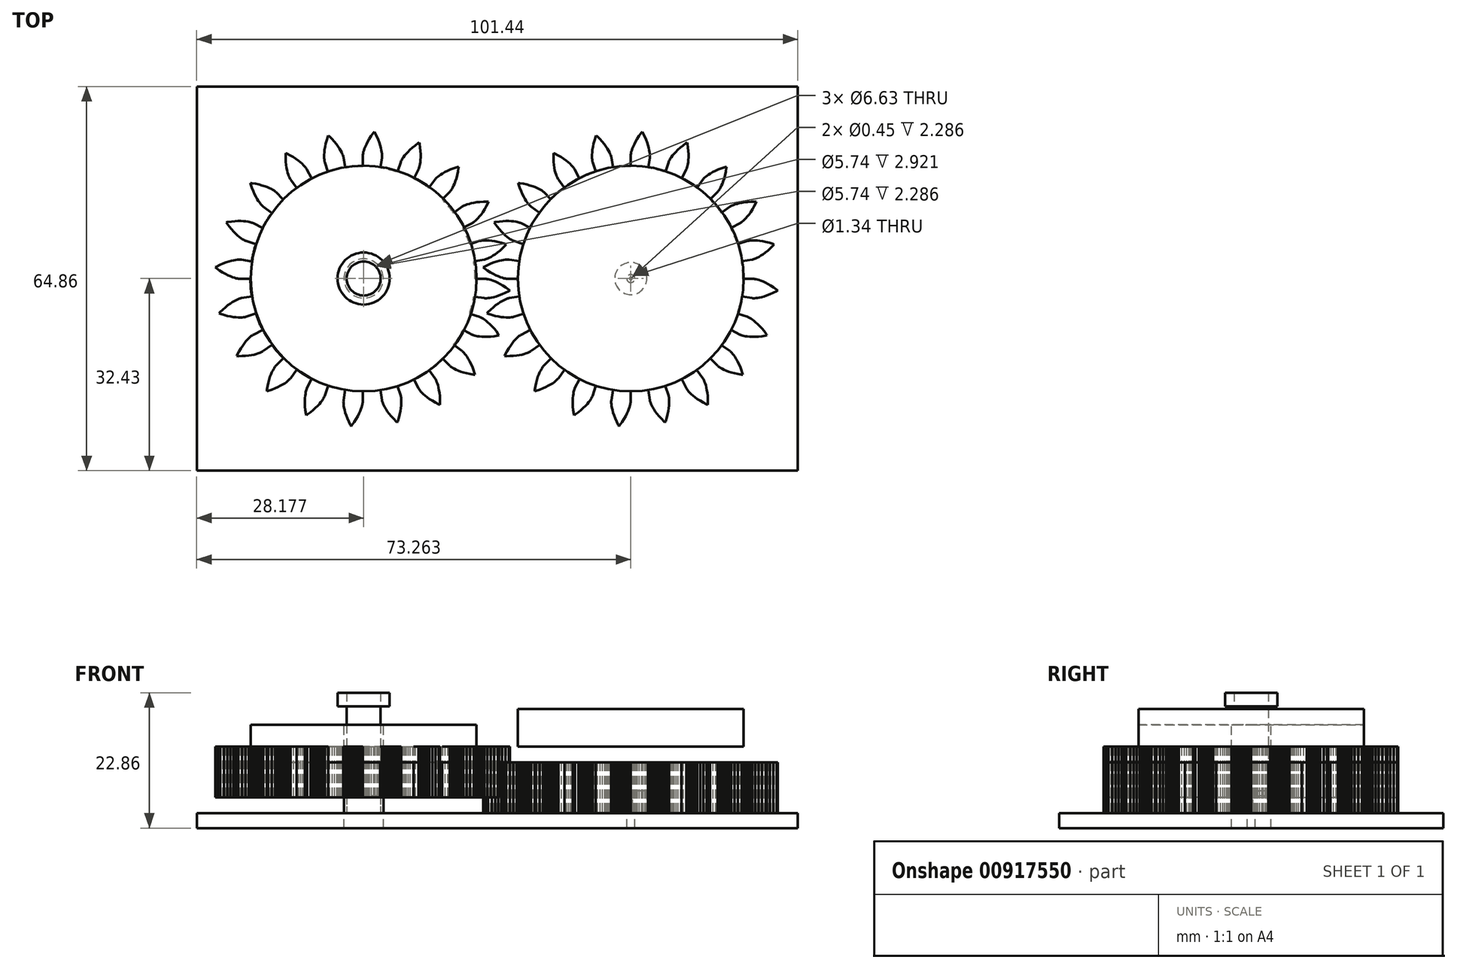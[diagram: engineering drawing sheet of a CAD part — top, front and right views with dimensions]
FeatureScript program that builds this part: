
annotation { "Feature Type Name" : "Feature", "Feature Type Description" : "" }
export const myFeature = defineFeature(function(context is Context, id is Id, definition is map)
    precondition{}
    {
        {
            var Q0;
            Q0=qCreatedBy(makeId("Top.planeOp"),FACE);
            var sketch = newSketch(context, id + "F0", { "sketchPlane" : qUnion([Q0])});
            skLineSegment(sketch, "E0.bottom", {"start": v(3.5, -4.99) * mm, "end": v(-3.5, -4.99) * mm});
            skLineSegment(sketch, "E0.top", {"start": v(3.5, 4.99) * mm, "end": v(-3.5, 4.99) * mm});
            skLineSegment(sketch, "E0.left", {"start": v(3.5, -4.99) * mm, "end": v(3.5, 4.99) * mm});
            skLineSegment(sketch, "E0.right", {"start": v(-3.5, -4.99) * mm, "end": v(-3.5, 4.99) * mm});
            skPoint(sketch, "E0.middle", {"position": v(0, 0) * mm});
            skCircle(sketch, "E1", {"center": v(-22.54, 0) * mm, "radius": 19.05 * mm});
            skPoint(sketch, "E2", {"position": v(-3.5, 0) * mm});
            skPoint(sketch, "E3", {"position": v(3.5, 0) * mm});
            skCircle(sketch, "E4", {"center": v(22.54, 0) * mm, "radius": 19.05 * mm});
            skCircle(sketch, "E5", {"center": v(-66.86, 21.55) * mm, "radius": 14.04 * mm});
            skCircle(sketch, "E6", {"center": v(-66.86, 21.55) * mm, "radius": 15.37 * mm, "construction": true});
            skCircle(sketch, "E7", {"center": v(-66.86, 21.55) * mm, "radius": 15.88 * mm, "construction": true});
            skCircle(sketch, "E8", {"center": v(-66.86, 21.55) * mm, "radius": 17.46 * mm});
            skLineSegment(sketch, "E9", {"start": v(-66.86, 21.55) * mm, "end": v(-82.23, 21.55) * mm, "construction": true});
            skLineSegment(sketch, "E10.1.0", {"start": v(-66.86, 21.55) * mm, "end": v(-82.2, 22.32) * mm, "construction": true});
            skLineSegment(sketch, "E10.2.0", {"start": v(-66.86, 21.55) * mm, "end": v(-82.15, 23.08) * mm, "construction": true});
            skLineSegment(sketch, "E10.3.0", {"start": v(-66.86, 21.55) * mm, "end": v(-82.05, 23.84) * mm, "construction": true});
            skLineSegment(sketch, "E10.4.0", {"start": v(-66.86, 21.55) * mm, "end": v(-81.92, 24.6) * mm, "construction": true});
            skLineSegment(sketch, "E10.5.0", {"start": v(-66.86, 21.55) * mm, "end": v(-81.75, 25.35) * mm, "construction": true});
            skLineSegment(sketch, "E10.6.0", {"start": v(-66.86, 21.55) * mm, "end": v(-81.54, 26.09) * mm, "construction": true});
            skLineSegment(sketch, "E10.7.0", {"start": v(-66.86, 21.55) * mm, "end": v(-81.3, 26.82) * mm, "construction": true});
            skLineSegment(sketch, "E10.8.0", {"start": v(-66.86, 21.55) * mm, "end": v(-81.01, 27.53) * mm, "construction": true});
            skLineSegment(sketch, "E10.9.0", {"start": v(-66.86, 21.55) * mm, "end": v(-80.7, 28.23) * mm, "construction": true});
            skLineSegment(sketch, "E10.10.0", {"start": v(-66.86, 21.55) * mm, "end": v(-80.34, 28.92) * mm, "construction": true});
            skLineSegment(sketch, "E10.11.0", {"start": v(-66.86, 21.55) * mm, "end": v(-79.96, 29.58) * mm, "construction": true});
            skLineSegment(sketch, "E10.12.0", {"start": v(-66.86, 21.55) * mm, "end": v(-79.54, 30.23) * mm, "construction": true});
            skLineSegment(sketch, "E10.13.0", {"start": v(-66.86, 21.55) * mm, "end": v(-79.1, 30.85) * mm, "construction": true});
            skLineSegment(sketch, "E10.14.0", {"start": v(-66.86, 21.55) * mm, "end": v(-78.61, 31.45) * mm, "construction": true});
            skLineSegment(sketch, "E10.anchor2", {"start": v(-66.86, 21.55) * mm, "end": v(-78.61, 31.45) * mm, "construction": true});
            skLineSegment(sketch, "E11", {"start": v(-82.2, 22.32) * mm, "end": v(-82.25, 21.55) * mm, "construction": true});
            skLineSegment(sketch, "E12", {"start": v(-82.15, 23.08) * mm, "end": v(-82.3, 21.55) * mm, "construction": true});
            skLineSegment(sketch, "E13", {"start": v(-82.05, 23.84) * mm, "end": v(-82.4, 21.56) * mm, "construction": true});
            skLineSegment(sketch, "E14", {"start": v(-81.75, 25.35) * mm, "end": v(-82.7, 21.63) * mm, "construction": true});
            skLineSegment(sketch, "E15", {"start": v(-81.54, 26.09) * mm, "end": v(-82.9, 21.68) * mm, "construction": true});
            skLineSegment(sketch, "E16", {"start": v(-81.3, 26.82) * mm, "end": v(-83.14, 21.76) * mm, "construction": true});
            skLineSegment(sketch, "E17", {"start": v(-81.01, 27.53) * mm, "end": v(-83.4, 21.87) * mm, "construction": true});
            skLineSegment(sketch, "E18", {"start": v(-80.7, 28.23) * mm, "end": v(-83.7, 22) * mm, "construction": true});
            skLineSegment(sketch, "E19", {"start": v(-80.34, 28.92) * mm, "end": v(-84.03, 22.17) * mm, "construction": true});
            skLineSegment(sketch, "E20", {"start": v(-79.96, 29.58) * mm, "end": v(-84.38, 22.37) * mm, "construction": true});
            skLineSegment(sketch, "E21", {"start": v(-81.92, 24.6) * mm, "end": v(-82.53, 21.59) * mm, "construction": true});
            skLineSegment(sketch, "E22", {"start": v(-79.54, 30.23) * mm, "end": v(-84.75, 22.61) * mm, "construction": true});
            skLineSegment(sketch, "E23", {"start": v(-79.1, 30.85) * mm, "end": v(-85.14, 22.9) * mm, "construction": true});
            skLineSegment(sketch, "E24", {"start": v(-78.61, 31.45) * mm, "end": v(-85.54, 23.22) * mm, "construction": true});
            skLineSegment(sketch, "E25", {"start": v(-66.86, 21.55) * mm, "end": v(-82.18, 22.75) * mm, "construction": true});
            skLineSegment(sketch, "E26", {"start": v(-80.9, 21.55) * mm, "end": v(-82.23, 21.55) * mm});
            skLineSegment(sketch, "E27.MirrorCS", {"start": v(-80.72, 23.74) * mm, "end": v(-82.04, 23.95) * mm});
            skLineSegment(sketch, "E28", {"start": v(-82.23, 21.55) * mm, "end": v(-82.25, 21.55) * mm});
            skLineSegment(sketch, "E29", {"start": v(-82.25, 21.55) * mm, "end": v(-82.3, 21.55) * mm});
            skLineSegment(sketch, "E30", {"start": v(-82.3, 21.55) * mm, "end": v(-82.4, 21.56) * mm});
            skLineSegment(sketch, "E31", {"start": v(-82.4, 21.56) * mm, "end": v(-82.53, 21.59) * mm});
            skLineSegment(sketch, "E32", {"start": v(-82.53, 21.59) * mm, "end": v(-82.7, 21.63) * mm});
            skLineSegment(sketch, "E33", {"start": v(-82.7, 21.63) * mm, "end": v(-82.9, 21.68) * mm});
            skLineSegment(sketch, "E34", {"start": v(-82.9, 21.68) * mm, "end": v(-83.14, 21.76) * mm});
            skLineSegment(sketch, "E35", {"start": v(-83.14, 21.76) * mm, "end": v(-83.4, 21.87) * mm});
            skLineSegment(sketch, "E36", {"start": v(-83.4, 21.87) * mm, "end": v(-83.7, 22) * mm});
            skLineSegment(sketch, "E37", {"start": v(-83.7, 22) * mm, "end": v(-84.03, 22.17) * mm});
            skLineSegment(sketch, "E38", {"start": v(-84.03, 22.17) * mm, "end": v(-84.38, 22.37) * mm});
            skLineSegment(sketch, "E39", {"start": v(-84.38, 22.37) * mm, "end": v(-84.75, 22.61) * mm});
            skLineSegment(sketch, "E40", {"start": v(-84.75, 22.61) * mm, "end": v(-85.14, 22.9) * mm});
            skLineSegment(sketch, "E41", {"start": v(-85.14, 22.9) * mm, "end": v(-85.54, 23.22) * mm});
            skLineSegment(sketch, "E42.MirrorCS", {"start": v(-82.04, 23.95) * mm, "end": v(-82.06, 23.95) * mm});
            skLineSegment(sketch, "E43.MirrorCS", {"start": v(-82.06, 23.95) * mm, "end": v(-82.11, 23.96) * mm});
            skLineSegment(sketch, "E44.MirrorCS", {"start": v(-82.11, 23.96) * mm, "end": v(-82.2, 23.96) * mm});
            skLineSegment(sketch, "E45.MirrorCS", {"start": v(-82.2, 23.96) * mm, "end": v(-82.34, 23.96) * mm});
            skLineSegment(sketch, "E46.MirrorCS", {"start": v(-82.52, 23.95) * mm, "end": v(-82.73, 23.92) * mm});
            skLineSegment(sketch, "E47.MirrorCS", {"start": v(-82.73, 23.92) * mm, "end": v(-82.97, 23.88) * mm});
            skLineSegment(sketch, "E48.MirrorCS", {"start": v(-82.97, 23.88) * mm, "end": v(-83.25, 23.82) * mm});
            skLineSegment(sketch, "E49.MirrorCS", {"start": v(-83.25, 23.82) * mm, "end": v(-83.57, 23.73) * mm});
            skLineSegment(sketch, "E50.MirrorCS", {"start": v(-83.91, 23.62) * mm, "end": v(-84.3, 23.47) * mm});
            skLineSegment(sketch, "E51.MirrorCS", {"start": v(-83.57, 23.73) * mm, "end": v(-83.91, 23.62) * mm});
            skLineSegment(sketch, "E52.MirrorCS", {"start": v(-84.3, 23.47) * mm, "end": v(-84.7, 23.3) * mm});
            skLineSegment(sketch, "E53.MirrorCS", {"start": v(-84.7, 23.3) * mm, "end": v(-85.12, 23.07) * mm});
            skLineSegment(sketch, "E54.MirrorCS", {"start": v(-85.12, 23.07) * mm, "end": v(-85.57, 22.82) * mm});
            skLineSegment(sketch, "E55.MirrorCS", {"start": v(-82.34, 23.96) * mm, "end": v(-82.52, 23.95) * mm});
            skLineSegment(sketch, "E56.1.0", {"start": v(-80.2, 17.2) * mm, "end": v(-81.47, 16.8) * mm});
            skLineSegment(sketch, "E56.1.1", {"start": v(-84.03, 17.99) * mm, "end": v(-84.36, 17.7) * mm});
            skLineSegment(sketch, "E56.1.2", {"start": v(-80.72, 19.35) * mm, "end": v(-82.04, 19.14) * mm});
            skLineSegment(sketch, "E56.1.3", {"start": v(-83.72, 18.24) * mm, "end": v(-84.03, 17.99) * mm});
            skLineSegment(sketch, "E56.1.4", {"start": v(-83.38, 16.83) * mm, "end": v(-83.78, 16.92) * mm});
            skLineSegment(sketch, "E56.1.5", {"start": v(-83.78, 16.92) * mm, "end": v(-84.2, 17.03) * mm});
            skLineSegment(sketch, "E56.1.6", {"start": v(-83.43, 18.46) * mm, "end": v(-83.72, 18.24) * mm});
            skLineSegment(sketch, "E56.1.7", {"start": v(-84.7, 17.36) * mm, "end": v(-85.05, 16.97) * mm});
            skLineSegment(sketch, "E56.1.8", {"start": v(-83.15, 18.64) * mm, "end": v(-83.43, 18.46) * mm});
            skLineSegment(sketch, "E56.1.9", {"start": v(-84.66, 17.18) * mm, "end": v(-85.14, 17.36) * mm});
            skLineSegment(sketch, "E56.1.10", {"start": v(-84.36, 17.7) * mm, "end": v(-84.7, 17.36) * mm});
            skLineSegment(sketch, "E56.1.11", {"start": v(-83.02, 16.78) * mm, "end": v(-83.38, 16.83) * mm});
            skLineSegment(sketch, "E56.1.12", {"start": v(-84.2, 17.03) * mm, "end": v(-84.66, 17.18) * mm});
            skLineSegment(sketch, "E56.1.13", {"start": v(-82.5, 19) * mm, "end": v(-82.68, 18.9) * mm});
            skLineSegment(sketch, "E56.1.14", {"start": v(-82.68, 18.9) * mm, "end": v(-82.9, 18.79) * mm});
            skLineSegment(sketch, "E56.1.15", {"start": v(-82.9, 18.79) * mm, "end": v(-83.15, 18.64) * mm});
            skLineSegment(sketch, "E56.1.16", {"start": v(-82.4, 16.72) * mm, "end": v(-82.7, 16.74) * mm});
            skLineSegment(sketch, "E56.1.17", {"start": v(-82.16, 16.72) * mm, "end": v(-82.4, 16.72) * mm});
            skLineSegment(sketch, "E56.1.18", {"start": v(-82.7, 16.74) * mm, "end": v(-83.02, 16.78) * mm});
            skLineSegment(sketch, "E56.1.19", {"start": v(-82.33, 19.05) * mm, "end": v(-82.5, 19) * mm});
            skLineSegment(sketch, "E56.1.20", {"start": v(-82.2, 19.1) * mm, "end": v(-82.33, 19.05) * mm});
            skLineSegment(sketch, "E56.1.21", {"start": v(-81.95, 16.73) * mm, "end": v(-82.16, 16.72) * mm});
            skLineSegment(sketch, "E56.1.22", {"start": v(-81.78, 16.74) * mm, "end": v(-81.95, 16.73) * mm});
            skLineSegment(sketch, "E56.1.23", {"start": v(-81.55, 16.78) * mm, "end": v(-81.64, 16.76) * mm});
            skLineSegment(sketch, "E56.1.24", {"start": v(-82.04, 19.14) * mm, "end": v(-82.06, 19.14) * mm});
            skLineSegment(sketch, "E56.1.25", {"start": v(-82.06, 19.14) * mm, "end": v(-82.11, 19.13) * mm});
            skLineSegment(sketch, "E56.1.26", {"start": v(-81.64, 16.76) * mm, "end": v(-81.78, 16.74) * mm});
            skLineSegment(sketch, "E56.1.27", {"start": v(-82.11, 19.13) * mm, "end": v(-82.2, 19.1) * mm});
            skLineSegment(sketch, "E56.1.28", {"start": v(-81.5, 16.8) * mm, "end": v(-81.55, 16.78) * mm});
            skLineSegment(sketch, "E56.1.29", {"start": v(-81.47, 16.8) * mm, "end": v(-81.5, 16.8) * mm});
            skLineSegment(sketch, "E56.2.0", {"start": v(-78.21, 13.3) * mm, "end": v(-79.3, 12.51) * mm});
            skLineSegment(sketch, "E56.2.1", {"start": v(-82.1, 12.86) * mm, "end": v(-82.31, 12.47) * mm});
            skLineSegment(sketch, "E56.2.2", {"start": v(-79.36, 15.17) * mm, "end": v(-80.55, 14.57) * mm});
            skLineSegment(sketch, "E56.2.3", {"start": v(-81.87, 13.2) * mm, "end": v(-82.1, 12.86) * mm});
            skLineSegment(sketch, "E56.2.4", {"start": v(-81.12, 11.96) * mm, "end": v(-81.52, 11.92) * mm});
            skLineSegment(sketch, "E56.2.5", {"start": v(-81.52, 11.92) * mm, "end": v(-81.96, 11.9) * mm});
            skLineSegment(sketch, "E56.2.6", {"start": v(-81.66, 13.5) * mm, "end": v(-81.87, 13.2) * mm});
            skLineSegment(sketch, "E56.2.7", {"start": v(-82.53, 12.05) * mm, "end": v(-82.75, 11.57) * mm});
            skLineSegment(sketch, "E56.2.8", {"start": v(-81.46, 13.75) * mm, "end": v(-81.66, 13.5) * mm});
            skLineSegment(sketch, "E56.2.9", {"start": v(-82.44, 11.9) * mm, "end": v(-82.96, 11.92) * mm});
            skLineSegment(sketch, "E56.2.10", {"start": v(-82.31, 12.47) * mm, "end": v(-82.53, 12.05) * mm});
            skLineSegment(sketch, "E56.2.11", {"start": v(-80.76, 12.01) * mm, "end": v(-81.12, 11.96) * mm});
            skLineSegment(sketch, "E56.2.12", {"start": v(-81.96, 11.9) * mm, "end": v(-82.44, 11.9) * mm});
            skLineSegment(sketch, "E56.2.13", {"start": v(-80.94, 14.28) * mm, "end": v(-81.1, 14.14) * mm});
            skLineSegment(sketch, "E56.2.14", {"start": v(-81.1, 14.14) * mm, "end": v(-81.27, 13.96) * mm});
            skLineSegment(sketch, "E56.2.15", {"start": v(-81.27, 13.96) * mm, "end": v(-81.46, 13.75) * mm});
            skLineSegment(sketch, "E56.2.16", {"start": v(-80.16, 12.15) * mm, "end": v(-80.44, 12.08) * mm});
            skLineSegment(sketch, "E56.2.17", {"start": v(-79.92, 12.23) * mm, "end": v(-80.16, 12.15) * mm});
            skLineSegment(sketch, "E56.2.18", {"start": v(-80.44, 12.08) * mm, "end": v(-80.76, 12.01) * mm});
            skLineSegment(sketch, "E56.2.19", {"start": v(-80.8, 14.4) * mm, "end": v(-80.94, 14.28) * mm});
            skLineSegment(sketch, "E56.2.20", {"start": v(-80.7, 14.48) * mm, "end": v(-80.8, 14.4) * mm});
            skLineSegment(sketch, "E56.2.21", {"start": v(-79.72, 12.3) * mm, "end": v(-79.92, 12.23) * mm});
            skLineSegment(sketch, "E56.2.22", {"start": v(-79.56, 12.37) * mm, "end": v(-79.72, 12.3) * mm});
            skLineSegment(sketch, "E56.2.23", {"start": v(-79.36, 12.47) * mm, "end": v(-79.44, 12.43) * mm});
            skLineSegment(sketch, "E56.2.24", {"start": v(-80.55, 14.57) * mm, "end": v(-80.57, 14.56) * mm});
            skLineSegment(sketch, "E56.2.25", {"start": v(-80.57, 14.56) * mm, "end": v(-80.62, 14.53) * mm});
            skLineSegment(sketch, "E56.2.26", {"start": v(-79.44, 12.43) * mm, "end": v(-79.56, 12.37) * mm});
            skLineSegment(sketch, "E56.2.27", {"start": v(-80.62, 14.53) * mm, "end": v(-80.7, 14.48) * mm});
            skLineSegment(sketch, "E56.2.28", {"start": v(-79.3, 12.5) * mm, "end": v(-79.36, 12.47) * mm});
            skLineSegment(sketch, "E56.2.29", {"start": v(-79.3, 12.51) * mm, "end": v(-79.3, 12.5) * mm});
            skLineSegment(sketch, "E56.3.0", {"start": v(-75.1, 10.19) * mm, "end": v(-75.9, 9.11) * mm});
            skLineSegment(sketch, "E56.3.1", {"start": v(-78.66, 8.57) * mm, "end": v(-78.75, 8.14) * mm});
            skLineSegment(sketch, "E56.3.2", {"start": v(-76.78, 11.62) * mm, "end": v(-77.72, 10.68) * mm});
            skLineSegment(sketch, "E56.3.3", {"start": v(-78.56, 8.96) * mm, "end": v(-78.66, 8.57) * mm});
            skLineSegment(sketch, "E56.3.4", {"start": v(-77.46, 8.02) * mm, "end": v(-77.82, 7.86) * mm});
            skLineSegment(sketch, "E56.3.5", {"start": v(-77.82, 7.86) * mm, "end": v(-78.24, 7.7) * mm});
            skLineSegment(sketch, "E56.3.6", {"start": v(-78.45, 9.31) * mm, "end": v(-78.56, 8.96) * mm});
            skLineSegment(sketch, "E56.3.7", {"start": v(-78.83, 7.67) * mm, "end": v(-78.89, 7.15) * mm});
            skLineSegment(sketch, "E56.3.8", {"start": v(-78.33, 9.62) * mm, "end": v(-78.45, 9.31) * mm});
            skLineSegment(sketch, "E56.3.9", {"start": v(-78.7, 7.55) * mm, "end": v(-79.2, 7.41) * mm});
            skLineSegment(sketch, "E56.3.10", {"start": v(-78.75, 8.14) * mm, "end": v(-78.83, 7.67) * mm});
            skLineSegment(sketch, "E56.3.11", {"start": v(-77.13, 8.19) * mm, "end": v(-77.46, 8.02) * mm});
            skLineSegment(sketch, "E56.3.12", {"start": v(-78.24, 7.7) * mm, "end": v(-78.7, 7.55) * mm});
            skLineSegment(sketch, "E56.3.13", {"start": v(-78, 10.29) * mm, "end": v(-78.1, 10.1) * mm});
            skLineSegment(sketch, "E56.3.14", {"start": v(-78.1, 10.1) * mm, "end": v(-78.22, 9.88) * mm});
            skLineSegment(sketch, "E56.3.15", {"start": v(-78.22, 9.88) * mm, "end": v(-78.33, 9.62) * mm});
            skLineSegment(sketch, "E56.3.16", {"start": v(-76.6, 8.5) * mm, "end": v(-76.85, 8.35) * mm});
            skLineSegment(sketch, "E56.3.17", {"start": v(-76.4, 8.65) * mm, "end": v(-76.6, 8.5) * mm});
            skLineSegment(sketch, "E56.3.18", {"start": v(-76.85, 8.35) * mm, "end": v(-77.13, 8.19) * mm});
            skLineSegment(sketch, "E56.3.19", {"start": v(-77.91, 10.44) * mm, "end": v(-78, 10.29) * mm});
            skLineSegment(sketch, "E56.3.20", {"start": v(-77.83, 10.55) * mm, "end": v(-77.91, 10.44) * mm});
            skLineSegment(sketch, "E56.3.21", {"start": v(-76.23, 8.78) * mm, "end": v(-76.4, 8.65) * mm});
            skLineSegment(sketch, "E56.3.22", {"start": v(-76.1, 8.9) * mm, "end": v(-76.23, 8.78) * mm});
            skLineSegment(sketch, "E56.3.23", {"start": v(-75.94, 9.05) * mm, "end": v(-76, 8.98) * mm});
            skLineSegment(sketch, "E56.3.24", {"start": v(-77.72, 10.68) * mm, "end": v(-77.74, 10.67) * mm});
            skLineSegment(sketch, "E56.3.25", {"start": v(-77.74, 10.67) * mm, "end": v(-77.77, 10.62) * mm});
            skLineSegment(sketch, "E56.3.26", {"start": v(-76, 8.98) * mm, "end": v(-76.1, 8.9) * mm});
            skLineSegment(sketch, "E56.3.27", {"start": v(-77.77, 10.62) * mm, "end": v(-77.83, 10.55) * mm});
            skLineSegment(sketch, "E56.3.28", {"start": v(-75.9, 9.1) * mm, "end": v(-75.94, 9.05) * mm});
            skLineSegment(sketch, "E56.3.29", {"start": v(-75.9, 9.11) * mm, "end": v(-75.9, 9.1) * mm});
            skLineSegment(sketch, "E56.4.0", {"start": v(-71.2, 8.2) * mm, "end": v(-71.6, 6.93) * mm});
            skLineSegment(sketch, "E56.4.1", {"start": v(-74.07, 5.56) * mm, "end": v(-74.03, 5.12) * mm});
            skLineSegment(sketch, "E56.4.2", {"start": v(-73.23, 9.04) * mm, "end": v(-73.83, 7.85) * mm});
            skLineSegment(sketch, "E56.4.3", {"start": v(-74.1, 5.96) * mm, "end": v(-74.07, 5.56) * mm});
            skLineSegment(sketch, "E56.4.4", {"start": v(-72.76, 5.4) * mm, "end": v(-73.06, 5.14) * mm});
            skLineSegment(sketch, "E56.4.5", {"start": v(-73.06, 5.14) * mm, "end": v(-73.4, 4.86) * mm});
            skLineSegment(sketch, "E56.4.6", {"start": v(-74.1, 6.33) * mm, "end": v(-74.1, 5.96) * mm});
            skLineSegment(sketch, "E56.4.7", {"start": v(-73.95, 4.65) * mm, "end": v(-73.85, 4.14) * mm});
            skLineSegment(sketch, "E56.4.8", {"start": v(-74.08, 6.65) * mm, "end": v(-74.1, 6.33) * mm});
            skLineSegment(sketch, "E56.4.9", {"start": v(-73.79, 4.58) * mm, "end": v(-74.22, 4.3) * mm});
            skLineSegment(sketch, "E56.4.10", {"start": v(-74.03, 5.12) * mm, "end": v(-73.95, 4.65) * mm});
            skLineSegment(sketch, "E56.4.11", {"start": v(-72.5, 5.67) * mm, "end": v(-72.76, 5.4) * mm});
            skLineSegment(sketch, "E56.4.12", {"start": v(-73.4, 4.86) * mm, "end": v(-73.79, 4.58) * mm});
            skLineSegment(sketch, "E56.4.13", {"start": v(-73.98, 7.4) * mm, "end": v(-74.02, 7.19) * mm});
            skLineSegment(sketch, "E56.4.14", {"start": v(-74.02, 7.19) * mm, "end": v(-74.06, 6.94) * mm});
            skLineSegment(sketch, "E56.4.15", {"start": v(-74.06, 6.94) * mm, "end": v(-74.08, 6.65) * mm});
            skLineSegment(sketch, "E56.4.16", {"start": v(-72.1, 6.13) * mm, "end": v(-72.28, 5.9) * mm});
            skLineSegment(sketch, "E56.4.17", {"start": v(-71.95, 6.33) * mm, "end": v(-72.1, 6.13) * mm});
            skLineSegment(sketch, "E56.4.18", {"start": v(-72.28, 5.9) * mm, "end": v(-72.5, 5.67) * mm});
            skLineSegment(sketch, "E56.4.19", {"start": v(-73.94, 7.56) * mm, "end": v(-73.98, 7.4) * mm});
            skLineSegment(sketch, "E56.4.20", {"start": v(-73.9, 7.7) * mm, "end": v(-73.94, 7.56) * mm});
            skLineSegment(sketch, "E56.4.21", {"start": v(-71.83, 6.5) * mm, "end": v(-71.95, 6.33) * mm});
            skLineSegment(sketch, "E56.4.22", {"start": v(-71.74, 6.65) * mm, "end": v(-71.83, 6.5) * mm});
            skLineSegment(sketch, "E56.4.23", {"start": v(-71.63, 6.86) * mm, "end": v(-71.68, 6.77) * mm});
            skLineSegment(sketch, "E56.4.24", {"start": v(-73.83, 7.85) * mm, "end": v(-73.84, 7.84) * mm});
            skLineSegment(sketch, "E56.4.25", {"start": v(-73.84, 7.84) * mm, "end": v(-73.86, 7.78) * mm});
            skLineSegment(sketch, "E56.4.26", {"start": v(-71.68, 6.77) * mm, "end": v(-71.74, 6.65) * mm});
            skLineSegment(sketch, "E56.4.27", {"start": v(-73.86, 7.78) * mm, "end": v(-73.9, 7.7) * mm});
            skLineSegment(sketch, "E56.4.28", {"start": v(-71.61, 6.91) * mm, "end": v(-71.63, 6.86) * mm});
            skLineSegment(sketch, "E56.4.29", {"start": v(-71.6, 6.93) * mm, "end": v(-71.61, 6.91) * mm});
            skLineSegment(sketch, "E56.5.0", {"start": v(-66.86, 7.5) * mm, "end": v(-66.86, 6.18) * mm});
            skLineSegment(sketch, "E56.5.1", {"start": v(-68.78, 4.11) * mm, "end": v(-68.6, 3.7) * mm});
            skLineSegment(sketch, "E56.5.2", {"start": v(-69.05, 7.68) * mm, "end": v(-69.26, 6.37) * mm});
            skLineSegment(sketch, "E56.5.3", {"start": v(-68.93, 4.49) * mm, "end": v(-68.78, 4.11) * mm});
            skLineSegment(sketch, "E56.5.4", {"start": v(-67.48, 4.37) * mm, "end": v(-67.68, 4.03) * mm});
            skLineSegment(sketch, "E56.5.5", {"start": v(-67.68, 4.03) * mm, "end": v(-67.92, 3.66) * mm});
            skLineSegment(sketch, "E56.5.6", {"start": v(-69.04, 4.84) * mm, "end": v(-68.93, 4.49) * mm});
            skLineSegment(sketch, "E56.5.7", {"start": v(-68.38, 3.28) * mm, "end": v(-68.13, 2.83) * mm});
            skLineSegment(sketch, "E56.5.8", {"start": v(-69.13, 5.15) * mm, "end": v(-69.04, 4.84) * mm});
            skLineSegment(sketch, "E56.5.9", {"start": v(-68.2, 3.27) * mm, "end": v(-68.53, 2.86) * mm});
            skLineSegment(sketch, "E56.5.10", {"start": v(-68.6, 3.7) * mm, "end": v(-68.38, 3.28) * mm});
            skLineSegment(sketch, "E56.5.11", {"start": v(-67.31, 4.7) * mm, "end": v(-67.48, 4.37) * mm});
            skLineSegment(sketch, "E56.5.12", {"start": v(-67.92, 3.66) * mm, "end": v(-68.2, 3.27) * mm});
            skLineSegment(sketch, "E56.5.13", {"start": v(-69.26, 5.89) * mm, "end": v(-69.23, 5.68) * mm});
            skLineSegment(sketch, "E56.5.14", {"start": v(-69.23, 5.68) * mm, "end": v(-69.19, 5.43) * mm});
            skLineSegment(sketch, "E56.5.15", {"start": v(-69.19, 5.43) * mm, "end": v(-69.13, 5.15) * mm});
            skLineSegment(sketch, "E56.5.16", {"start": v(-67.07, 5.26) * mm, "end": v(-67.18, 5) * mm});
            skLineSegment(sketch, "E56.5.17", {"start": v(-67, 5.5) * mm, "end": v(-67.07, 5.26) * mm});
            skLineSegment(sketch, "E56.5.18", {"start": v(-67.18, 5) * mm, "end": v(-67.31, 4.7) * mm});
            skLineSegment(sketch, "E56.5.19", {"start": v(-69.27, 6.06) * mm, "end": v(-69.26, 5.89) * mm});
            skLineSegment(sketch, "E56.5.20", {"start": v(-69.27, 6.2) * mm, "end": v(-69.27, 6.06) * mm});
            skLineSegment(sketch, "E56.5.21", {"start": v(-66.94, 5.7) * mm, "end": v(-67, 5.5) * mm});
            skLineSegment(sketch, "E56.5.22", {"start": v(-66.9, 5.87) * mm, "end": v(-66.94, 5.7) * mm});
            skLineSegment(sketch, "E56.5.23", {"start": v(-66.86, 6.1) * mm, "end": v(-66.87, 6) * mm});
            skLineSegment(sketch, "E56.5.24", {"start": v(-69.26, 6.37) * mm, "end": v(-69.26, 6.35) * mm});
            skLineSegment(sketch, "E56.5.25", {"start": v(-69.26, 6.35) * mm, "end": v(-69.27, 6.3) * mm});
            skLineSegment(sketch, "E56.5.26", {"start": v(-66.87, 6) * mm, "end": v(-66.9, 5.87) * mm});
            skLineSegment(sketch, "E56.5.27", {"start": v(-69.27, 6.3) * mm, "end": v(-69.27, 6.2) * mm});
            skLineSegment(sketch, "E56.5.28", {"start": v(-66.86, 6.16) * mm, "end": v(-66.86, 6.1) * mm});
            skLineSegment(sketch, "E56.5.29", {"start": v(-66.86, 6.18) * mm, "end": v(-66.86, 6.16) * mm});
            skLineSegment(sketch, "E56.6.0", {"start": v(-62.52, 8.2) * mm, "end": v(-62.1, 6.93) * mm});
            skLineSegment(sketch, "E56.6.1", {"start": v(-63.3, 4.37) * mm, "end": v(-63, 4.04) * mm});
            skLineSegment(sketch, "E56.6.2", {"start": v(-64.66, 7.68) * mm, "end": v(-64.45, 6.37) * mm});
            skLineSegment(sketch, "E56.6.3", {"start": v(-63.55, 4.68) * mm, "end": v(-63.3, 4.37) * mm});
            skLineSegment(sketch, "E56.6.4", {"start": v(-62.14, 5.02) * mm, "end": v(-62.23, 4.63) * mm});
            skLineSegment(sketch, "E56.6.5", {"start": v(-62.23, 4.63) * mm, "end": v(-62.34, 4.2) * mm});
            skLineSegment(sketch, "E56.6.6", {"start": v(-63.77, 4.98) * mm, "end": v(-63.55, 4.68) * mm});
            skLineSegment(sketch, "E56.6.7", {"start": v(-62.67, 3.7) * mm, "end": v(-62.28, 3.35) * mm});
            skLineSegment(sketch, "E56.6.8", {"start": v(-63.95, 5.25) * mm, "end": v(-63.77, 4.98) * mm});
            skLineSegment(sketch, "E56.6.9", {"start": v(-62.49, 3.74) * mm, "end": v(-62.67, 3.26) * mm});
            skLineSegment(sketch, "E56.6.10", {"start": v(-63, 4.04) * mm, "end": v(-62.67, 3.7) * mm});
            skLineSegment(sketch, "E56.6.11", {"start": v(-62.09, 5.38) * mm, "end": v(-62.14, 5.02) * mm});
            skLineSegment(sketch, "E56.6.12", {"start": v(-62.34, 4.2) * mm, "end": v(-62.49, 3.74) * mm});
            skLineSegment(sketch, "E56.6.13", {"start": v(-64.3, 5.91) * mm, "end": v(-64.21, 5.72) * mm});
            skLineSegment(sketch, "E56.6.14", {"start": v(-64.21, 5.72) * mm, "end": v(-64.1, 5.5) * mm});
            skLineSegment(sketch, "E56.6.15", {"start": v(-64.1, 5.5) * mm, "end": v(-63.95, 5.25) * mm});
            skLineSegment(sketch, "E56.6.16", {"start": v(-62.03, 6) * mm, "end": v(-62.05, 5.7) * mm});
            skLineSegment(sketch, "E56.6.17", {"start": v(-62.03, 6.24) * mm, "end": v(-62.03, 6) * mm});
            skLineSegment(sketch, "E56.6.18", {"start": v(-62.05, 5.7) * mm, "end": v(-62.09, 5.38) * mm});
            skLineSegment(sketch, "E56.6.19", {"start": v(-64.36, 6.07) * mm, "end": v(-64.3, 5.91) * mm});
            skLineSegment(sketch, "E56.6.20", {"start": v(-64.4, 6.2) * mm, "end": v(-64.36, 6.07) * mm});
            skLineSegment(sketch, "E56.6.21", {"start": v(-62.04, 6.46) * mm, "end": v(-62.03, 6.24) * mm});
            skLineSegment(sketch, "E56.6.22", {"start": v(-62.05, 6.63) * mm, "end": v(-62.04, 6.46) * mm});
            skLineSegment(sketch, "E56.6.23", {"start": v(-62.09, 6.86) * mm, "end": v(-62.07, 6.76) * mm});
            skLineSegment(sketch, "E56.6.24", {"start": v(-64.45, 6.37) * mm, "end": v(-64.45, 6.35) * mm});
            skLineSegment(sketch, "E56.6.25", {"start": v(-64.45, 6.35) * mm, "end": v(-64.44, 6.3) * mm});
            skLineSegment(sketch, "E56.6.26", {"start": v(-62.07, 6.76) * mm, "end": v(-62.05, 6.63) * mm});
            skLineSegment(sketch, "E56.6.27", {"start": v(-64.44, 6.3) * mm, "end": v(-64.4, 6.2) * mm});
            skLineSegment(sketch, "E56.6.28", {"start": v(-62.1, 6.91) * mm, "end": v(-62.09, 6.86) * mm});
            skLineSegment(sketch, "E56.6.29", {"start": v(-62.1, 6.93) * mm, "end": v(-62.1, 6.91) * mm});
            skLineSegment(sketch, "E56.7.0", {"start": v(-58.6, 10.19) * mm, "end": v(-57.82, 9.11) * mm});
            skLineSegment(sketch, "E56.7.1", {"start": v(-58.17, 6.31) * mm, "end": v(-57.78, 6.09) * mm});
            skLineSegment(sketch, "E56.7.2", {"start": v(-60.48, 9.04) * mm, "end": v(-59.88, 7.85) * mm});
            skLineSegment(sketch, "E56.7.3", {"start": v(-58.5, 6.53) * mm, "end": v(-58.17, 6.31) * mm});
            skLineSegment(sketch, "E56.7.4", {"start": v(-57.27, 7.29) * mm, "end": v(-57.23, 6.89) * mm});
            skLineSegment(sketch, "E56.7.5", {"start": v(-57.23, 6.89) * mm, "end": v(-57.2, 6.44) * mm});
            skLineSegment(sketch, "E56.7.6", {"start": v(-58.8, 6.74) * mm, "end": v(-58.5, 6.53) * mm});
            skLineSegment(sketch, "E56.7.7", {"start": v(-57.36, 5.87) * mm, "end": v(-56.88, 5.66) * mm});
            skLineSegment(sketch, "E56.7.8", {"start": v(-59.06, 6.95) * mm, "end": v(-58.8, 6.74) * mm});
            skLineSegment(sketch, "E56.7.9", {"start": v(-57.2, 5.96) * mm, "end": v(-57.23, 5.45) * mm});
            skLineSegment(sketch, "E56.7.10", {"start": v(-57.78, 6.09) * mm, "end": v(-57.36, 5.87) * mm});
            skLineSegment(sketch, "E56.7.11", {"start": v(-57.32, 7.65) * mm, "end": v(-57.27, 7.29) * mm});
            skLineSegment(sketch, "E56.7.12", {"start": v(-57.2, 6.44) * mm, "end": v(-57.2, 5.96) * mm});
            skLineSegment(sketch, "E56.7.13", {"start": v(-59.6, 7.47) * mm, "end": v(-59.45, 7.31) * mm});
            skLineSegment(sketch, "E56.7.14", {"start": v(-59.45, 7.31) * mm, "end": v(-59.27, 7.14) * mm});
            skLineSegment(sketch, "E56.7.15", {"start": v(-59.27, 7.14) * mm, "end": v(-59.06, 6.95) * mm});
            skLineSegment(sketch, "E56.7.16", {"start": v(-57.46, 8.25) * mm, "end": v(-57.39, 7.97) * mm});
            skLineSegment(sketch, "E56.7.17", {"start": v(-57.54, 8.49) * mm, "end": v(-57.46, 8.25) * mm});
            skLineSegment(sketch, "E56.7.18", {"start": v(-57.39, 7.97) * mm, "end": v(-57.32, 7.65) * mm});
            skLineSegment(sketch, "E56.7.19", {"start": v(-59.7, 7.6) * mm, "end": v(-59.6, 7.47) * mm});
            skLineSegment(sketch, "E56.7.20", {"start": v(-59.79, 7.7) * mm, "end": v(-59.7, 7.6) * mm});
            skLineSegment(sketch, "E56.7.21", {"start": v(-57.6, 8.68) * mm, "end": v(-57.54, 8.49) * mm});
            skLineSegment(sketch, "E56.7.22", {"start": v(-57.68, 8.84) * mm, "end": v(-57.6, 8.68) * mm});
            skLineSegment(sketch, "E56.7.23", {"start": v(-57.78, 9.05) * mm, "end": v(-57.74, 8.96) * mm});
            skLineSegment(sketch, "E56.7.24", {"start": v(-59.88, 7.85) * mm, "end": v(-59.87, 7.84) * mm});
            skLineSegment(sketch, "E56.7.25", {"start": v(-59.87, 7.84) * mm, "end": v(-59.84, 7.79) * mm});
            skLineSegment(sketch, "E56.7.26", {"start": v(-57.74, 8.96) * mm, "end": v(-57.68, 8.84) * mm});
            skLineSegment(sketch, "E56.7.27", {"start": v(-59.84, 7.79) * mm, "end": v(-59.79, 7.7) * mm});
            skLineSegment(sketch, "E56.7.28", {"start": v(-57.81, 9.1) * mm, "end": v(-57.78, 9.05) * mm});
            skLineSegment(sketch, "E56.7.29", {"start": v(-57.82, 9.11) * mm, "end": v(-57.81, 9.1) * mm});
            skLineSegment(sketch, "E56.8.0", {"start": v(-55.5, 13.3) * mm, "end": v(-54.42, 12.51) * mm});
            skLineSegment(sketch, "E56.8.1", {"start": v(-53.88, 9.74) * mm, "end": v(-53.45, 9.65) * mm});
            skLineSegment(sketch, "E56.8.2", {"start": v(-56.93, 11.62) * mm, "end": v(-55.99, 10.68) * mm});
            skLineSegment(sketch, "E56.8.3", {"start": v(-54.27, 9.85) * mm, "end": v(-53.88, 9.74) * mm});
            skLineSegment(sketch, "E56.8.4", {"start": v(-53.33, 10.95) * mm, "end": v(-53.17, 10.58) * mm});
            skLineSegment(sketch, "E56.8.5", {"start": v(-53.17, 10.58) * mm, "end": v(-53, 10.17) * mm});
            skLineSegment(sketch, "E56.8.6", {"start": v(-54.62, 9.96) * mm, "end": v(-54.27, 9.85) * mm});
            skLineSegment(sketch, "E56.8.7", {"start": v(-52.98, 9.57) * mm, "end": v(-52.46, 9.52) * mm});
            skLineSegment(sketch, "E56.8.8", {"start": v(-54.93, 10.07) * mm, "end": v(-54.62, 9.96) * mm});
            skLineSegment(sketch, "E56.8.9", {"start": v(-52.86, 9.71) * mm, "end": v(-52.72, 9.21) * mm});
            skLineSegment(sketch, "E56.8.10", {"start": v(-53.45, 9.65) * mm, "end": v(-52.98, 9.57) * mm});
            skLineSegment(sketch, "E56.8.11", {"start": v(-53.5, 11.27) * mm, "end": v(-53.33, 10.95) * mm});
            skLineSegment(sketch, "E56.8.12", {"start": v(-53, 10.17) * mm, "end": v(-52.86, 9.71) * mm});
            skLineSegment(sketch, "E56.8.13", {"start": v(-55.6, 10.4) * mm, "end": v(-55.41, 10.3) * mm});
            skLineSegment(sketch, "E56.8.14", {"start": v(-55.41, 10.3) * mm, "end": v(-55.2, 10.19) * mm});
            skLineSegment(sketch, "E56.8.15", {"start": v(-55.2, 10.19) * mm, "end": v(-54.93, 10.07) * mm});
            skLineSegment(sketch, "E56.8.16", {"start": v(-53.81, 11.8) * mm, "end": v(-53.66, 11.56) * mm});
            skLineSegment(sketch, "E56.8.17", {"start": v(-53.96, 12) * mm, "end": v(-53.81, 11.8) * mm});
            skLineSegment(sketch, "E56.8.18", {"start": v(-53.66, 11.56) * mm, "end": v(-53.5, 11.27) * mm});
            skLineSegment(sketch, "E56.8.19", {"start": v(-55.74, 10.5) * mm, "end": v(-55.6, 10.4) * mm});
            skLineSegment(sketch, "E56.8.20", {"start": v(-55.86, 10.57) * mm, "end": v(-55.74, 10.5) * mm});
            skLineSegment(sketch, "E56.8.21", {"start": v(-54.09, 12.17) * mm, "end": v(-53.96, 12) * mm});
            skLineSegment(sketch, "E56.8.22", {"start": v(-54.2, 12.3) * mm, "end": v(-54.09, 12.17) * mm});
            skLineSegment(sketch, "E56.8.23", {"start": v(-54.36, 12.46) * mm, "end": v(-54.3, 12.4) * mm});
            skLineSegment(sketch, "E56.8.24", {"start": v(-55.99, 10.68) * mm, "end": v(-55.97, 10.67) * mm});
            skLineSegment(sketch, "E56.8.25", {"start": v(-55.97, 10.67) * mm, "end": v(-55.93, 10.63) * mm});
            skLineSegment(sketch, "E56.8.26", {"start": v(-54.3, 12.4) * mm, "end": v(-54.2, 12.3) * mm});
            skLineSegment(sketch, "E56.8.27", {"start": v(-55.93, 10.63) * mm, "end": v(-55.86, 10.57) * mm});
            skLineSegment(sketch, "E56.8.28", {"start": v(-54.4, 12.5) * mm, "end": v(-54.36, 12.46) * mm});
            skLineSegment(sketch, "E56.8.29", {"start": v(-54.42, 12.51) * mm, "end": v(-54.4, 12.5) * mm});
            skLineSegment(sketch, "E56.9.0", {"start": v(-53.5, 17.2) * mm, "end": v(-52.24, 16.8) * mm});
            skLineSegment(sketch, "E56.9.1", {"start": v(-50.87, 14.33) * mm, "end": v(-50.43, 14.38) * mm});
            skLineSegment(sketch, "E56.9.2", {"start": v(-54.35, 15.17) * mm, "end": v(-53.16, 14.57) * mm});
            skLineSegment(sketch, "E56.9.3", {"start": v(-51.27, 14.3) * mm, "end": v(-50.87, 14.33) * mm});
            skLineSegment(sketch, "E56.9.4", {"start": v(-50.72, 15.65) * mm, "end": v(-50.45, 15.35) * mm});
            skLineSegment(sketch, "E56.9.5", {"start": v(-50.45, 15.35) * mm, "end": v(-50.17, 15) * mm});
            skLineSegment(sketch, "E56.9.6", {"start": v(-51.64, 14.3) * mm, "end": v(-51.27, 14.3) * mm});
            skLineSegment(sketch, "E56.9.7", {"start": v(-49.96, 14.45) * mm, "end": v(-49.45, 14.55) * mm});
            skLineSegment(sketch, "E56.9.8", {"start": v(-51.96, 14.32) * mm, "end": v(-51.64, 14.3) * mm});
            skLineSegment(sketch, "E56.9.9", {"start": v(-49.89, 14.62) * mm, "end": v(-49.6, 14.18) * mm});
            skLineSegment(sketch, "E56.9.10", {"start": v(-50.43, 14.38) * mm, "end": v(-49.96, 14.45) * mm});
            skLineSegment(sketch, "E56.9.11", {"start": v(-50.97, 15.9) * mm, "end": v(-50.72, 15.65) * mm});
            skLineSegment(sketch, "E56.9.12", {"start": v(-50.17, 15) * mm, "end": v(-49.89, 14.62) * mm});
            skLineSegment(sketch, "E56.9.13", {"start": v(-52.7, 14.43) * mm, "end": v(-52.5, 14.38) * mm});
            skLineSegment(sketch, "E56.9.14", {"start": v(-52.5, 14.38) * mm, "end": v(-52.25, 14.35) * mm});
            skLineSegment(sketch, "E56.9.15", {"start": v(-52.25, 14.35) * mm, "end": v(-51.96, 14.32) * mm});
            skLineSegment(sketch, "E56.9.16", {"start": v(-51.44, 16.3) * mm, "end": v(-51.22, 16.13) * mm});
            skLineSegment(sketch, "E56.9.17", {"start": v(-51.64, 16.46) * mm, "end": v(-51.44, 16.3) * mm});
            skLineSegment(sketch, "E56.9.18", {"start": v(-51.22, 16.13) * mm, "end": v(-50.97, 15.9) * mm});
            skLineSegment(sketch, "E56.9.19", {"start": v(-52.87, 14.47) * mm, "end": v(-52.7, 14.43) * mm});
            skLineSegment(sketch, "E56.9.20", {"start": v(-53, 14.5) * mm, "end": v(-52.87, 14.47) * mm});
            skLineSegment(sketch, "E56.9.21", {"start": v(-51.81, 16.58) * mm, "end": v(-51.64, 16.46) * mm});
            skLineSegment(sketch, "E56.9.22", {"start": v(-51.96, 16.66) * mm, "end": v(-51.81, 16.58) * mm});
            skLineSegment(sketch, "E56.9.23", {"start": v(-52.17, 16.77) * mm, "end": v(-52.08, 16.73) * mm});
            skLineSegment(sketch, "E56.9.24", {"start": v(-53.16, 14.57) * mm, "end": v(-53.15, 14.56) * mm});
            skLineSegment(sketch, "E56.9.25", {"start": v(-53.15, 14.56) * mm, "end": v(-53.1, 14.54) * mm});
            skLineSegment(sketch, "E56.9.26", {"start": v(-52.08, 16.73) * mm, "end": v(-51.96, 16.66) * mm});
            skLineSegment(sketch, "E56.9.27", {"start": v(-53.1, 14.54) * mm, "end": v(-53, 14.5) * mm});
            skLineSegment(sketch, "E56.9.28", {"start": v(-52.22, 16.8) * mm, "end": v(-52.17, 16.77) * mm});
            skLineSegment(sketch, "E56.9.29", {"start": v(-52.24, 16.8) * mm, "end": v(-52.22, 16.8) * mm});
            skLineSegment(sketch, "E56.10.0", {"start": v(-52.82, 21.55) * mm, "end": v(-51.49, 21.55) * mm});
            skLineSegment(sketch, "E56.10.1", {"start": v(-49.42, 19.62) * mm, "end": v(-49.02, 19.8) * mm});
            skLineSegment(sketch, "E56.10.2", {"start": v(-53, 19.35) * mm, "end": v(-51.68, 19.14) * mm});
            skLineSegment(sketch, "E56.10.3", {"start": v(-49.8, 19.48) * mm, "end": v(-49.42, 19.62) * mm});
            skLineSegment(sketch, "E56.10.4", {"start": v(-49.68, 20.92) * mm, "end": v(-49.34, 20.72) * mm});
            skLineSegment(sketch, "E56.10.5", {"start": v(-49.34, 20.72) * mm, "end": v(-48.96, 20.48) * mm});
            skLineSegment(sketch, "E56.10.6", {"start": v(-50.14, 19.36) * mm, "end": v(-49.8, 19.48) * mm});
            skLineSegment(sketch, "E56.10.7", {"start": v(-48.59, 20.02) * mm, "end": v(-48.14, 20.28) * mm});
            skLineSegment(sketch, "E56.10.8", {"start": v(-50.46, 19.28) * mm, "end": v(-50.14, 19.36) * mm});
            skLineSegment(sketch, "E56.10.9", {"start": v(-48.58, 20.2) * mm, "end": v(-48.17, 19.87) * mm});
            skLineSegment(sketch, "E56.10.10", {"start": v(-49.02, 19.8) * mm, "end": v(-48.59, 20.02) * mm});
            skLineSegment(sketch, "E56.10.11", {"start": v(-50, 21.09) * mm, "end": v(-49.68, 20.92) * mm});
            skLineSegment(sketch, "E56.10.12", {"start": v(-48.96, 20.48) * mm, "end": v(-48.58, 20.2) * mm});
            skLineSegment(sketch, "E56.10.13", {"start": v(-51.2, 19.15) * mm, "end": v(-50.99, 19.17) * mm});
            skLineSegment(sketch, "E56.10.14", {"start": v(-50.99, 19.17) * mm, "end": v(-50.74, 19.21) * mm});
            skLineSegment(sketch, "E56.10.15", {"start": v(-50.74, 19.21) * mm, "end": v(-50.46, 19.28) * mm});
            skLineSegment(sketch, "E56.10.16", {"start": v(-50.57, 21.33) * mm, "end": v(-50.3, 21.22) * mm});
            skLineSegment(sketch, "E56.10.17", {"start": v(-50.81, 21.4) * mm, "end": v(-50.57, 21.33) * mm});
            skLineSegment(sketch, "E56.10.18", {"start": v(-50.3, 21.22) * mm, "end": v(-50, 21.09) * mm});
            skLineSegment(sketch, "E56.10.19", {"start": v(-51.37, 19.14) * mm, "end": v(-51.2, 19.15) * mm});
            skLineSegment(sketch, "E56.10.20", {"start": v(-51.5, 19.13) * mm, "end": v(-51.37, 19.14) * mm});
            skLineSegment(sketch, "E56.10.21", {"start": v(-51.01, 21.47) * mm, "end": v(-50.81, 21.4) * mm});
            skLineSegment(sketch, "E56.10.22", {"start": v(-51.18, 21.5) * mm, "end": v(-51.01, 21.47) * mm});
            skLineSegment(sketch, "E56.10.23", {"start": v(-51.41, 21.54) * mm, "end": v(-51.32, 21.53) * mm});
            skLineSegment(sketch, "E56.10.24", {"start": v(-51.68, 19.14) * mm, "end": v(-51.66, 19.14) * mm});
            skLineSegment(sketch, "E56.10.25", {"start": v(-51.66, 19.14) * mm, "end": v(-51.6, 19.14) * mm});
            skLineSegment(sketch, "E56.10.26", {"start": v(-51.32, 21.53) * mm, "end": v(-51.18, 21.5) * mm});
            skLineSegment(sketch, "E56.10.27", {"start": v(-51.6, 19.14) * mm, "end": v(-51.5, 19.13) * mm});
            skLineSegment(sketch, "E56.10.28", {"start": v(-51.47, 21.55) * mm, "end": v(-51.41, 21.54) * mm});
            skLineSegment(sketch, "E56.10.29", {"start": v(-51.49, 21.55) * mm, "end": v(-51.47, 21.55) * mm});
            skLineSegment(sketch, "E56.11.0", {"start": v(-53.5, 25.88) * mm, "end": v(-52.24, 26.3) * mm});
            skLineSegment(sketch, "E56.11.1", {"start": v(-49.68, 25.1) * mm, "end": v(-49.35, 25.4) * mm});
            skLineSegment(sketch, "E56.11.2", {"start": v(-53, 23.74) * mm, "end": v(-51.68, 23.95) * mm});
            skLineSegment(sketch, "E56.11.3", {"start": v(-50, 24.85) * mm, "end": v(-49.68, 25.1) * mm});
            skLineSegment(sketch, "E56.11.4", {"start": v(-50.33, 26.26) * mm, "end": v(-49.94, 26.17) * mm});
            skLineSegment(sketch, "E56.11.5", {"start": v(-49.94, 26.17) * mm, "end": v(-49.51, 26.06) * mm});
            skLineSegment(sketch, "E56.11.6", {"start": v(-50.29, 24.63) * mm, "end": v(-50, 24.85) * mm});
            skLineSegment(sketch, "E56.11.7", {"start": v(-49.01, 25.74) * mm, "end": v(-48.66, 26.12) * mm});
            skLineSegment(sketch, "E56.11.8", {"start": v(-50.56, 24.45) * mm, "end": v(-50.29, 24.63) * mm});
            skLineSegment(sketch, "E56.11.9", {"start": v(-49.05, 25.91) * mm, "end": v(-48.57, 25.73) * mm});
            skLineSegment(sketch, "E56.11.10", {"start": v(-49.35, 25.4) * mm, "end": v(-49.01, 25.74) * mm});
            skLineSegment(sketch, "E56.11.11", {"start": v(-50.7, 26.32) * mm, "end": v(-50.33, 26.26) * mm});
            skLineSegment(sketch, "E56.11.12", {"start": v(-49.51, 26.06) * mm, "end": v(-49.05, 25.91) * mm});
            skLineSegment(sketch, "E56.11.13", {"start": v(-51.22, 24.1) * mm, "end": v(-51.03, 24.2) * mm});
            skLineSegment(sketch, "E56.11.14", {"start": v(-51.03, 24.2) * mm, "end": v(-50.8, 24.3) * mm});
            skLineSegment(sketch, "E56.11.15", {"start": v(-50.8, 24.3) * mm, "end": v(-50.56, 24.45) * mm});
            skLineSegment(sketch, "E56.11.16", {"start": v(-51.3, 26.37) * mm, "end": v(-51.02, 26.35) * mm});
            skLineSegment(sketch, "E56.11.17", {"start": v(-51.55, 26.37) * mm, "end": v(-51.3, 26.37) * mm});
            skLineSegment(sketch, "E56.11.18", {"start": v(-51.02, 26.35) * mm, "end": v(-50.7, 26.32) * mm});
            skLineSegment(sketch, "E56.11.19", {"start": v(-51.38, 24.04) * mm, "end": v(-51.22, 24.1) * mm});
            skLineSegment(sketch, "E56.11.20", {"start": v(-51.5, 24) * mm, "end": v(-51.38, 24.04) * mm});
            skLineSegment(sketch, "E56.11.21", {"start": v(-51.77, 26.37) * mm, "end": v(-51.55, 26.37) * mm});
            skLineSegment(sketch, "E56.11.22", {"start": v(-51.94, 26.35) * mm, "end": v(-51.77, 26.37) * mm});
            skLineSegment(sketch, "E56.11.23", {"start": v(-52.17, 26.32) * mm, "end": v(-52.07, 26.33) * mm});
            skLineSegment(sketch, "E56.11.24", {"start": v(-51.68, 23.95) * mm, "end": v(-51.66, 23.95) * mm});
            skLineSegment(sketch, "E56.11.25", {"start": v(-51.66, 23.95) * mm, "end": v(-51.6, 23.97) * mm});
            skLineSegment(sketch, "E56.11.26", {"start": v(-52.07, 26.33) * mm, "end": v(-51.94, 26.35) * mm});
            skLineSegment(sketch, "E56.11.27", {"start": v(-51.6, 23.97) * mm, "end": v(-51.5, 24) * mm});
            skLineSegment(sketch, "E56.11.28", {"start": v(-52.22, 26.3) * mm, "end": v(-52.17, 26.32) * mm});
            skLineSegment(sketch, "E56.11.29", {"start": v(-52.24, 26.3) * mm, "end": v(-52.22, 26.3) * mm});
            skLineSegment(sketch, "E56.12.0", {"start": v(-55.5, 29.8) * mm, "end": v(-54.42, 30.58) * mm});
            skLineSegment(sketch, "E56.12.1", {"start": v(-51.62, 30.24) * mm, "end": v(-51.4, 30.62) * mm});
            skLineSegment(sketch, "E56.12.2", {"start": v(-54.35, 27.92) * mm, "end": v(-53.16, 28.52) * mm});
            skLineSegment(sketch, "E56.12.3", {"start": v(-51.84, 29.9) * mm, "end": v(-51.62, 30.24) * mm});
            skLineSegment(sketch, "E56.12.4", {"start": v(-52.6, 31.14) * mm, "end": v(-52.2, 31.18) * mm});
            skLineSegment(sketch, "E56.12.5", {"start": v(-52.2, 31.18) * mm, "end": v(-51.75, 31.2) * mm});
            skLineSegment(sketch, "E56.12.6", {"start": v(-52.05, 29.6) * mm, "end": v(-51.84, 29.9) * mm});
            skLineSegment(sketch, "E56.12.7", {"start": v(-51.18, 31.05) * mm, "end": v(-50.97, 31.52) * mm});
            skLineSegment(sketch, "E56.12.8", {"start": v(-52.26, 29.35) * mm, "end": v(-52.05, 29.6) * mm});
            skLineSegment(sketch, "E56.12.9", {"start": v(-51.27, 31.2) * mm, "end": v(-50.76, 31.18) * mm});
            skLineSegment(sketch, "E56.12.10", {"start": v(-51.4, 30.62) * mm, "end": v(-51.18, 31.05) * mm});
            skLineSegment(sketch, "E56.12.11", {"start": v(-52.96, 31.08) * mm, "end": v(-52.6, 31.14) * mm});
            skLineSegment(sketch, "E56.12.12", {"start": v(-51.75, 31.2) * mm, "end": v(-51.27, 31.2) * mm});
            skLineSegment(sketch, "E56.12.13", {"start": v(-52.78, 28.8) * mm, "end": v(-52.62, 28.95) * mm});
            skLineSegment(sketch, "E56.12.14", {"start": v(-52.62, 28.95) * mm, "end": v(-52.45, 29.13) * mm});
            skLineSegment(sketch, "E56.12.15", {"start": v(-52.45, 29.13) * mm, "end": v(-52.26, 29.35) * mm});
            skLineSegment(sketch, "E56.12.16", {"start": v(-53.56, 30.94) * mm, "end": v(-53.28, 31.01) * mm});
            skLineSegment(sketch, "E56.12.17", {"start": v(-53.8, 30.87) * mm, "end": v(-53.56, 30.94) * mm});
            skLineSegment(sketch, "E56.12.18", {"start": v(-53.28, 31.01) * mm, "end": v(-52.96, 31.08) * mm});
            skLineSegment(sketch, "E56.12.19", {"start": v(-52.9, 28.7) * mm, "end": v(-52.78, 28.8) * mm});
            skLineSegment(sketch, "E56.12.20", {"start": v(-53.02, 28.62) * mm, "end": v(-52.9, 28.7) * mm});
            skLineSegment(sketch, "E56.12.21", {"start": v(-54, 30.8) * mm, "end": v(-53.8, 30.87) * mm});
            skLineSegment(sketch, "E56.12.22", {"start": v(-54.15, 30.73) * mm, "end": v(-54, 30.8) * mm});
            skLineSegment(sketch, "E56.12.23", {"start": v(-54.36, 30.62) * mm, "end": v(-54.27, 30.67) * mm});
            skLineSegment(sketch, "E56.12.24", {"start": v(-53.16, 28.52) * mm, "end": v(-53.15, 28.53) * mm});
            skLineSegment(sketch, "E56.12.25", {"start": v(-53.15, 28.53) * mm, "end": v(-53.1, 28.56) * mm});
            skLineSegment(sketch, "E56.12.26", {"start": v(-54.27, 30.67) * mm, "end": v(-54.15, 30.73) * mm});
            skLineSegment(sketch, "E56.12.27", {"start": v(-53.1, 28.56) * mm, "end": v(-53.02, 28.62) * mm});
            skLineSegment(sketch, "E56.12.28", {"start": v(-54.4, 30.6) * mm, "end": v(-54.36, 30.62) * mm});
            skLineSegment(sketch, "E56.12.29", {"start": v(-54.42, 30.58) * mm, "end": v(-54.4, 30.6) * mm});
            skLineSegment(sketch, "E56.13.0", {"start": v(-58.6, 32.9) * mm, "end": v(-57.82, 33.98) * mm});
            skLineSegment(sketch, "E56.13.1", {"start": v(-55.05, 34.52) * mm, "end": v(-54.96, 34.95) * mm});
            skLineSegment(sketch, "E56.13.2", {"start": v(-56.93, 31.47) * mm, "end": v(-55.99, 32.41) * mm});
            skLineSegment(sketch, "E56.13.3", {"start": v(-55.16, 34.13) * mm, "end": v(-55.05, 34.52) * mm});
            skLineSegment(sketch, "E56.13.4", {"start": v(-56.26, 35.07) * mm, "end": v(-55.89, 35.24) * mm});
            skLineSegment(sketch, "E56.13.5", {"start": v(-55.89, 35.24) * mm, "end": v(-55.48, 35.4) * mm});
            skLineSegment(sketch, "E56.13.6", {"start": v(-55.27, 33.78) * mm, "end": v(-55.16, 34.13) * mm});
            skLineSegment(sketch, "E56.13.7", {"start": v(-54.88, 35.43) * mm, "end": v(-54.83, 35.94) * mm});
            skLineSegment(sketch, "E56.13.8", {"start": v(-55.38, 33.48) * mm, "end": v(-55.27, 33.78) * mm});
            skLineSegment(sketch, "E56.13.9", {"start": v(-55.02, 35.54) * mm, "end": v(-54.52, 35.68) * mm});
            skLineSegment(sketch, "E56.13.10", {"start": v(-54.96, 34.95) * mm, "end": v(-54.88, 35.43) * mm});
            skLineSegment(sketch, "E56.13.11", {"start": v(-56.58, 34.9) * mm, "end": v(-56.26, 35.07) * mm});
            skLineSegment(sketch, "E56.13.12", {"start": v(-55.48, 35.4) * mm, "end": v(-55.02, 35.54) * mm});
            skLineSegment(sketch, "E56.13.13", {"start": v(-55.71, 32.8) * mm, "end": v(-55.6, 32.99) * mm});
            skLineSegment(sketch, "E56.13.14", {"start": v(-55.6, 32.99) * mm, "end": v(-55.5, 33.21) * mm});
            skLineSegment(sketch, "E56.13.15", {"start": v(-55.5, 33.21) * mm, "end": v(-55.38, 33.48) * mm});
            skLineSegment(sketch, "E56.13.16", {"start": v(-57.11, 34.6) * mm, "end": v(-56.87, 34.75) * mm});
            skLineSegment(sketch, "E56.13.17", {"start": v(-57.31, 34.45) * mm, "end": v(-57.11, 34.6) * mm});
            skLineSegment(sketch, "E56.13.18", {"start": v(-56.87, 34.75) * mm, "end": v(-56.58, 34.9) * mm});
            skLineSegment(sketch, "E56.13.19", {"start": v(-55.8, 32.66) * mm, "end": v(-55.71, 32.8) * mm});
            skLineSegment(sketch, "E56.13.20", {"start": v(-55.88, 32.55) * mm, "end": v(-55.8, 32.66) * mm});
            skLineSegment(sketch, "E56.13.21", {"start": v(-57.48, 34.32) * mm, "end": v(-57.31, 34.45) * mm});
            skLineSegment(sketch, "E56.13.22", {"start": v(-57.61, 34.2) * mm, "end": v(-57.48, 34.32) * mm});
            skLineSegment(sketch, "E56.13.23", {"start": v(-57.77, 34.04) * mm, "end": v(-57.7, 34.1) * mm});
            skLineSegment(sketch, "E56.13.24", {"start": v(-55.99, 32.41) * mm, "end": v(-55.98, 32.43) * mm});
            skLineSegment(sketch, "E56.13.25", {"start": v(-55.98, 32.43) * mm, "end": v(-55.94, 32.47) * mm});
            skLineSegment(sketch, "E56.13.26", {"start": v(-57.7, 34.1) * mm, "end": v(-57.61, 34.2) * mm});
            skLineSegment(sketch, "E56.13.27", {"start": v(-55.94, 32.47) * mm, "end": v(-55.88, 32.55) * mm});
            skLineSegment(sketch, "E56.13.28", {"start": v(-57.81, 34) * mm, "end": v(-57.77, 34.04) * mm});
            skLineSegment(sketch, "E56.13.29", {"start": v(-57.82, 33.98) * mm, "end": v(-57.81, 34) * mm});
            skLineSegment(sketch, "E56.14.0", {"start": v(-62.52, 34.9) * mm, "end": v(-62.1, 36.16) * mm});
            skLineSegment(sketch, "E56.14.1", {"start": v(-59.64, 37.53) * mm, "end": v(-59.68, 37.97) * mm});
            skLineSegment(sketch, "E56.14.2", {"start": v(-60.48, 34.06) * mm, "end": v(-59.88, 35.24) * mm});
            skLineSegment(sketch, "E56.14.3", {"start": v(-59.62, 37.13) * mm, "end": v(-59.64, 37.53) * mm});
            skLineSegment(sketch, "E56.14.4", {"start": v(-60.96, 37.69) * mm, "end": v(-60.66, 37.95) * mm});
            skLineSegment(sketch, "E56.14.5", {"start": v(-60.66, 37.95) * mm, "end": v(-60.31, 38.23) * mm});
            skLineSegment(sketch, "E56.14.6", {"start": v(-59.62, 36.77) * mm, "end": v(-59.62, 37.13) * mm});
            skLineSegment(sketch, "E56.14.7", {"start": v(-59.76, 38.45) * mm, "end": v(-59.86, 38.96) * mm});
            skLineSegment(sketch, "E56.14.8", {"start": v(-59.63, 36.44) * mm, "end": v(-59.62, 36.77) * mm});
            skLineSegment(sketch, "E56.14.9", {"start": v(-59.93, 38.52) * mm, "end": v(-59.5, 38.8) * mm});
            skLineSegment(sketch, "E56.14.10", {"start": v(-59.68, 37.97) * mm, "end": v(-59.76, 38.45) * mm});
            skLineSegment(sketch, "E56.14.11", {"start": v(-61.22, 37.43) * mm, "end": v(-60.96, 37.69) * mm});
            skLineSegment(sketch, "E56.14.12", {"start": v(-60.31, 38.23) * mm, "end": v(-59.93, 38.52) * mm});
            skLineSegment(sketch, "E56.14.13", {"start": v(-59.74, 35.7) * mm, "end": v(-59.7, 35.9) * mm});
            skLineSegment(sketch, "E56.14.14", {"start": v(-59.7, 35.9) * mm, "end": v(-59.66, 36.15) * mm});
            skLineSegment(sketch, "E56.14.15", {"start": v(-59.66, 36.15) * mm, "end": v(-59.63, 36.44) * mm});
            skLineSegment(sketch, "E56.14.16", {"start": v(-61.62, 36.96) * mm, "end": v(-61.44, 37.19) * mm});
            skLineSegment(sketch, "E56.14.17", {"start": v(-61.77, 36.76) * mm, "end": v(-61.62, 36.96) * mm});
            skLineSegment(sketch, "E56.14.18", {"start": v(-61.44, 37.19) * mm, "end": v(-61.22, 37.43) * mm});
            skLineSegment(sketch, "E56.14.19", {"start": v(-59.78, 35.53) * mm, "end": v(-59.74, 35.7) * mm});
            skLineSegment(sketch, "E56.14.20", {"start": v(-59.82, 35.4) * mm, "end": v(-59.78, 35.53) * mm});
            skLineSegment(sketch, "E56.14.21", {"start": v(-61.89, 36.59) * mm, "end": v(-61.77, 36.76) * mm});
            skLineSegment(sketch, "E56.14.22", {"start": v(-61.97, 36.44) * mm, "end": v(-61.89, 36.59) * mm});
            skLineSegment(sketch, "E56.14.23", {"start": v(-62.08, 36.24) * mm, "end": v(-62.04, 36.32) * mm});
            skLineSegment(sketch, "E56.14.24", {"start": v(-59.88, 35.24) * mm, "end": v(-59.87, 35.26) * mm});
            skLineSegment(sketch, "E56.14.25", {"start": v(-59.87, 35.26) * mm, "end": v(-59.85, 35.31) * mm});
            skLineSegment(sketch, "E56.14.26", {"start": v(-62.04, 36.32) * mm, "end": v(-61.97, 36.44) * mm});
            skLineSegment(sketch, "E56.14.27", {"start": v(-59.85, 35.31) * mm, "end": v(-59.82, 35.4) * mm});
            skLineSegment(sketch, "E56.14.28", {"start": v(-62.1, 36.18) * mm, "end": v(-62.08, 36.24) * mm});
            skLineSegment(sketch, "E56.14.29", {"start": v(-62.1, 36.16) * mm, "end": v(-62.1, 36.18) * mm});
            skLineSegment(sketch, "E56.15.0", {"start": v(-66.86, 35.59) * mm, "end": v(-66.86, 36.92) * mm});
            skLineSegment(sketch, "E56.15.1", {"start": v(-64.93, 38.98) * mm, "end": v(-65.11, 39.39) * mm});
            skLineSegment(sketch, "E56.15.2", {"start": v(-64.66, 35.41) * mm, "end": v(-64.45, 36.73) * mm});
            skLineSegment(sketch, "E56.15.3", {"start": v(-64.79, 38.6) * mm, "end": v(-64.93, 38.98) * mm});
            skLineSegment(sketch, "E56.15.4", {"start": v(-66.23, 38.72) * mm, "end": v(-66.03, 39.07) * mm});
            skLineSegment(sketch, "E56.15.5", {"start": v(-66.03, 39.07) * mm, "end": v(-65.79, 39.44) * mm});
            skLineSegment(sketch, "E56.15.6", {"start": v(-64.67, 38.26) * mm, "end": v(-64.79, 38.6) * mm});
            skLineSegment(sketch, "E56.15.7", {"start": v(-65.33, 39.81) * mm, "end": v(-65.59, 40.26) * mm});
            skLineSegment(sketch, "E56.15.8", {"start": v(-64.59, 37.94) * mm, "end": v(-64.67, 38.26) * mm});
            skLineSegment(sketch, "E56.15.9", {"start": v(-65.5, 39.83) * mm, "end": v(-65.18, 40.23) * mm});
            skLineSegment(sketch, "E56.15.10", {"start": v(-65.11, 39.39) * mm, "end": v(-65.33, 39.81) * mm});
            skLineSegment(sketch, "E56.15.11", {"start": v(-66.4, 38.4) * mm, "end": v(-66.23, 38.72) * mm});
            skLineSegment(sketch, "E56.15.12", {"start": v(-65.79, 39.44) * mm, "end": v(-65.5, 39.83) * mm});
            skLineSegment(sketch, "E56.15.13", {"start": v(-64.46, 37.2) * mm, "end": v(-64.48, 37.42) * mm});
            skLineSegment(sketch, "E56.15.14", {"start": v(-64.48, 37.42) * mm, "end": v(-64.52, 37.66) * mm});
            skLineSegment(sketch, "E56.15.15", {"start": v(-64.52, 37.66) * mm, "end": v(-64.59, 37.94) * mm});
            skLineSegment(sketch, "E56.15.16", {"start": v(-66.64, 37.83) * mm, "end": v(-66.53, 38.1) * mm});
            skLineSegment(sketch, "E56.15.17", {"start": v(-66.72, 37.6) * mm, "end": v(-66.64, 37.83) * mm});
            skLineSegment(sketch, "E56.15.18", {"start": v(-66.53, 38.1) * mm, "end": v(-66.4, 38.4) * mm});
            skLineSegment(sketch, "E56.15.19", {"start": v(-64.45, 37.03) * mm, "end": v(-64.46, 37.2) * mm});
            skLineSegment(sketch, "E56.15.20", {"start": v(-64.44, 36.9) * mm, "end": v(-64.45, 37.03) * mm});
            skLineSegment(sketch, "E56.15.21", {"start": v(-66.78, 37.39) * mm, "end": v(-66.72, 37.6) * mm});
            skLineSegment(sketch, "E56.15.22", {"start": v(-66.82, 37.22) * mm, "end": v(-66.78, 37.39) * mm});
            skLineSegment(sketch, "E56.15.23", {"start": v(-66.85, 37) * mm, "end": v(-66.84, 37.09) * mm});
            skLineSegment(sketch, "E56.15.24", {"start": v(-64.45, 36.73) * mm, "end": v(-64.45, 36.75) * mm});
            skLineSegment(sketch, "E56.15.25", {"start": v(-64.45, 36.75) * mm, "end": v(-64.45, 36.8) * mm});
            skLineSegment(sketch, "E56.15.26", {"start": v(-66.84, 37.09) * mm, "end": v(-66.82, 37.22) * mm});
            skLineSegment(sketch, "E56.15.27", {"start": v(-64.45, 36.8) * mm, "end": v(-64.44, 36.9) * mm});
            skLineSegment(sketch, "E56.15.28", {"start": v(-66.86, 36.94) * mm, "end": v(-66.85, 37) * mm});
            skLineSegment(sketch, "E56.15.29", {"start": v(-66.86, 36.92) * mm, "end": v(-66.86, 36.94) * mm});
            skLineSegment(sketch, "E56.16.0", {"start": v(-71.2, 34.9) * mm, "end": v(-71.6, 36.16) * mm});
            skLineSegment(sketch, "E56.16.1", {"start": v(-70.41, 38.72) * mm, "end": v(-70.7, 39.05) * mm});
            skLineSegment(sketch, "E56.16.2", {"start": v(-69.05, 35.41) * mm, "end": v(-69.26, 36.73) * mm});
            skLineSegment(sketch, "E56.16.3", {"start": v(-70.16, 38.4) * mm, "end": v(-70.41, 38.72) * mm});
            skLineSegment(sketch, "E56.16.4", {"start": v(-71.57, 38.07) * mm, "end": v(-71.48, 38.47) * mm});
            skLineSegment(sketch, "E56.16.5", {"start": v(-71.48, 38.47) * mm, "end": v(-71.37, 38.9) * mm});
            skLineSegment(sketch, "E56.16.6", {"start": v(-69.94, 38.12) * mm, "end": v(-70.16, 38.4) * mm});
            skLineSegment(sketch, "E56.16.7", {"start": v(-71.05, 39.4) * mm, "end": v(-71.43, 39.74) * mm});
            skLineSegment(sketch, "E56.16.8", {"start": v(-69.76, 37.84) * mm, "end": v(-69.94, 38.12) * mm});
            skLineSegment(sketch, "E56.16.9", {"start": v(-71.22, 39.35) * mm, "end": v(-71.04, 39.84) * mm});
            skLineSegment(sketch, "E56.16.10", {"start": v(-70.7, 39.05) * mm, "end": v(-71.05, 39.4) * mm});
            skLineSegment(sketch, "E56.16.11", {"start": v(-71.63, 37.71) * mm, "end": v(-71.57, 38.07) * mm});
            skLineSegment(sketch, "E56.16.12", {"start": v(-71.37, 38.9) * mm, "end": v(-71.22, 39.35) * mm});
            skLineSegment(sketch, "E56.16.13", {"start": v(-69.41, 37.18) * mm, "end": v(-69.5, 37.37) * mm});
            skLineSegment(sketch, "E56.16.14", {"start": v(-69.5, 37.37) * mm, "end": v(-69.62, 37.6) * mm});
            skLineSegment(sketch, "E56.16.15", {"start": v(-69.62, 37.6) * mm, "end": v(-69.76, 37.84) * mm});
            skLineSegment(sketch, "E56.16.16", {"start": v(-71.68, 37.1) * mm, "end": v(-71.66, 37.39) * mm});
            skLineSegment(sketch, "E56.16.17", {"start": v(-71.68, 36.85) * mm, "end": v(-71.68, 37.1) * mm});
            skLineSegment(sketch, "E56.16.18", {"start": v(-71.66, 37.39) * mm, "end": v(-71.63, 37.71) * mm});
            skLineSegment(sketch, "E56.16.19", {"start": v(-69.35, 37.02) * mm, "end": v(-69.41, 37.18) * mm});
            skLineSegment(sketch, "E56.16.20", {"start": v(-69.3, 36.9) * mm, "end": v(-69.35, 37.02) * mm});
            skLineSegment(sketch, "E56.16.21", {"start": v(-71.68, 36.64) * mm, "end": v(-71.68, 36.85) * mm});
            skLineSegment(sketch, "E56.16.22", {"start": v(-71.66, 36.47) * mm, "end": v(-71.68, 36.64) * mm});
            skLineSegment(sketch, "E56.16.23", {"start": v(-71.62, 36.24) * mm, "end": v(-71.64, 36.33) * mm});
            skLineSegment(sketch, "E56.16.24", {"start": v(-69.26, 36.73) * mm, "end": v(-69.26, 36.75) * mm});
            skLineSegment(sketch, "E56.16.25", {"start": v(-69.26, 36.75) * mm, "end": v(-69.28, 36.8) * mm});
            skLineSegment(sketch, "E56.16.26", {"start": v(-71.64, 36.33) * mm, "end": v(-71.66, 36.47) * mm});
            skLineSegment(sketch, "E56.16.27", {"start": v(-69.28, 36.8) * mm, "end": v(-69.3, 36.9) * mm});
            skLineSegment(sketch, "E56.16.28", {"start": v(-71.61, 36.18) * mm, "end": v(-71.62, 36.24) * mm});
            skLineSegment(sketch, "E56.16.29", {"start": v(-71.6, 36.16) * mm, "end": v(-71.61, 36.18) * mm});
            skLineSegment(sketch, "E56.17.0", {"start": v(-75.1, 32.9) * mm, "end": v(-75.9, 33.98) * mm});
            skLineSegment(sketch, "E56.17.1", {"start": v(-75.55, 36.78) * mm, "end": v(-75.93, 37) * mm});
            skLineSegment(sketch, "E56.17.2", {"start": v(-73.23, 34.06) * mm, "end": v(-73.83, 35.24) * mm});
            skLineSegment(sketch, "E56.17.3", {"start": v(-75.2, 36.56) * mm, "end": v(-75.55, 36.78) * mm});
            skLineSegment(sketch, "E56.17.4", {"start": v(-76.44, 35.8) * mm, "end": v(-76.49, 36.2) * mm});
            skLineSegment(sketch, "E56.17.5", {"start": v(-76.49, 36.2) * mm, "end": v(-76.5, 36.65) * mm});
            skLineSegment(sketch, "E56.17.6", {"start": v(-74.91, 36.35) * mm, "end": v(-75.2, 36.56) * mm});
            skLineSegment(sketch, "E56.17.7", {"start": v(-76.36, 37.22) * mm, "end": v(-76.83, 37.44) * mm});
            skLineSegment(sketch, "E56.17.8", {"start": v(-74.66, 36.15) * mm, "end": v(-74.91, 36.35) * mm});
            skLineSegment(sketch, "E56.17.9", {"start": v(-76.51, 37.13) * mm, "end": v(-76.49, 37.65) * mm});
            skLineSegment(sketch, "E56.17.10", {"start": v(-75.93, 37) * mm, "end": v(-76.36, 37.22) * mm});
            skLineSegment(sketch, "E56.17.11", {"start": v(-76.39, 35.45) * mm, "end": v(-76.44, 35.8) * mm});
            skLineSegment(sketch, "E56.17.12", {"start": v(-76.5, 36.65) * mm, "end": v(-76.51, 37.13) * mm});
            skLineSegment(sketch, "E56.17.13", {"start": v(-74.12, 35.63) * mm, "end": v(-74.26, 35.78) * mm});
            skLineSegment(sketch, "E56.17.14", {"start": v(-74.26, 35.78) * mm, "end": v(-74.44, 35.96) * mm});
            skLineSegment(sketch, "E56.17.15", {"start": v(-74.44, 35.96) * mm, "end": v(-74.66, 36.15) * mm});
            skLineSegment(sketch, "E56.17.16", {"start": v(-76.25, 34.85) * mm, "end": v(-76.32, 35.13) * mm});
            skLineSegment(sketch, "E56.17.17", {"start": v(-76.18, 34.6) * mm, "end": v(-76.25, 34.85) * mm});
            skLineSegment(sketch, "E56.17.18", {"start": v(-76.32, 35.13) * mm, "end": v(-76.39, 35.45) * mm});
            skLineSegment(sketch, "E56.17.19", {"start": v(-74, 35.5) * mm, "end": v(-74.12, 35.63) * mm});
            skLineSegment(sketch, "E56.17.20", {"start": v(-73.93, 35.39) * mm, "end": v(-74, 35.5) * mm});
            skLineSegment(sketch, "E56.17.21", {"start": v(-76.1, 34.41) * mm, "end": v(-76.18, 34.6) * mm});
            skLineSegment(sketch, "E56.17.22", {"start": v(-76.04, 34.25) * mm, "end": v(-76.1, 34.41) * mm});
            skLineSegment(sketch, "E56.17.23", {"start": v(-75.93, 34.05) * mm, "end": v(-75.98, 34.13) * mm});
            skLineSegment(sketch, "E56.17.24", {"start": v(-73.83, 35.24) * mm, "end": v(-73.84, 35.26) * mm});
            skLineSegment(sketch, "E56.17.25", {"start": v(-73.84, 35.26) * mm, "end": v(-73.87, 35.3) * mm});
            skLineSegment(sketch, "E56.17.26", {"start": v(-75.98, 34.13) * mm, "end": v(-76.04, 34.25) * mm});
            skLineSegment(sketch, "E56.17.27", {"start": v(-73.87, 35.3) * mm, "end": v(-73.93, 35.39) * mm});
            skLineSegment(sketch, "E56.17.28", {"start": v(-75.9, 34) * mm, "end": v(-75.93, 34.05) * mm});
            skLineSegment(sketch, "E56.17.29", {"start": v(-75.9, 33.98) * mm, "end": v(-75.9, 34) * mm});
            skLineSegment(sketch, "E56.18.0", {"start": v(-78.21, 29.8) * mm, "end": v(-79.3, 30.58) * mm});
            skLineSegment(sketch, "E56.18.1", {"start": v(-79.83, 33.35) * mm, "end": v(-80.26, 33.44) * mm});
            skLineSegment(sketch, "E56.18.2", {"start": v(-76.78, 31.47) * mm, "end": v(-77.72, 32.41) * mm});
            skLineSegment(sketch, "E56.18.3", {"start": v(-79.44, 33.25) * mm, "end": v(-79.83, 33.35) * mm});
            skLineSegment(sketch, "E56.18.4", {"start": v(-80.38, 32.15) * mm, "end": v(-80.55, 32.51) * mm});
            skLineSegment(sketch, "E56.18.5", {"start": v(-80.55, 32.51) * mm, "end": v(-80.7, 32.93) * mm});
            skLineSegment(sketch, "E56.18.6", {"start": v(-79.1, 33.14) * mm, "end": v(-79.44, 33.25) * mm});
            skLineSegment(sketch, "E56.18.7", {"start": v(-80.74, 33.52) * mm, "end": v(-81.25, 33.58) * mm});
            skLineSegment(sketch, "E56.18.8", {"start": v(-78.79, 33.02) * mm, "end": v(-79.1, 33.14) * mm});
            skLineSegment(sketch, "E56.18.9", {"start": v(-80.85, 33.38) * mm, "end": v(-81, 33.88) * mm});
            skLineSegment(sketch, "E56.18.10", {"start": v(-80.26, 33.44) * mm, "end": v(-80.74, 33.52) * mm});
            skLineSegment(sketch, "E56.18.11", {"start": v(-80.22, 31.82) * mm, "end": v(-80.38, 32.15) * mm});
            skLineSegment(sketch, "E56.18.12", {"start": v(-80.7, 32.93) * mm, "end": v(-80.85, 33.38) * mm});
            skLineSegment(sketch, "E56.18.13", {"start": v(-78.11, 32.7) * mm, "end": v(-78.3, 32.8) * mm});
            skLineSegment(sketch, "E56.18.14", {"start": v(-78.3, 32.8) * mm, "end": v(-78.52, 32.9) * mm});
            skLineSegment(sketch, "E56.18.15", {"start": v(-78.52, 32.9) * mm, "end": v(-78.79, 33.02) * mm});
            skLineSegment(sketch, "E56.18.16", {"start": v(-79.9, 31.3) * mm, "end": v(-80.06, 31.54) * mm});
            skLineSegment(sketch, "E56.18.17", {"start": v(-79.76, 31.09) * mm, "end": v(-79.9, 31.3) * mm});
            skLineSegment(sketch, "E56.18.18", {"start": v(-80.06, 31.54) * mm, "end": v(-80.22, 31.82) * mm});
            skLineSegment(sketch, "E56.18.19", {"start": v(-77.97, 32.6) * mm, "end": v(-78.11, 32.7) * mm});
            skLineSegment(sketch, "E56.18.20", {"start": v(-77.86, 32.52) * mm, "end": v(-77.97, 32.6) * mm});
            skLineSegment(sketch, "E56.18.21", {"start": v(-79.63, 30.92) * mm, "end": v(-79.76, 31.09) * mm});
            skLineSegment(sketch, "E56.18.22", {"start": v(-79.51, 30.8) * mm, "end": v(-79.63, 30.92) * mm});
            skLineSegment(sketch, "E56.18.23", {"start": v(-79.35, 30.63) * mm, "end": v(-79.42, 30.7) * mm});
            skLineSegment(sketch, "E56.18.24", {"start": v(-77.72, 32.41) * mm, "end": v(-77.74, 32.43) * mm});
            skLineSegment(sketch, "E56.18.25", {"start": v(-77.74, 32.43) * mm, "end": v(-77.78, 32.47) * mm});
            skLineSegment(sketch, "E56.18.26", {"start": v(-79.42, 30.7) * mm, "end": v(-79.51, 30.8) * mm});
            skLineSegment(sketch, "E56.18.27", {"start": v(-77.78, 32.47) * mm, "end": v(-77.86, 32.52) * mm});
            skLineSegment(sketch, "E56.18.28", {"start": v(-79.3, 30.6) * mm, "end": v(-79.35, 30.63) * mm});
            skLineSegment(sketch, "E56.18.29", {"start": v(-79.3, 30.58) * mm, "end": v(-79.3, 30.6) * mm});
            skLineSegment(sketch, "E56.19.0", {"start": v(-80.2, 25.88) * mm, "end": v(-81.47, 26.3) * mm});
            skLineSegment(sketch, "E56.19.1", {"start": v(-82.84, 28.76) * mm, "end": v(-83.28, 28.72) * mm});
            skLineSegment(sketch, "E56.19.2", {"start": v(-79.36, 27.92) * mm, "end": v(-80.55, 28.52) * mm});
            skLineSegment(sketch, "E56.19.3", {"start": v(-82.44, 28.79) * mm, "end": v(-82.84, 28.76) * mm});
            skLineSegment(sketch, "E56.19.4", {"start": v(-83, 27.45) * mm, "end": v(-83.26, 27.75) * mm});
            skLineSegment(sketch, "E56.19.5", {"start": v(-83.26, 27.75) * mm, "end": v(-83.54, 28.1) * mm});
            skLineSegment(sketch, "E56.19.6", {"start": v(-82.08, 28.79) * mm, "end": v(-82.44, 28.79) * mm});
            skLineSegment(sketch, "E56.19.7", {"start": v(-83.76, 28.64) * mm, "end": v(-84.27, 28.54) * mm});
            skLineSegment(sketch, "E56.19.8", {"start": v(-81.75, 28.77) * mm, "end": v(-82.08, 28.79) * mm});
            skLineSegment(sketch, "E56.19.9", {"start": v(-83.83, 28.48) * mm, "end": v(-84.11, 28.91) * mm});
            skLineSegment(sketch, "E56.19.10", {"start": v(-83.28, 28.72) * mm, "end": v(-83.76, 28.64) * mm});
            skLineSegment(sketch, "E56.19.11", {"start": v(-82.74, 27.19) * mm, "end": v(-83, 27.45) * mm});
            skLineSegment(sketch, "E56.19.12", {"start": v(-83.54, 28.1) * mm, "end": v(-83.83, 28.48) * mm});
            skLineSegment(sketch, "E56.19.13", {"start": v(-81, 28.67) * mm, "end": v(-81.22, 28.7) * mm});
            skLineSegment(sketch, "E56.19.14", {"start": v(-81.22, 28.7) * mm, "end": v(-81.46, 28.75) * mm});
            skLineSegment(sketch, "E56.19.15", {"start": v(-81.46, 28.75) * mm, "end": v(-81.75, 28.77) * mm});
            skLineSegment(sketch, "E56.19.16", {"start": v(-82.27, 26.78) * mm, "end": v(-82.5, 26.97) * mm});
            skLineSegment(sketch, "E56.19.17", {"start": v(-82.07, 26.64) * mm, "end": v(-82.27, 26.78) * mm});
            skLineSegment(sketch, "E56.19.18", {"start": v(-82.5, 26.97) * mm, "end": v(-82.74, 27.19) * mm});
            skLineSegment(sketch, "E56.19.19", {"start": v(-80.84, 28.63) * mm, "end": v(-81, 28.67) * mm});
            skLineSegment(sketch, "E56.19.20", {"start": v(-80.71, 28.59) * mm, "end": v(-80.84, 28.63) * mm});
            skLineSegment(sketch, "E56.19.21", {"start": v(-81.9, 26.52) * mm, "end": v(-82.07, 26.64) * mm});
            skLineSegment(sketch, "E56.19.22", {"start": v(-81.75, 26.43) * mm, "end": v(-81.9, 26.52) * mm});
            skLineSegment(sketch, "E56.19.23", {"start": v(-81.55, 26.32) * mm, "end": v(-81.63, 26.37) * mm});
            skLineSegment(sketch, "E56.19.24", {"start": v(-80.55, 28.52) * mm, "end": v(-80.57, 28.53) * mm});
            skLineSegment(sketch, "E56.19.25", {"start": v(-80.57, 28.53) * mm, "end": v(-80.62, 28.55) * mm});
            skLineSegment(sketch, "E56.19.26", {"start": v(-81.63, 26.37) * mm, "end": v(-81.75, 26.43) * mm});
            skLineSegment(sketch, "E56.19.27", {"start": v(-80.62, 28.55) * mm, "end": v(-80.71, 28.59) * mm});
            skLineSegment(sketch, "E56.19.28", {"start": v(-81.5, 26.3) * mm, "end": v(-81.55, 26.32) * mm});
            skLineSegment(sketch, "E56.19.29", {"start": v(-81.47, 26.3) * mm, "end": v(-81.5, 26.3) * mm});
            skSolve(sketch);
        }
        {
            var Q0;
            {var subQ2=sQuery(id+"F0.wireOp",EDGE,"E56.11.0");Q0=makeQuery(id+"F0.imprint","IMPRINT",FACE,{"disambiguationData":[TD([[makeQuery(id+"F0.imprint","IMPRINT",EDGE,{"derivedFrom":subQ2}),-1.0]])]});}
            var Q1;
            {var subQ2=sQuery(id+"F0.wireOp",EDGE,"E56.12.0");Q1=makeQuery(id+"F0.imprint","IMPRINT",FACE,{"disambiguationData":[TD([[makeQuery(id+"F0.imprint","IMPRINT",EDGE,{"derivedFrom":subQ2}),-1.0]])]});}
            var Q2;
            {var subQ7=sQuery(id+"F0.wireOp",EDGE,"E56.13.0");Q2=makeQuery(id+"F0.imprint","IMPRINT",FACE,{"disambiguationData":[TD([[makeQuery(id+"F0.imprint","IMPRINT",EDGE,{"derivedFrom":subQ7}),-1.0]])]});}
            var Q3;
            {var subQ7=sQuery(id+"F0.wireOp",EDGE,"E56.14.0");Q3=makeQuery(id+"F0.imprint","IMPRINT",FACE,{"disambiguationData":[TD([[makeQuery(id+"F0.imprint","IMPRINT",EDGE,{"derivedFrom":subQ7}),-1.0]])]});}
            var Q4;
            {var subQ2=sQuery(id+"F0.wireOp",EDGE,"E56.15.0");Q4=makeQuery(id+"F0.imprint","IMPRINT",FACE,{"disambiguationData":[TD([[makeQuery(id+"F0.imprint","IMPRINT",EDGE,{"derivedFrom":subQ2}),-1.0]])]});}
            var Q5;
            {var subQ6=sQuery(id+"F0.wireOp",EDGE,"E56.16.0");Q5=makeQuery(id+"F0.imprint","IMPRINT",FACE,{"disambiguationData":[TD([[makeQuery(id+"F0.imprint","IMPRINT",EDGE,{"derivedFrom":subQ6}),-1.0]])]});}
            var Q6;
            {var subQ2=sQuery(id+"F0.wireOp",EDGE,"E56.17.0");Q6=makeQuery(id+"F0.imprint","IMPRINT",FACE,{"disambiguationData":[TD([[makeQuery(id+"F0.imprint","IMPRINT",EDGE,{"derivedFrom":subQ2}),-1.0]])]});}
            var Q7;
            {var subQ0=sQuery(id+"F0.wireOp",EDGE,"E56.18.0");Q7=makeQuery(id+"F0.imprint","IMPRINT",FACE,{"disambiguationData":[TD([[makeQuery(id+"F0.imprint","IMPRINT",EDGE,{"derivedFrom":subQ0}),-1.0]])]});}
            var Q8;
            {var subQ2=sQuery(id+"F0.wireOp",EDGE,"E56.19.0");Q8=makeQuery(id+"F0.imprint","IMPRINT",FACE,{"disambiguationData":[TD([[makeQuery(id+"F0.imprint","IMPRINT",EDGE,{"derivedFrom":subQ2}),-1.0]])]});}
            var Q9;
            {var subQ2=sQuery(id+"F0.wireOp",EDGE,"E56.1.0");Q9=makeQuery(id+"F0.imprint","IMPRINT",FACE,{"disambiguationData":[TD([[makeQuery(id+"F0.imprint","IMPRINT",EDGE,{"derivedFrom":subQ2}),-1.0]])]});}
            var Q10;
            {var subQ7=sQuery(id+"F0.wireOp",EDGE,"E56.8.0");Q10=makeQuery(id+"F0.imprint","IMPRINT",FACE,{"disambiguationData":[TD([[makeQuery(id+"F0.imprint","IMPRINT",EDGE,{"derivedFrom":subQ7}),-1.0]])]});}
            var Q11;
            {var subQ2=sQuery(id+"F0.wireOp",EDGE,"E56.9.0");Q11=makeQuery(id+"F0.imprint","IMPRINT",FACE,{"disambiguationData":[TD([[makeQuery(id+"F0.imprint","IMPRINT",EDGE,{"derivedFrom":subQ2}),-1.0]])]});}
            var Q12;
            {var subQ1=sQuery(id+"F0.wireOp",EDGE,"E56.10.0");Q12=makeQuery(id+"F0.imprint","IMPRINT",FACE,{"disambiguationData":[TD([[makeQuery(id+"F0.imprint","IMPRINT",EDGE,{"derivedFrom":subQ1}),-1.0]])]});}
            var Q13;
            {var subQ0=sQuery(id+"F0.wireOp",EDGE,"E5");var subQ18=makeQuery(id+"F0.imprint","INTERSECT",VERTEX,{"derivedFrom":[subQ0,sQuery(id+"F0.wireOp",EDGE,"E56.10.0")]});Q13=makeQuery(id+"F0.imprint","IMPRINT",FACE,{"disambiguationData":[TD([[makeQuery(id+"F0.imprint","IMPRINT",EDGE,{"disambiguationData":[TD([[subQ18,-1.0]])],"derivedFrom":subQ0}),1.0]])]});}
            var Q14;
            {var subQ2=sQuery(id+"F0.wireOp",EDGE,"E56.7.0");Q14=makeQuery(id+"F0.imprint","IMPRINT",FACE,{"disambiguationData":[TD([[makeQuery(id+"F0.imprint","IMPRINT",EDGE,{"derivedFrom":subQ2}),-1.0]])]});}
            var Q15;
            {var subQ2=sQuery(id+"F0.wireOp",EDGE,"E56.6.0");Q15=makeQuery(id+"F0.imprint","IMPRINT",FACE,{"disambiguationData":[TD([[makeQuery(id+"F0.imprint","IMPRINT",EDGE,{"derivedFrom":subQ2}),-1.0]])]});}
            var Q16;
            {var subQ0=sQuery(id+"F0.wireOp",EDGE,"E56.5.0");Q16=makeQuery(id+"F0.imprint","IMPRINT",FACE,{"disambiguationData":[TD([[makeQuery(id+"F0.imprint","IMPRINT",EDGE,{"derivedFrom":subQ0}),-1.0]])]});}
            var Q17;
            {var subQ2=sQuery(id+"F0.wireOp",EDGE,"E56.4.0");Q17=makeQuery(id+"F0.imprint","IMPRINT",FACE,{"disambiguationData":[TD([[makeQuery(id+"F0.imprint","IMPRINT",EDGE,{"derivedFrom":subQ2}),-1.0]])]});}
            var Q18;
            {var subQ2=sQuery(id+"F0.wireOp",EDGE,"E56.3.0");Q18=makeQuery(id+"F0.imprint","IMPRINT",FACE,{"disambiguationData":[TD([[makeQuery(id+"F0.imprint","IMPRINT",EDGE,{"derivedFrom":subQ2}),-1.0]])]});}
            var Q19;
            {var subQ0=sQuery(id+"F0.wireOp",EDGE,"E56.2.0");Q19=makeQuery(id+"F0.imprint","IMPRINT",FACE,{"disambiguationData":[TD([[makeQuery(id+"F0.imprint","IMPRINT",EDGE,{"derivedFrom":subQ0}),-1.0]])]});}
            var Q20;
            {var subQ4=sQuery(id+"F0.wireOp",EDGE,"E26");Q20=makeQuery(id+"F0.imprint","IMPRINT",FACE,{"disambiguationData":[TD([[makeQuery(id+"F0.imprint","IMPRINT",EDGE,{"derivedFrom":subQ4}),-1.0]])]});}
            var Q21;
            {var subQ1=sQuery(id+"F0.wireOp",EDGE,"E56.16.1");Q21=makeQuery(id+"F0.imprint","IMPRINT",FACE,{"disambiguationData":[TD([[makeQuery(id+"F0.imprint","IMPRINT",EDGE,{"derivedFrom":subQ1}),1.0]])]});}
            var Q22;
            {var subQ1=sQuery(id+"F0.wireOp",EDGE,"E56.1.1");Q22=makeQuery(id+"F0.imprint","IMPRINT",FACE,{"disambiguationData":[TD([[makeQuery(id+"F0.imprint","IMPRINT",EDGE,{"derivedFrom":subQ1}),1.0]])]});}
            var Q23;
            {var subQ1=sQuery(id+"F0.wireOp",EDGE,"E56.5.1");Q23=makeQuery(id+"F0.imprint","IMPRINT",FACE,{"disambiguationData":[TD([[makeQuery(id+"F0.imprint","IMPRINT",EDGE,{"derivedFrom":subQ1}),1.0]])]});}
            var Q24;
            {var subQ1=sQuery(id+"F0.wireOp",EDGE,"E56.6.1");Q24=makeQuery(id+"F0.imprint","IMPRINT",FACE,{"disambiguationData":[TD([[makeQuery(id+"F0.imprint","IMPRINT",EDGE,{"derivedFrom":subQ1}),1.0]])]});}
            var Q25;
            {var subQ1=sQuery(id+"F0.wireOp",EDGE,"E56.11.1");Q25=makeQuery(id+"F0.imprint","IMPRINT",FACE,{"disambiguationData":[TD([[makeQuery(id+"F0.imprint","IMPRINT",EDGE,{"derivedFrom":subQ1}),1.0]])]});}
            var Q26;
            {var subQ1=sQuery(id+"F0.wireOp",EDGE,"E56.12.1");Q26=makeQuery(id+"F0.imprint","IMPRINT",FACE,{"disambiguationData":[TD([[makeQuery(id+"F0.imprint","IMPRINT",EDGE,{"derivedFrom":subQ1}),1.0]])]});}
            var Q27;
            {var subQ1=sQuery(id+"F0.wireOp",EDGE,"E56.13.1");Q27=makeQuery(id+"F0.imprint","IMPRINT",FACE,{"disambiguationData":[TD([[makeQuery(id+"F0.imprint","IMPRINT",EDGE,{"derivedFrom":subQ1}),1.0]])]});}
            var Q28;
            {var subQ1=sQuery(id+"F0.wireOp",EDGE,"E56.14.1");Q28=makeQuery(id+"F0.imprint","IMPRINT",FACE,{"disambiguationData":[TD([[makeQuery(id+"F0.imprint","IMPRINT",EDGE,{"derivedFrom":subQ1}),1.0]])]});}
            var Q29;
            {var subQ1=sQuery(id+"F0.wireOp",EDGE,"E56.2.1");Q29=makeQuery(id+"F0.imprint","IMPRINT",FACE,{"disambiguationData":[TD([[makeQuery(id+"F0.imprint","IMPRINT",EDGE,{"derivedFrom":subQ1}),1.0]])]});}
            var Q30;
            {var subQ1=sQuery(id+"F0.wireOp",EDGE,"E56.3.1");Q30=makeQuery(id+"F0.imprint","IMPRINT",FACE,{"disambiguationData":[TD([[makeQuery(id+"F0.imprint","IMPRINT",EDGE,{"derivedFrom":subQ1}),1.0]])]});}
            var Q31;
            {var subQ1=sQuery(id+"F0.wireOp",EDGE,"E56.4.1");Q31=makeQuery(id+"F0.imprint","IMPRINT",FACE,{"disambiguationData":[TD([[makeQuery(id+"F0.imprint","IMPRINT",EDGE,{"derivedFrom":subQ1}),1.0]])]});}
            var Q32;
            {var subQ1=sQuery(id+"F0.wireOp",EDGE,"E56.10.1");Q32=makeQuery(id+"F0.imprint","IMPRINT",FACE,{"disambiguationData":[TD([[makeQuery(id+"F0.imprint","IMPRINT",EDGE,{"derivedFrom":subQ1}),1.0]])]});}
            var Q33;
            {var subQ1=sQuery(id+"F0.wireOp",EDGE,"E56.7.1");Q33=makeQuery(id+"F0.imprint","IMPRINT",FACE,{"disambiguationData":[TD([[makeQuery(id+"F0.imprint","IMPRINT",EDGE,{"derivedFrom":subQ1}),1.0]])]});}
            var Q34;
            {var subQ1=sQuery(id+"F0.wireOp",EDGE,"E56.15.1");Q34=makeQuery(id+"F0.imprint","IMPRINT",FACE,{"disambiguationData":[TD([[makeQuery(id+"F0.imprint","IMPRINT",EDGE,{"derivedFrom":subQ1}),1.0]])]});}
            var Q35;
            {var subQ1=sQuery(id+"F0.wireOp",EDGE,"E56.17.1");Q35=makeQuery(id+"F0.imprint","IMPRINT",FACE,{"disambiguationData":[TD([[makeQuery(id+"F0.imprint","IMPRINT",EDGE,{"derivedFrom":subQ1}),1.0]])]});}
            var Q36;
            {var subQ1=sQuery(id+"F0.wireOp",EDGE,"E56.18.1");Q36=makeQuery(id+"F0.imprint","IMPRINT",FACE,{"disambiguationData":[TD([[makeQuery(id+"F0.imprint","IMPRINT",EDGE,{"derivedFrom":subQ1}),1.0]])]});}
            var Q37;
            {var subQ1=sQuery(id+"F0.wireOp",EDGE,"E56.19.1");Q37=makeQuery(id+"F0.imprint","IMPRINT",FACE,{"disambiguationData":[TD([[makeQuery(id+"F0.imprint","IMPRINT",EDGE,{"derivedFrom":subQ1}),1.0]])]});}
            var Q38;
            {var subQ5=sQuery(id+"F0.wireOp",EDGE,"E39");Q38=makeQuery(id+"F0.imprint","IMPRINT",FACE,{"disambiguationData":[TD([[makeQuery(id+"F0.imprint","IMPRINT",EDGE,{"derivedFrom":subQ5}),-1.0]])]});}
            var Q39;
            {var subQ1=sQuery(id+"F0.wireOp",EDGE,"E56.9.1");Q39=makeQuery(id+"F0.imprint","IMPRINT",FACE,{"disambiguationData":[TD([[makeQuery(id+"F0.imprint","IMPRINT",EDGE,{"derivedFrom":subQ1}),1.0]])]});}
            var Q40;
            {var subQ1=sQuery(id+"F0.wireOp",EDGE,"E56.8.1");Q40=makeQuery(id+"F0.imprint","IMPRINT",FACE,{"disambiguationData":[TD([[makeQuery(id+"F0.imprint","IMPRINT",EDGE,{"derivedFrom":subQ1}),1.0]])]});}
            extrude(context, id + "F1", {"entities" : qUnion([Q0, Q1, Q2, Q3, Q4, Q5, Q6, Q7, Q8, Q9, Q10, Q11, Q12, Q13, Q14, Q15, Q16, Q17, Q18, Q19, Q20, Q21, Q22, Q23, Q24, Q25, Q26, Q27, Q28, Q29, Q30, Q31, Q32, Q33, Q34, Q35, Q36, Q37, Q38, Q39, Q40]), "depth" : 6.35 * mm, "offsetDistance" : 25.4 * mm});
        }
        {
            var Q0;
            Q0=makeQuery(id+"F0.imprint","IMPRINT",FACE,{"disambiguationData":[TD([[makeQuery(id+"F0.imprint","IMPRINT",EDGE,{"derivedFrom":sQuery(id+"F0.wireOp",EDGE,"E1")}),1.0]])]});
            var Q1;
            Q1=makeQuery(id+"F0.imprint","IMPRINT",FACE,{"disambiguationData":[TD([[makeQuery(id+"F0.imprint","IMPRINT",EDGE,{"derivedFrom":sQuery(id+"F0.wireOp",EDGE,"E4")}),1.0]])]});
            extrude(context, id + "F2", {"entities" : qUnion([Q0, Q1]), "depth" : 6.35 * mm, "offsetDistance" : 25.4 * mm});
        }
        {
            var Q0;
            Q0=makeQuery(id+"F1.opExtrude","SWEPT_BODY",BODY,{"disambiguationData":[OSD([sQuery(id+"F0.wireOp",EDGE,"E5"),sQuery(id+"F0.wireOp",EDGE,"E26"),sQuery(id+"F0.wireOp",EDGE,"E27.MirrorCS"),sQuery(id+"F0.wireOp",EDGE,"E28"),sQuery(id+"F0.wireOp",EDGE,"E29"),sQuery(id+"F0.wireOp",EDGE,"E30"),sQuery(id+"F0.wireOp",EDGE,"E31"),sQuery(id+"F0.wireOp",EDGE,"E32"),sQuery(id+"F0.wireOp",EDGE,"E33"),sQuery(id+"F0.wireOp",EDGE,"E34"),sQuery(id+"F0.wireOp",EDGE,"E35"),sQuery(id+"F0.wireOp",EDGE,"E36"),sQuery(id+"F0.wireOp",EDGE,"E37"),sQuery(id+"F0.wireOp",EDGE,"E38"),sQuery(id+"F0.wireOp",EDGE,"E39"),sQuery(id+"F0.wireOp",EDGE,"E40"),sQuery(id+"F0.wireOp",EDGE,"E41"),sQuery(id+"F0.wireOp",EDGE,"E42.MirrorCS"),sQuery(id+"F0.wireOp",EDGE,"E43.MirrorCS"),sQuery(id+"F0.wireOp",EDGE,"E44.MirrorCS"),sQuery(id+"F0.wireOp",EDGE,"E45.MirrorCS"),sQuery(id+"F0.wireOp",EDGE,"E46.MirrorCS"),sQuery(id+"F0.wireOp",EDGE,"E47.MirrorCS"),sQuery(id+"F0.wireOp",EDGE,"E48.MirrorCS"),sQuery(id+"F0.wireOp",EDGE,"E49.MirrorCS"),sQuery(id+"F0.wireOp",EDGE,"E50.MirrorCS"),sQuery(id+"F0.wireOp",EDGE,"E51.MirrorCS"),sQuery(id+"F0.wireOp",EDGE,"E52.MirrorCS"),sQuery(id+"F0.wireOp",EDGE,"E53.MirrorCS"),sQuery(id+"F0.wireOp",EDGE,"E54.MirrorCS"),sQuery(id+"F0.wireOp",EDGE,"E55.MirrorCS"),sQuery(id+"F0.wireOp",EDGE,"E56.1.0"),sQuery(id+"F0.wireOp",EDGE,"E56.1.1"),sQuery(id+"F0.wireOp",EDGE,"E56.1.2"),sQuery(id+"F0.wireOp",EDGE,"E56.1.3"),sQuery(id+"F0.wireOp",EDGE,"E56.1.4"),sQuery(id+"F0.wireOp",EDGE,"E56.1.5"),sQuery(id+"F0.wireOp",EDGE,"E56.1.6"),sQuery(id+"F0.wireOp",EDGE,"E56.1.7"),sQuery(id+"F0.wireOp",EDGE,"E56.1.8"),sQuery(id+"F0.wireOp",EDGE,"E56.1.9"),sQuery(id+"F0.wireOp",EDGE,"E56.1.10"),sQuery(id+"F0.wireOp",EDGE,"E56.1.11"),sQuery(id+"F0.wireOp",EDGE,"E56.1.12"),sQuery(id+"F0.wireOp",EDGE,"E56.1.13"),sQuery(id+"F0.wireOp",EDGE,"E56.1.14"),sQuery(id+"F0.wireOp",EDGE,"E56.1.15"),sQuery(id+"F0.wireOp",EDGE,"E56.1.16"),sQuery(id+"F0.wireOp",EDGE,"E56.1.17"),sQuery(id+"F0.wireOp",EDGE,"E56.1.18"),sQuery(id+"F0.wireOp",EDGE,"E56.1.19"),sQuery(id+"F0.wireOp",EDGE,"E56.1.20"),sQuery(id+"F0.wireOp",EDGE,"E56.1.21"),sQuery(id+"F0.wireOp",EDGE,"E56.1.22"),sQuery(id+"F0.wireOp",EDGE,"E56.1.23"),sQuery(id+"F0.wireOp",EDGE,"E56.1.24"),sQuery(id+"F0.wireOp",EDGE,"E56.1.25"),sQuery(id+"F0.wireOp",EDGE,"E56.1.26"),sQuery(id+"F0.wireOp",EDGE,"E56.1.27"),sQuery(id+"F0.wireOp",EDGE,"E56.1.28"),sQuery(id+"F0.wireOp",EDGE,"E56.1.29"),sQuery(id+"F0.wireOp",EDGE,"E56.2.0"),sQuery(id+"F0.wireOp",EDGE,"E56.2.1"),sQuery(id+"F0.wireOp",EDGE,"E56.2.2"),sQuery(id+"F0.wireOp",EDGE,"E56.2.3"),sQuery(id+"F0.wireOp",EDGE,"E56.2.4"),sQuery(id+"F0.wireOp",EDGE,"E56.2.5"),sQuery(id+"F0.wireOp",EDGE,"E56.2.6"),sQuery(id+"F0.wireOp",EDGE,"E56.2.7"),sQuery(id+"F0.wireOp",EDGE,"E56.2.8"),sQuery(id+"F0.wireOp",EDGE,"E56.2.9"),sQuery(id+"F0.wireOp",EDGE,"E56.2.10"),sQuery(id+"F0.wireOp",EDGE,"E56.2.11"),sQuery(id+"F0.wireOp",EDGE,"E56.2.12"),sQuery(id+"F0.wireOp",EDGE,"E56.2.13"),sQuery(id+"F0.wireOp",EDGE,"E56.2.14"),sQuery(id+"F0.wireOp",EDGE,"E56.2.15"),sQuery(id+"F0.wireOp",EDGE,"E56.2.16"),sQuery(id+"F0.wireOp",EDGE,"E56.2.17"),sQuery(id+"F0.wireOp",EDGE,"E56.2.18"),sQuery(id+"F0.wireOp",EDGE,"E56.2.19"),sQuery(id+"F0.wireOp",EDGE,"E56.2.20"),sQuery(id+"F0.wireOp",EDGE,"E56.2.21"),sQuery(id+"F0.wireOp",EDGE,"E56.2.22"),sQuery(id+"F0.wireOp",EDGE,"E56.2.23"),sQuery(id+"F0.wireOp",EDGE,"E56.2.24"),sQuery(id+"F0.wireOp",EDGE,"E56.2.25"),sQuery(id+"F0.wireOp",EDGE,"E56.2.26"),sQuery(id+"F0.wireOp",EDGE,"E56.2.27"),sQuery(id+"F0.wireOp",EDGE,"E56.2.28"),sQuery(id+"F0.wireOp",EDGE,"E56.2.29"),sQuery(id+"F0.wireOp",EDGE,"E56.3.0"),sQuery(id+"F0.wireOp",EDGE,"E56.3.1"),sQuery(id+"F0.wireOp",EDGE,"E56.3.2"),sQuery(id+"F0.wireOp",EDGE,"E56.3.3"),sQuery(id+"F0.wireOp",EDGE,"E56.3.4"),sQuery(id+"F0.wireOp",EDGE,"E56.3.5"),sQuery(id+"F0.wireOp",EDGE,"E56.3.6"),sQuery(id+"F0.wireOp",EDGE,"E56.3.7"),sQuery(id+"F0.wireOp",EDGE,"E56.3.8"),sQuery(id+"F0.wireOp",EDGE,"E56.3.9"),sQuery(id+"F0.wireOp",EDGE,"E56.3.10"),sQuery(id+"F0.wireOp",EDGE,"E56.3.11"),sQuery(id+"F0.wireOp",EDGE,"E56.3.12"),sQuery(id+"F0.wireOp",EDGE,"E56.3.13"),sQuery(id+"F0.wireOp",EDGE,"E56.3.14"),sQuery(id+"F0.wireOp",EDGE,"E56.3.15"),sQuery(id+"F0.wireOp",EDGE,"E56.3.16"),sQuery(id+"F0.wireOp",EDGE,"E56.3.17"),sQuery(id+"F0.wireOp",EDGE,"E56.3.18"),sQuery(id+"F0.wireOp",EDGE,"E56.3.19"),sQuery(id+"F0.wireOp",EDGE,"E56.3.20"),sQuery(id+"F0.wireOp",EDGE,"E56.3.21"),sQuery(id+"F0.wireOp",EDGE,"E56.3.22"),sQuery(id+"F0.wireOp",EDGE,"E56.3.23"),sQuery(id+"F0.wireOp",EDGE,"E56.3.24"),sQuery(id+"F0.wireOp",EDGE,"E56.3.25"),sQuery(id+"F0.wireOp",EDGE,"E56.3.26"),sQuery(id+"F0.wireOp",EDGE,"E56.3.27"),sQuery(id+"F0.wireOp",EDGE,"E56.3.28"),sQuery(id+"F0.wireOp",EDGE,"E56.3.29"),sQuery(id+"F0.wireOp",EDGE,"E56.4.0"),sQuery(id+"F0.wireOp",EDGE,"E56.4.1"),sQuery(id+"F0.wireOp",EDGE,"E56.4.2"),sQuery(id+"F0.wireOp",EDGE,"E56.4.3"),sQuery(id+"F0.wireOp",EDGE,"E56.4.4"),sQuery(id+"F0.wireOp",EDGE,"E56.4.5"),sQuery(id+"F0.wireOp",EDGE,"E56.4.6"),sQuery(id+"F0.wireOp",EDGE,"E56.4.7"),sQuery(id+"F0.wireOp",EDGE,"E56.4.8"),sQuery(id+"F0.wireOp",EDGE,"E56.4.9"),sQuery(id+"F0.wireOp",EDGE,"E56.4.10"),sQuery(id+"F0.wireOp",EDGE,"E56.4.11"),sQuery(id+"F0.wireOp",EDGE,"E56.4.12"),sQuery(id+"F0.wireOp",EDGE,"E56.4.13"),sQuery(id+"F0.wireOp",EDGE,"E56.4.14"),sQuery(id+"F0.wireOp",EDGE,"E56.4.15"),sQuery(id+"F0.wireOp",EDGE,"E56.4.16"),sQuery(id+"F0.wireOp",EDGE,"E56.4.17"),sQuery(id+"F0.wireOp",EDGE,"E56.4.18"),sQuery(id+"F0.wireOp",EDGE,"E56.4.19"),sQuery(id+"F0.wireOp",EDGE,"E56.4.20"),sQuery(id+"F0.wireOp",EDGE,"E56.4.21"),sQuery(id+"F0.wireOp",EDGE,"E56.4.22"),sQuery(id+"F0.wireOp",EDGE,"E56.4.23"),sQuery(id+"F0.wireOp",EDGE,"E56.4.24"),sQuery(id+"F0.wireOp",EDGE,"E56.4.25"),sQuery(id+"F0.wireOp",EDGE,"E56.4.26"),sQuery(id+"F0.wireOp",EDGE,"E56.4.27"),sQuery(id+"F0.wireOp",EDGE,"E56.4.28"),sQuery(id+"F0.wireOp",EDGE,"E56.4.29"),sQuery(id+"F0.wireOp",EDGE,"E56.5.0"),sQuery(id+"F0.wireOp",EDGE,"E56.5.1"),sQuery(id+"F0.wireOp",EDGE,"E56.5.2"),sQuery(id+"F0.wireOp",EDGE,"E56.5.3"),sQuery(id+"F0.wireOp",EDGE,"E56.5.4"),sQuery(id+"F0.wireOp",EDGE,"E56.5.5"),sQuery(id+"F0.wireOp",EDGE,"E56.5.6"),sQuery(id+"F0.wireOp",EDGE,"E56.5.7"),sQuery(id+"F0.wireOp",EDGE,"E56.5.8"),sQuery(id+"F0.wireOp",EDGE,"E56.5.9"),sQuery(id+"F0.wireOp",EDGE,"E56.5.10"),sQuery(id+"F0.wireOp",EDGE,"E56.5.11"),sQuery(id+"F0.wireOp",EDGE,"E56.5.12"),sQuery(id+"F0.wireOp",EDGE,"E56.5.13"),sQuery(id+"F0.wireOp",EDGE,"E56.5.14"),sQuery(id+"F0.wireOp",EDGE,"E56.5.15"),sQuery(id+"F0.wireOp",EDGE,"E56.5.16"),sQuery(id+"F0.wireOp",EDGE,"E56.5.17"),sQuery(id+"F0.wireOp",EDGE,"E56.5.18"),sQuery(id+"F0.wireOp",EDGE,"E56.5.19"),sQuery(id+"F0.wireOp",EDGE,"E56.5.20"),sQuery(id+"F0.wireOp",EDGE,"E56.5.21"),sQuery(id+"F0.wireOp",EDGE,"E56.5.22"),sQuery(id+"F0.wireOp",EDGE,"E56.5.23"),sQuery(id+"F0.wireOp",EDGE,"E56.5.24"),sQuery(id+"F0.wireOp",EDGE,"E56.5.25"),sQuery(id+"F0.wireOp",EDGE,"E56.5.26"),sQuery(id+"F0.wireOp",EDGE,"E56.5.27"),sQuery(id+"F0.wireOp",EDGE,"E56.5.28"),sQuery(id+"F0.wireOp",EDGE,"E56.5.29"),sQuery(id+"F0.wireOp",EDGE,"E56.6.0"),sQuery(id+"F0.wireOp",EDGE,"E56.6.1"),sQuery(id+"F0.wireOp",EDGE,"E56.6.2"),sQuery(id+"F0.wireOp",EDGE,"E56.6.3"),sQuery(id+"F0.wireOp",EDGE,"E56.6.4"),sQuery(id+"F0.wireOp",EDGE,"E56.6.5"),sQuery(id+"F0.wireOp",EDGE,"E56.6.6"),sQuery(id+"F0.wireOp",EDGE,"E56.6.7"),sQuery(id+"F0.wireOp",EDGE,"E56.6.8"),sQuery(id+"F0.wireOp",EDGE,"E56.6.9"),sQuery(id+"F0.wireOp",EDGE,"E56.6.10"),sQuery(id+"F0.wireOp",EDGE,"E56.6.11"),sQuery(id+"F0.wireOp",EDGE,"E56.6.12"),sQuery(id+"F0.wireOp",EDGE,"E56.6.13"),sQuery(id+"F0.wireOp",EDGE,"E56.6.14"),sQuery(id+"F0.wireOp",EDGE,"E56.6.15"),sQuery(id+"F0.wireOp",EDGE,"E56.6.16"),sQuery(id+"F0.wireOp",EDGE,"E56.6.17"),sQuery(id+"F0.wireOp",EDGE,"E56.6.18"),sQuery(id+"F0.wireOp",EDGE,"E56.6.19"),sQuery(id+"F0.wireOp",EDGE,"E56.6.20"),sQuery(id+"F0.wireOp",EDGE,"E56.6.21"),sQuery(id+"F0.wireOp",EDGE,"E56.6.22"),sQuery(id+"F0.wireOp",EDGE,"E56.6.23"),sQuery(id+"F0.wireOp",EDGE,"E56.6.24"),sQuery(id+"F0.wireOp",EDGE,"E56.6.25"),sQuery(id+"F0.wireOp",EDGE,"E56.6.26"),sQuery(id+"F0.wireOp",EDGE,"E56.6.27"),sQuery(id+"F0.wireOp",EDGE,"E56.6.28"),sQuery(id+"F0.wireOp",EDGE,"E56.6.29"),sQuery(id+"F0.wireOp",EDGE,"E56.7.0"),sQuery(id+"F0.wireOp",EDGE,"E56.7.1"),sQuery(id+"F0.wireOp",EDGE,"E56.7.2"),sQuery(id+"F0.wireOp",EDGE,"E56.7.3"),sQuery(id+"F0.wireOp",EDGE,"E56.7.4"),sQuery(id+"F0.wireOp",EDGE,"E56.7.5"),sQuery(id+"F0.wireOp",EDGE,"E56.7.6"),sQuery(id+"F0.wireOp",EDGE,"E56.7.7"),sQuery(id+"F0.wireOp",EDGE,"E56.7.8"),sQuery(id+"F0.wireOp",EDGE,"E56.7.9"),sQuery(id+"F0.wireOp",EDGE,"E56.7.10"),sQuery(id+"F0.wireOp",EDGE,"E56.7.11"),sQuery(id+"F0.wireOp",EDGE,"E56.7.12"),sQuery(id+"F0.wireOp",EDGE,"E56.7.13"),sQuery(id+"F0.wireOp",EDGE,"E56.7.14"),sQuery(id+"F0.wireOp",EDGE,"E56.7.15"),sQuery(id+"F0.wireOp",EDGE,"E56.7.16"),sQuery(id+"F0.wireOp",EDGE,"E56.7.17"),sQuery(id+"F0.wireOp",EDGE,"E56.7.18"),sQuery(id+"F0.wireOp",EDGE,"E56.7.19"),sQuery(id+"F0.wireOp",EDGE,"E56.7.20"),sQuery(id+"F0.wireOp",EDGE,"E56.7.21"),sQuery(id+"F0.wireOp",EDGE,"E56.7.22"),sQuery(id+"F0.wireOp",EDGE,"E56.7.23"),sQuery(id+"F0.wireOp",EDGE,"E56.7.24"),sQuery(id+"F0.wireOp",EDGE,"E56.7.25"),sQuery(id+"F0.wireOp",EDGE,"E56.7.26"),sQuery(id+"F0.wireOp",EDGE,"E56.7.27"),sQuery(id+"F0.wireOp",EDGE,"E56.7.28"),sQuery(id+"F0.wireOp",EDGE,"E56.7.29"),sQuery(id+"F0.wireOp",EDGE,"E56.8.0"),sQuery(id+"F0.wireOp",EDGE,"E56.8.1"),sQuery(id+"F0.wireOp",EDGE,"E56.8.2"),sQuery(id+"F0.wireOp",EDGE,"E56.8.3"),sQuery(id+"F0.wireOp",EDGE,"E56.8.4"),sQuery(id+"F0.wireOp",EDGE,"E56.8.5"),sQuery(id+"F0.wireOp",EDGE,"E56.8.6"),sQuery(id+"F0.wireOp",EDGE,"E56.8.7"),sQuery(id+"F0.wireOp",EDGE,"E56.8.8"),sQuery(id+"F0.wireOp",EDGE,"E56.8.9"),sQuery(id+"F0.wireOp",EDGE,"E56.8.10"),sQuery(id+"F0.wireOp",EDGE,"E56.8.11"),sQuery(id+"F0.wireOp",EDGE,"E56.8.12"),sQuery(id+"F0.wireOp",EDGE,"E56.8.13"),sQuery(id+"F0.wireOp",EDGE,"E56.8.14"),sQuery(id+"F0.wireOp",EDGE,"E56.8.15"),sQuery(id+"F0.wireOp",EDGE,"E56.8.16"),sQuery(id+"F0.wireOp",EDGE,"E56.8.17"),sQuery(id+"F0.wireOp",EDGE,"E56.8.18"),sQuery(id+"F0.wireOp",EDGE,"E56.8.19"),sQuery(id+"F0.wireOp",EDGE,"E56.8.20"),sQuery(id+"F0.wireOp",EDGE,"E56.8.21"),sQuery(id+"F0.wireOp",EDGE,"E56.8.22"),sQuery(id+"F0.wireOp",EDGE,"E56.8.23"),sQuery(id+"F0.wireOp",EDGE,"E56.8.24"),sQuery(id+"F0.wireOp",EDGE,"E56.8.25"),sQuery(id+"F0.wireOp",EDGE,"E56.8.26"),sQuery(id+"F0.wireOp",EDGE,"E56.8.27"),sQuery(id+"F0.wireOp",EDGE,"E56.8.28"),sQuery(id+"F0.wireOp",EDGE,"E56.8.29"),sQuery(id+"F0.wireOp",EDGE,"E56.9.0"),sQuery(id+"F0.wireOp",EDGE,"E56.9.1"),sQuery(id+"F0.wireOp",EDGE,"E56.9.2"),sQuery(id+"F0.wireOp",EDGE,"E56.9.3"),sQuery(id+"F0.wireOp",EDGE,"E56.9.4"),sQuery(id+"F0.wireOp",EDGE,"E56.9.5"),sQuery(id+"F0.wireOp",EDGE,"E56.9.6"),sQuery(id+"F0.wireOp",EDGE,"E56.9.7"),sQuery(id+"F0.wireOp",EDGE,"E56.9.8"),sQuery(id+"F0.wireOp",EDGE,"E56.9.9"),sQuery(id+"F0.wireOp",EDGE,"E56.9.10"),sQuery(id+"F0.wireOp",EDGE,"E56.9.11"),sQuery(id+"F0.wireOp",EDGE,"E56.9.12"),sQuery(id+"F0.wireOp",EDGE,"E56.9.13"),sQuery(id+"F0.wireOp",EDGE,"E56.9.14"),sQuery(id+"F0.wireOp",EDGE,"E56.9.15"),sQuery(id+"F0.wireOp",EDGE,"E56.9.16"),sQuery(id+"F0.wireOp",EDGE,"E56.9.17"),sQuery(id+"F0.wireOp",EDGE,"E56.9.18"),sQuery(id+"F0.wireOp",EDGE,"E56.9.19"),sQuery(id+"F0.wireOp",EDGE,"E56.9.20"),sQuery(id+"F0.wireOp",EDGE,"E56.9.21"),sQuery(id+"F0.wireOp",EDGE,"E56.9.22"),sQuery(id+"F0.wireOp",EDGE,"E56.9.23"),sQuery(id+"F0.wireOp",EDGE,"E56.9.24"),sQuery(id+"F0.wireOp",EDGE,"E56.9.25"),sQuery(id+"F0.wireOp",EDGE,"E56.9.26"),sQuery(id+"F0.wireOp",EDGE,"E56.9.27"),sQuery(id+"F0.wireOp",EDGE,"E56.9.28"),sQuery(id+"F0.wireOp",EDGE,"E56.9.29"),sQuery(id+"F0.wireOp",EDGE,"E56.10.0"),sQuery(id+"F0.wireOp",EDGE,"E56.10.1"),sQuery(id+"F0.wireOp",EDGE,"E56.10.2"),sQuery(id+"F0.wireOp",EDGE,"E56.10.3"),sQuery(id+"F0.wireOp",EDGE,"E56.10.4"),sQuery(id+"F0.wireOp",EDGE,"E56.10.5"),sQuery(id+"F0.wireOp",EDGE,"E56.10.6"),sQuery(id+"F0.wireOp",EDGE,"E56.10.7"),sQuery(id+"F0.wireOp",EDGE,"E56.10.8"),sQuery(id+"F0.wireOp",EDGE,"E56.10.9"),sQuery(id+"F0.wireOp",EDGE,"E56.10.10"),sQuery(id+"F0.wireOp",EDGE,"E56.10.11"),sQuery(id+"F0.wireOp",EDGE,"E56.10.12"),sQuery(id+"F0.wireOp",EDGE,"E56.10.13"),sQuery(id+"F0.wireOp",EDGE,"E56.10.14"),sQuery(id+"F0.wireOp",EDGE,"E56.10.15"),sQuery(id+"F0.wireOp",EDGE,"E56.10.16"),sQuery(id+"F0.wireOp",EDGE,"E56.10.17"),sQuery(id+"F0.wireOp",EDGE,"E56.10.18"),sQuery(id+"F0.wireOp",EDGE,"E56.10.19"),sQuery(id+"F0.wireOp",EDGE,"E56.10.20"),sQuery(id+"F0.wireOp",EDGE,"E56.10.21"),sQuery(id+"F0.wireOp",EDGE,"E56.10.22"),sQuery(id+"F0.wireOp",EDGE,"E56.10.23"),sQuery(id+"F0.wireOp",EDGE,"E56.10.24"),sQuery(id+"F0.wireOp",EDGE,"E56.10.25"),sQuery(id+"F0.wireOp",EDGE,"E56.10.26"),sQuery(id+"F0.wireOp",EDGE,"E56.10.27"),sQuery(id+"F0.wireOp",EDGE,"E56.10.28"),sQuery(id+"F0.wireOp",EDGE,"E56.10.29"),sQuery(id+"F0.wireOp",EDGE,"E56.11.0"),sQuery(id+"F0.wireOp",EDGE,"E56.11.1"),sQuery(id+"F0.wireOp",EDGE,"E56.11.2"),sQuery(id+"F0.wireOp",EDGE,"E56.11.3"),sQuery(id+"F0.wireOp",EDGE,"E56.11.4"),sQuery(id+"F0.wireOp",EDGE,"E56.11.5"),sQuery(id+"F0.wireOp",EDGE,"E56.11.6"),sQuery(id+"F0.wireOp",EDGE,"E56.11.7"),sQuery(id+"F0.wireOp",EDGE,"E56.11.8"),sQuery(id+"F0.wireOp",EDGE,"E56.11.9"),sQuery(id+"F0.wireOp",EDGE,"E56.11.10"),sQuery(id+"F0.wireOp",EDGE,"E56.11.11"),sQuery(id+"F0.wireOp",EDGE,"E56.11.12"),sQuery(id+"F0.wireOp",EDGE,"E56.11.13"),sQuery(id+"F0.wireOp",EDGE,"E56.11.14"),sQuery(id+"F0.wireOp",EDGE,"E56.11.15"),sQuery(id+"F0.wireOp",EDGE,"E56.11.16"),sQuery(id+"F0.wireOp",EDGE,"E56.11.17"),sQuery(id+"F0.wireOp",EDGE,"E56.11.18"),sQuery(id+"F0.wireOp",EDGE,"E56.11.19"),sQuery(id+"F0.wireOp",EDGE,"E56.11.20"),sQuery(id+"F0.wireOp",EDGE,"E56.11.21"),sQuery(id+"F0.wireOp",EDGE,"E56.11.22"),sQuery(id+"F0.wireOp",EDGE,"E56.11.23"),sQuery(id+"F0.wireOp",EDGE,"E56.11.24"),sQuery(id+"F0.wireOp",EDGE,"E56.11.25"),sQuery(id+"F0.wireOp",EDGE,"E56.11.26"),sQuery(id+"F0.wireOp",EDGE,"E56.11.27"),sQuery(id+"F0.wireOp",EDGE,"E56.11.28"),sQuery(id+"F0.wireOp",EDGE,"E56.11.29"),sQuery(id+"F0.wireOp",EDGE,"E56.12.0"),sQuery(id+"F0.wireOp",EDGE,"E56.12.1"),sQuery(id+"F0.wireOp",EDGE,"E56.12.2"),sQuery(id+"F0.wireOp",EDGE,"E56.12.3"),sQuery(id+"F0.wireOp",EDGE,"E56.12.4"),sQuery(id+"F0.wireOp",EDGE,"E56.12.5"),sQuery(id+"F0.wireOp",EDGE,"E56.12.6"),sQuery(id+"F0.wireOp",EDGE,"E56.12.7"),sQuery(id+"F0.wireOp",EDGE,"E56.12.8"),sQuery(id+"F0.wireOp",EDGE,"E56.12.9"),sQuery(id+"F0.wireOp",EDGE,"E56.12.10"),sQuery(id+"F0.wireOp",EDGE,"E56.12.11"),sQuery(id+"F0.wireOp",EDGE,"E56.12.12"),sQuery(id+"F0.wireOp",EDGE,"E56.12.13"),sQuery(id+"F0.wireOp",EDGE,"E56.12.14"),sQuery(id+"F0.wireOp",EDGE,"E56.12.15"),sQuery(id+"F0.wireOp",EDGE,"E56.12.16"),sQuery(id+"F0.wireOp",EDGE,"E56.12.17"),sQuery(id+"F0.wireOp",EDGE,"E56.12.18"),sQuery(id+"F0.wireOp",EDGE,"E56.12.19"),sQuery(id+"F0.wireOp",EDGE,"E56.12.20"),sQuery(id+"F0.wireOp",EDGE,"E56.12.21"),sQuery(id+"F0.wireOp",EDGE,"E56.12.22"),sQuery(id+"F0.wireOp",EDGE,"E56.12.23"),sQuery(id+"F0.wireOp",EDGE,"E56.12.24"),sQuery(id+"F0.wireOp",EDGE,"E56.12.25"),sQuery(id+"F0.wireOp",EDGE,"E56.12.26"),sQuery(id+"F0.wireOp",EDGE,"E56.12.27"),sQuery(id+"F0.wireOp",EDGE,"E56.12.28"),sQuery(id+"F0.wireOp",EDGE,"E56.12.29"),sQuery(id+"F0.wireOp",EDGE,"E56.13.0"),sQuery(id+"F0.wireOp",EDGE,"E56.13.1"),sQuery(id+"F0.wireOp",EDGE,"E56.13.2"),sQuery(id+"F0.wireOp",EDGE,"E56.13.3"),sQuery(id+"F0.wireOp",EDGE,"E56.13.4"),sQuery(id+"F0.wireOp",EDGE,"E56.13.5"),sQuery(id+"F0.wireOp",EDGE,"E56.13.6"),sQuery(id+"F0.wireOp",EDGE,"E56.13.7"),sQuery(id+"F0.wireOp",EDGE,"E56.13.8"),sQuery(id+"F0.wireOp",EDGE,"E56.13.9"),sQuery(id+"F0.wireOp",EDGE,"E56.13.10"),sQuery(id+"F0.wireOp",EDGE,"E56.13.11"),sQuery(id+"F0.wireOp",EDGE,"E56.13.12"),sQuery(id+"F0.wireOp",EDGE,"E56.13.13"),sQuery(id+"F0.wireOp",EDGE,"E56.13.14"),sQuery(id+"F0.wireOp",EDGE,"E56.13.15"),sQuery(id+"F0.wireOp",EDGE,"E56.13.16"),sQuery(id+"F0.wireOp",EDGE,"E56.13.17"),sQuery(id+"F0.wireOp",EDGE,"E56.13.18"),sQuery(id+"F0.wireOp",EDGE,"E56.13.19"),sQuery(id+"F0.wireOp",EDGE,"E56.13.20"),sQuery(id+"F0.wireOp",EDGE,"E56.13.21"),sQuery(id+"F0.wireOp",EDGE,"E56.13.22"),sQuery(id+"F0.wireOp",EDGE,"E56.13.23"),sQuery(id+"F0.wireOp",EDGE,"E56.13.24"),sQuery(id+"F0.wireOp",EDGE,"E56.13.25"),sQuery(id+"F0.wireOp",EDGE,"E56.13.26"),sQuery(id+"F0.wireOp",EDGE,"E56.13.27"),sQuery(id+"F0.wireOp",EDGE,"E56.13.28"),sQuery(id+"F0.wireOp",EDGE,"E56.13.29"),sQuery(id+"F0.wireOp",EDGE,"E56.14.0"),sQuery(id+"F0.wireOp",EDGE,"E56.14.1"),sQuery(id+"F0.wireOp",EDGE,"E56.14.2"),sQuery(id+"F0.wireOp",EDGE,"E56.14.3"),sQuery(id+"F0.wireOp",EDGE,"E56.14.4"),sQuery(id+"F0.wireOp",EDGE,"E56.14.5"),sQuery(id+"F0.wireOp",EDGE,"E56.14.6"),sQuery(id+"F0.wireOp",EDGE,"E56.14.7"),sQuery(id+"F0.wireOp",EDGE,"E56.14.8"),sQuery(id+"F0.wireOp",EDGE,"E56.14.9"),sQuery(id+"F0.wireOp",EDGE,"E56.14.10"),sQuery(id+"F0.wireOp",EDGE,"E56.14.11"),sQuery(id+"F0.wireOp",EDGE,"E56.14.12"),sQuery(id+"F0.wireOp",EDGE,"E56.14.13"),sQuery(id+"F0.wireOp",EDGE,"E56.14.14"),sQuery(id+"F0.wireOp",EDGE,"E56.14.15"),sQuery(id+"F0.wireOp",EDGE,"E56.14.16"),sQuery(id+"F0.wireOp",EDGE,"E56.14.17"),sQuery(id+"F0.wireOp",EDGE,"E56.14.18"),sQuery(id+"F0.wireOp",EDGE,"E56.14.19"),sQuery(id+"F0.wireOp",EDGE,"E56.14.20"),sQuery(id+"F0.wireOp",EDGE,"E56.14.21"),sQuery(id+"F0.wireOp",EDGE,"E56.14.22"),sQuery(id+"F0.wireOp",EDGE,"E56.14.23"),sQuery(id+"F0.wireOp",EDGE,"E56.14.24"),sQuery(id+"F0.wireOp",EDGE,"E56.14.25"),sQuery(id+"F0.wireOp",EDGE,"E56.14.26"),sQuery(id+"F0.wireOp",EDGE,"E56.14.27"),sQuery(id+"F0.wireOp",EDGE,"E56.14.28"),sQuery(id+"F0.wireOp",EDGE,"E56.14.29"),sQuery(id+"F0.wireOp",EDGE,"E56.15.0"),sQuery(id+"F0.wireOp",EDGE,"E56.15.1"),sQuery(id+"F0.wireOp",EDGE,"E56.15.2"),sQuery(id+"F0.wireOp",EDGE,"E56.15.3"),sQuery(id+"F0.wireOp",EDGE,"E56.15.4"),sQuery(id+"F0.wireOp",EDGE,"E56.15.5"),sQuery(id+"F0.wireOp",EDGE,"E56.15.6"),sQuery(id+"F0.wireOp",EDGE,"E56.15.7"),sQuery(id+"F0.wireOp",EDGE,"E56.15.8"),sQuery(id+"F0.wireOp",EDGE,"E56.15.9"),sQuery(id+"F0.wireOp",EDGE,"E56.15.10"),sQuery(id+"F0.wireOp",EDGE,"E56.15.11"),sQuery(id+"F0.wireOp",EDGE,"E56.15.12"),sQuery(id+"F0.wireOp",EDGE,"E56.15.13"),sQuery(id+"F0.wireOp",EDGE,"E56.15.14"),sQuery(id+"F0.wireOp",EDGE,"E56.15.15"),sQuery(id+"F0.wireOp",EDGE,"E56.15.16"),sQuery(id+"F0.wireOp",EDGE,"E56.15.17"),sQuery(id+"F0.wireOp",EDGE,"E56.15.18"),sQuery(id+"F0.wireOp",EDGE,"E56.15.19"),sQuery(id+"F0.wireOp",EDGE,"E56.15.20"),sQuery(id+"F0.wireOp",EDGE,"E56.15.21"),sQuery(id+"F0.wireOp",EDGE,"E56.15.22"),sQuery(id+"F0.wireOp",EDGE,"E56.15.23"),sQuery(id+"F0.wireOp",EDGE,"E56.15.24"),sQuery(id+"F0.wireOp",EDGE,"E56.15.25"),sQuery(id+"F0.wireOp",EDGE,"E56.15.26"),sQuery(id+"F0.wireOp",EDGE,"E56.15.27"),sQuery(id+"F0.wireOp",EDGE,"E56.15.28"),sQuery(id+"F0.wireOp",EDGE,"E56.15.29"),sQuery(id+"F0.wireOp",EDGE,"E56.16.0"),sQuery(id+"F0.wireOp",EDGE,"E56.16.1"),sQuery(id+"F0.wireOp",EDGE,"E56.16.2"),sQuery(id+"F0.wireOp",EDGE,"E56.16.3"),sQuery(id+"F0.wireOp",EDGE,"E56.16.4"),sQuery(id+"F0.wireOp",EDGE,"E56.16.5"),sQuery(id+"F0.wireOp",EDGE,"E56.16.6"),sQuery(id+"F0.wireOp",EDGE,"E56.16.7"),sQuery(id+"F0.wireOp",EDGE,"E56.16.8"),sQuery(id+"F0.wireOp",EDGE,"E56.16.9"),sQuery(id+"F0.wireOp",EDGE,"E56.16.10"),sQuery(id+"F0.wireOp",EDGE,"E56.16.11"),sQuery(id+"F0.wireOp",EDGE,"E56.16.12"),sQuery(id+"F0.wireOp",EDGE,"E56.16.13"),sQuery(id+"F0.wireOp",EDGE,"E56.16.14"),sQuery(id+"F0.wireOp",EDGE,"E56.16.15"),sQuery(id+"F0.wireOp",EDGE,"E56.16.16"),sQuery(id+"F0.wireOp",EDGE,"E56.16.17"),sQuery(id+"F0.wireOp",EDGE,"E56.16.18"),sQuery(id+"F0.wireOp",EDGE,"E56.16.19"),sQuery(id+"F0.wireOp",EDGE,"E56.16.20"),sQuery(id+"F0.wireOp",EDGE,"E56.16.21"),sQuery(id+"F0.wireOp",EDGE,"E56.16.22"),sQuery(id+"F0.wireOp",EDGE,"E56.16.23"),sQuery(id+"F0.wireOp",EDGE,"E56.16.24"),sQuery(id+"F0.wireOp",EDGE,"E56.16.25"),sQuery(id+"F0.wireOp",EDGE,"E56.16.26"),sQuery(id+"F0.wireOp",EDGE,"E56.16.27"),sQuery(id+"F0.wireOp",EDGE,"E56.16.28"),sQuery(id+"F0.wireOp",EDGE,"E56.16.29"),sQuery(id+"F0.wireOp",EDGE,"E56.17.0"),sQuery(id+"F0.wireOp",EDGE,"E56.17.1"),sQuery(id+"F0.wireOp",EDGE,"E56.17.2"),sQuery(id+"F0.wireOp",EDGE,"E56.17.3"),sQuery(id+"F0.wireOp",EDGE,"E56.17.4"),sQuery(id+"F0.wireOp",EDGE,"E56.17.5"),sQuery(id+"F0.wireOp",EDGE,"E56.17.6"),sQuery(id+"F0.wireOp",EDGE,"E56.17.7"),sQuery(id+"F0.wireOp",EDGE,"E56.17.8"),sQuery(id+"F0.wireOp",EDGE,"E56.17.9"),sQuery(id+"F0.wireOp",EDGE,"E56.17.10"),sQuery(id+"F0.wireOp",EDGE,"E56.17.11"),sQuery(id+"F0.wireOp",EDGE,"E56.17.12"),sQuery(id+"F0.wireOp",EDGE,"E56.17.13"),sQuery(id+"F0.wireOp",EDGE,"E56.17.14"),sQuery(id+"F0.wireOp",EDGE,"E56.17.15"),sQuery(id+"F0.wireOp",EDGE,"E56.17.16"),sQuery(id+"F0.wireOp",EDGE,"E56.17.17"),sQuery(id+"F0.wireOp",EDGE,"E56.17.18"),sQuery(id+"F0.wireOp",EDGE,"E56.17.19"),sQuery(id+"F0.wireOp",EDGE,"E56.17.20"),sQuery(id+"F0.wireOp",EDGE,"E56.17.21"),sQuery(id+"F0.wireOp",EDGE,"E56.17.22"),sQuery(id+"F0.wireOp",EDGE,"E56.17.23"),sQuery(id+"F0.wireOp",EDGE,"E56.17.24"),sQuery(id+"F0.wireOp",EDGE,"E56.17.25"),sQuery(id+"F0.wireOp",EDGE,"E56.17.26"),sQuery(id+"F0.wireOp",EDGE,"E56.17.27"),sQuery(id+"F0.wireOp",EDGE,"E56.17.28"),sQuery(id+"F0.wireOp",EDGE,"E56.17.29"),sQuery(id+"F0.wireOp",EDGE,"E56.18.0"),sQuery(id+"F0.wireOp",EDGE,"E56.18.1"),sQuery(id+"F0.wireOp",EDGE,"E56.18.2"),sQuery(id+"F0.wireOp",EDGE,"E56.18.3"),sQuery(id+"F0.wireOp",EDGE,"E56.18.4"),sQuery(id+"F0.wireOp",EDGE,"E56.18.5"),sQuery(id+"F0.wireOp",EDGE,"E56.18.6"),sQuery(id+"F0.wireOp",EDGE,"E56.18.7"),sQuery(id+"F0.wireOp",EDGE,"E56.18.8"),sQuery(id+"F0.wireOp",EDGE,"E56.18.9"),sQuery(id+"F0.wireOp",EDGE,"E56.18.10"),sQuery(id+"F0.wireOp",EDGE,"E56.18.11"),sQuery(id+"F0.wireOp",EDGE,"E56.18.12"),sQuery(id+"F0.wireOp",EDGE,"E56.18.13"),sQuery(id+"F0.wireOp",EDGE,"E56.18.14"),sQuery(id+"F0.wireOp",EDGE,"E56.18.15"),sQuery(id+"F0.wireOp",EDGE,"E56.18.16"),sQuery(id+"F0.wireOp",EDGE,"E56.18.17"),sQuery(id+"F0.wireOp",EDGE,"E56.18.18"),sQuery(id+"F0.wireOp",EDGE,"E56.18.19"),sQuery(id+"F0.wireOp",EDGE,"E56.18.20"),sQuery(id+"F0.wireOp",EDGE,"E56.18.21"),sQuery(id+"F0.wireOp",EDGE,"E56.18.22"),sQuery(id+"F0.wireOp",EDGE,"E56.18.23"),sQuery(id+"F0.wireOp",EDGE,"E56.18.24"),sQuery(id+"F0.wireOp",EDGE,"E56.18.25"),sQuery(id+"F0.wireOp",EDGE,"E56.18.26"),sQuery(id+"F0.wireOp",EDGE,"E56.18.27"),sQuery(id+"F0.wireOp",EDGE,"E56.18.28"),sQuery(id+"F0.wireOp",EDGE,"E56.18.29"),sQuery(id+"F0.wireOp",EDGE,"E56.19.0"),sQuery(id+"F0.wireOp",EDGE,"E56.19.1"),sQuery(id+"F0.wireOp",EDGE,"E56.19.2"),sQuery(id+"F0.wireOp",EDGE,"E56.19.3"),sQuery(id+"F0.wireOp",EDGE,"E56.19.4"),sQuery(id+"F0.wireOp",EDGE,"E56.19.5"),sQuery(id+"F0.wireOp",EDGE,"E56.19.6"),sQuery(id+"F0.wireOp",EDGE,"E56.19.7"),sQuery(id+"F0.wireOp",EDGE,"E56.19.8"),sQuery(id+"F0.wireOp",EDGE,"E56.19.9"),sQuery(id+"F0.wireOp",EDGE,"E56.19.10"),sQuery(id+"F0.wireOp",EDGE,"E56.19.11"),sQuery(id+"F0.wireOp",EDGE,"E56.19.12"),sQuery(id+"F0.wireOp",EDGE,"E56.19.13"),sQuery(id+"F0.wireOp",EDGE,"E56.19.14"),sQuery(id+"F0.wireOp",EDGE,"E56.19.15"),sQuery(id+"F0.wireOp",EDGE,"E56.19.16"),sQuery(id+"F0.wireOp",EDGE,"E56.19.17"),sQuery(id+"F0.wireOp",EDGE,"E56.19.18"),sQuery(id+"F0.wireOp",EDGE,"E56.19.19"),sQuery(id+"F0.wireOp",EDGE,"E56.19.20"),sQuery(id+"F0.wireOp",EDGE,"E56.19.21"),sQuery(id+"F0.wireOp",EDGE,"E56.19.22"),sQuery(id+"F0.wireOp",EDGE,"E56.19.23"),sQuery(id+"F0.wireOp",EDGE,"E56.19.24"),sQuery(id+"F0.wireOp",EDGE,"E56.19.25"),sQuery(id+"F0.wireOp",EDGE,"E56.19.26"),sQuery(id+"F0.wireOp",EDGE,"E56.19.27"),sQuery(id+"F0.wireOp",EDGE,"E56.19.28"),sQuery(id+"F0.wireOp",EDGE,"E56.19.29")])]});
            transform(context, id + "F3", {"entities" : qUnion([Q0]), "transformType" : TransformType.TRANSLATION_3D, "dx" : 44.2 * mm, "dy" : -21.59 * mm, "dz" : -6.35 * mm, "makeCopy" : false});
        }
        {
            var Q0;
            Q0=makeQuery(id+"F1.opExtrude","SWEPT_BODY",BODY,{"disambiguationData":[OSD([sQuery(id+"F0.wireOp",EDGE,"E5"),sQuery(id+"F0.wireOp",EDGE,"E26"),sQuery(id+"F0.wireOp",EDGE,"E27.MirrorCS"),sQuery(id+"F0.wireOp",EDGE,"E28"),sQuery(id+"F0.wireOp",EDGE,"E29"),sQuery(id+"F0.wireOp",EDGE,"E30"),sQuery(id+"F0.wireOp",EDGE,"E31"),sQuery(id+"F0.wireOp",EDGE,"E32"),sQuery(id+"F0.wireOp",EDGE,"E33"),sQuery(id+"F0.wireOp",EDGE,"E34"),sQuery(id+"F0.wireOp",EDGE,"E35"),sQuery(id+"F0.wireOp",EDGE,"E36"),sQuery(id+"F0.wireOp",EDGE,"E37"),sQuery(id+"F0.wireOp",EDGE,"E38"),sQuery(id+"F0.wireOp",EDGE,"E39"),sQuery(id+"F0.wireOp",EDGE,"E40"),sQuery(id+"F0.wireOp",EDGE,"E41"),sQuery(id+"F0.wireOp",EDGE,"E42.MirrorCS"),sQuery(id+"F0.wireOp",EDGE,"E43.MirrorCS"),sQuery(id+"F0.wireOp",EDGE,"E44.MirrorCS"),sQuery(id+"F0.wireOp",EDGE,"E45.MirrorCS"),sQuery(id+"F0.wireOp",EDGE,"E46.MirrorCS"),sQuery(id+"F0.wireOp",EDGE,"E47.MirrorCS"),sQuery(id+"F0.wireOp",EDGE,"E48.MirrorCS"),sQuery(id+"F0.wireOp",EDGE,"E49.MirrorCS"),sQuery(id+"F0.wireOp",EDGE,"E50.MirrorCS"),sQuery(id+"F0.wireOp",EDGE,"E51.MirrorCS"),sQuery(id+"F0.wireOp",EDGE,"E52.MirrorCS"),sQuery(id+"F0.wireOp",EDGE,"E53.MirrorCS"),sQuery(id+"F0.wireOp",EDGE,"E54.MirrorCS"),sQuery(id+"F0.wireOp",EDGE,"E55.MirrorCS"),sQuery(id+"F0.wireOp",EDGE,"E56.1.0"),sQuery(id+"F0.wireOp",EDGE,"E56.1.1"),sQuery(id+"F0.wireOp",EDGE,"E56.1.2"),sQuery(id+"F0.wireOp",EDGE,"E56.1.3"),sQuery(id+"F0.wireOp",EDGE,"E56.1.4"),sQuery(id+"F0.wireOp",EDGE,"E56.1.5"),sQuery(id+"F0.wireOp",EDGE,"E56.1.6"),sQuery(id+"F0.wireOp",EDGE,"E56.1.7"),sQuery(id+"F0.wireOp",EDGE,"E56.1.8"),sQuery(id+"F0.wireOp",EDGE,"E56.1.9"),sQuery(id+"F0.wireOp",EDGE,"E56.1.10"),sQuery(id+"F0.wireOp",EDGE,"E56.1.11"),sQuery(id+"F0.wireOp",EDGE,"E56.1.12"),sQuery(id+"F0.wireOp",EDGE,"E56.1.13"),sQuery(id+"F0.wireOp",EDGE,"E56.1.14"),sQuery(id+"F0.wireOp",EDGE,"E56.1.15"),sQuery(id+"F0.wireOp",EDGE,"E56.1.16"),sQuery(id+"F0.wireOp",EDGE,"E56.1.17"),sQuery(id+"F0.wireOp",EDGE,"E56.1.18"),sQuery(id+"F0.wireOp",EDGE,"E56.1.19"),sQuery(id+"F0.wireOp",EDGE,"E56.1.20"),sQuery(id+"F0.wireOp",EDGE,"E56.1.21"),sQuery(id+"F0.wireOp",EDGE,"E56.1.22"),sQuery(id+"F0.wireOp",EDGE,"E56.1.23"),sQuery(id+"F0.wireOp",EDGE,"E56.1.24"),sQuery(id+"F0.wireOp",EDGE,"E56.1.25"),sQuery(id+"F0.wireOp",EDGE,"E56.1.26"),sQuery(id+"F0.wireOp",EDGE,"E56.1.27"),sQuery(id+"F0.wireOp",EDGE,"E56.1.28"),sQuery(id+"F0.wireOp",EDGE,"E56.1.29"),sQuery(id+"F0.wireOp",EDGE,"E56.2.0"),sQuery(id+"F0.wireOp",EDGE,"E56.2.1"),sQuery(id+"F0.wireOp",EDGE,"E56.2.2"),sQuery(id+"F0.wireOp",EDGE,"E56.2.3"),sQuery(id+"F0.wireOp",EDGE,"E56.2.4"),sQuery(id+"F0.wireOp",EDGE,"E56.2.5"),sQuery(id+"F0.wireOp",EDGE,"E56.2.6"),sQuery(id+"F0.wireOp",EDGE,"E56.2.7"),sQuery(id+"F0.wireOp",EDGE,"E56.2.8"),sQuery(id+"F0.wireOp",EDGE,"E56.2.9"),sQuery(id+"F0.wireOp",EDGE,"E56.2.10"),sQuery(id+"F0.wireOp",EDGE,"E56.2.11"),sQuery(id+"F0.wireOp",EDGE,"E56.2.12"),sQuery(id+"F0.wireOp",EDGE,"E56.2.13"),sQuery(id+"F0.wireOp",EDGE,"E56.2.14"),sQuery(id+"F0.wireOp",EDGE,"E56.2.15"),sQuery(id+"F0.wireOp",EDGE,"E56.2.16"),sQuery(id+"F0.wireOp",EDGE,"E56.2.17"),sQuery(id+"F0.wireOp",EDGE,"E56.2.18"),sQuery(id+"F0.wireOp",EDGE,"E56.2.19"),sQuery(id+"F0.wireOp",EDGE,"E56.2.20"),sQuery(id+"F0.wireOp",EDGE,"E56.2.21"),sQuery(id+"F0.wireOp",EDGE,"E56.2.22"),sQuery(id+"F0.wireOp",EDGE,"E56.2.23"),sQuery(id+"F0.wireOp",EDGE,"E56.2.24"),sQuery(id+"F0.wireOp",EDGE,"E56.2.25"),sQuery(id+"F0.wireOp",EDGE,"E56.2.26"),sQuery(id+"F0.wireOp",EDGE,"E56.2.27"),sQuery(id+"F0.wireOp",EDGE,"E56.2.28"),sQuery(id+"F0.wireOp",EDGE,"E56.2.29"),sQuery(id+"F0.wireOp",EDGE,"E56.3.0"),sQuery(id+"F0.wireOp",EDGE,"E56.3.1"),sQuery(id+"F0.wireOp",EDGE,"E56.3.2"),sQuery(id+"F0.wireOp",EDGE,"E56.3.3"),sQuery(id+"F0.wireOp",EDGE,"E56.3.4"),sQuery(id+"F0.wireOp",EDGE,"E56.3.5"),sQuery(id+"F0.wireOp",EDGE,"E56.3.6"),sQuery(id+"F0.wireOp",EDGE,"E56.3.7"),sQuery(id+"F0.wireOp",EDGE,"E56.3.8"),sQuery(id+"F0.wireOp",EDGE,"E56.3.9"),sQuery(id+"F0.wireOp",EDGE,"E56.3.10"),sQuery(id+"F0.wireOp",EDGE,"E56.3.11"),sQuery(id+"F0.wireOp",EDGE,"E56.3.12"),sQuery(id+"F0.wireOp",EDGE,"E56.3.13"),sQuery(id+"F0.wireOp",EDGE,"E56.3.14"),sQuery(id+"F0.wireOp",EDGE,"E56.3.15"),sQuery(id+"F0.wireOp",EDGE,"E56.3.16"),sQuery(id+"F0.wireOp",EDGE,"E56.3.17"),sQuery(id+"F0.wireOp",EDGE,"E56.3.18"),sQuery(id+"F0.wireOp",EDGE,"E56.3.19"),sQuery(id+"F0.wireOp",EDGE,"E56.3.20"),sQuery(id+"F0.wireOp",EDGE,"E56.3.21"),sQuery(id+"F0.wireOp",EDGE,"E56.3.22"),sQuery(id+"F0.wireOp",EDGE,"E56.3.23"),sQuery(id+"F0.wireOp",EDGE,"E56.3.24"),sQuery(id+"F0.wireOp",EDGE,"E56.3.25"),sQuery(id+"F0.wireOp",EDGE,"E56.3.26"),sQuery(id+"F0.wireOp",EDGE,"E56.3.27"),sQuery(id+"F0.wireOp",EDGE,"E56.3.28"),sQuery(id+"F0.wireOp",EDGE,"E56.3.29"),sQuery(id+"F0.wireOp",EDGE,"E56.4.0"),sQuery(id+"F0.wireOp",EDGE,"E56.4.1"),sQuery(id+"F0.wireOp",EDGE,"E56.4.2"),sQuery(id+"F0.wireOp",EDGE,"E56.4.3"),sQuery(id+"F0.wireOp",EDGE,"E56.4.4"),sQuery(id+"F0.wireOp",EDGE,"E56.4.5"),sQuery(id+"F0.wireOp",EDGE,"E56.4.6"),sQuery(id+"F0.wireOp",EDGE,"E56.4.7"),sQuery(id+"F0.wireOp",EDGE,"E56.4.8"),sQuery(id+"F0.wireOp",EDGE,"E56.4.9"),sQuery(id+"F0.wireOp",EDGE,"E56.4.10"),sQuery(id+"F0.wireOp",EDGE,"E56.4.11"),sQuery(id+"F0.wireOp",EDGE,"E56.4.12"),sQuery(id+"F0.wireOp",EDGE,"E56.4.13"),sQuery(id+"F0.wireOp",EDGE,"E56.4.14"),sQuery(id+"F0.wireOp",EDGE,"E56.4.15"),sQuery(id+"F0.wireOp",EDGE,"E56.4.16"),sQuery(id+"F0.wireOp",EDGE,"E56.4.17"),sQuery(id+"F0.wireOp",EDGE,"E56.4.18"),sQuery(id+"F0.wireOp",EDGE,"E56.4.19"),sQuery(id+"F0.wireOp",EDGE,"E56.4.20"),sQuery(id+"F0.wireOp",EDGE,"E56.4.21"),sQuery(id+"F0.wireOp",EDGE,"E56.4.22"),sQuery(id+"F0.wireOp",EDGE,"E56.4.23"),sQuery(id+"F0.wireOp",EDGE,"E56.4.24"),sQuery(id+"F0.wireOp",EDGE,"E56.4.25"),sQuery(id+"F0.wireOp",EDGE,"E56.4.26"),sQuery(id+"F0.wireOp",EDGE,"E56.4.27"),sQuery(id+"F0.wireOp",EDGE,"E56.4.28"),sQuery(id+"F0.wireOp",EDGE,"E56.4.29"),sQuery(id+"F0.wireOp",EDGE,"E56.5.0"),sQuery(id+"F0.wireOp",EDGE,"E56.5.1"),sQuery(id+"F0.wireOp",EDGE,"E56.5.2"),sQuery(id+"F0.wireOp",EDGE,"E56.5.3"),sQuery(id+"F0.wireOp",EDGE,"E56.5.4"),sQuery(id+"F0.wireOp",EDGE,"E56.5.5"),sQuery(id+"F0.wireOp",EDGE,"E56.5.6"),sQuery(id+"F0.wireOp",EDGE,"E56.5.7"),sQuery(id+"F0.wireOp",EDGE,"E56.5.8"),sQuery(id+"F0.wireOp",EDGE,"E56.5.9"),sQuery(id+"F0.wireOp",EDGE,"E56.5.10"),sQuery(id+"F0.wireOp",EDGE,"E56.5.11"),sQuery(id+"F0.wireOp",EDGE,"E56.5.12"),sQuery(id+"F0.wireOp",EDGE,"E56.5.13"),sQuery(id+"F0.wireOp",EDGE,"E56.5.14"),sQuery(id+"F0.wireOp",EDGE,"E56.5.15"),sQuery(id+"F0.wireOp",EDGE,"E56.5.16"),sQuery(id+"F0.wireOp",EDGE,"E56.5.17"),sQuery(id+"F0.wireOp",EDGE,"E56.5.18"),sQuery(id+"F0.wireOp",EDGE,"E56.5.19"),sQuery(id+"F0.wireOp",EDGE,"E56.5.20"),sQuery(id+"F0.wireOp",EDGE,"E56.5.21"),sQuery(id+"F0.wireOp",EDGE,"E56.5.22"),sQuery(id+"F0.wireOp",EDGE,"E56.5.23"),sQuery(id+"F0.wireOp",EDGE,"E56.5.24"),sQuery(id+"F0.wireOp",EDGE,"E56.5.25"),sQuery(id+"F0.wireOp",EDGE,"E56.5.26"),sQuery(id+"F0.wireOp",EDGE,"E56.5.27"),sQuery(id+"F0.wireOp",EDGE,"E56.5.28"),sQuery(id+"F0.wireOp",EDGE,"E56.5.29"),sQuery(id+"F0.wireOp",EDGE,"E56.6.0"),sQuery(id+"F0.wireOp",EDGE,"E56.6.1"),sQuery(id+"F0.wireOp",EDGE,"E56.6.2"),sQuery(id+"F0.wireOp",EDGE,"E56.6.3"),sQuery(id+"F0.wireOp",EDGE,"E56.6.4"),sQuery(id+"F0.wireOp",EDGE,"E56.6.5"),sQuery(id+"F0.wireOp",EDGE,"E56.6.6"),sQuery(id+"F0.wireOp",EDGE,"E56.6.7"),sQuery(id+"F0.wireOp",EDGE,"E56.6.8"),sQuery(id+"F0.wireOp",EDGE,"E56.6.9"),sQuery(id+"F0.wireOp",EDGE,"E56.6.10"),sQuery(id+"F0.wireOp",EDGE,"E56.6.11"),sQuery(id+"F0.wireOp",EDGE,"E56.6.12"),sQuery(id+"F0.wireOp",EDGE,"E56.6.13"),sQuery(id+"F0.wireOp",EDGE,"E56.6.14"),sQuery(id+"F0.wireOp",EDGE,"E56.6.15"),sQuery(id+"F0.wireOp",EDGE,"E56.6.16"),sQuery(id+"F0.wireOp",EDGE,"E56.6.17"),sQuery(id+"F0.wireOp",EDGE,"E56.6.18"),sQuery(id+"F0.wireOp",EDGE,"E56.6.19"),sQuery(id+"F0.wireOp",EDGE,"E56.6.20"),sQuery(id+"F0.wireOp",EDGE,"E56.6.21"),sQuery(id+"F0.wireOp",EDGE,"E56.6.22"),sQuery(id+"F0.wireOp",EDGE,"E56.6.23"),sQuery(id+"F0.wireOp",EDGE,"E56.6.24"),sQuery(id+"F0.wireOp",EDGE,"E56.6.25"),sQuery(id+"F0.wireOp",EDGE,"E56.6.26"),sQuery(id+"F0.wireOp",EDGE,"E56.6.27"),sQuery(id+"F0.wireOp",EDGE,"E56.6.28"),sQuery(id+"F0.wireOp",EDGE,"E56.6.29"),sQuery(id+"F0.wireOp",EDGE,"E56.7.0"),sQuery(id+"F0.wireOp",EDGE,"E56.7.1"),sQuery(id+"F0.wireOp",EDGE,"E56.7.2"),sQuery(id+"F0.wireOp",EDGE,"E56.7.3"),sQuery(id+"F0.wireOp",EDGE,"E56.7.4"),sQuery(id+"F0.wireOp",EDGE,"E56.7.5"),sQuery(id+"F0.wireOp",EDGE,"E56.7.6"),sQuery(id+"F0.wireOp",EDGE,"E56.7.7"),sQuery(id+"F0.wireOp",EDGE,"E56.7.8"),sQuery(id+"F0.wireOp",EDGE,"E56.7.9"),sQuery(id+"F0.wireOp",EDGE,"E56.7.10"),sQuery(id+"F0.wireOp",EDGE,"E56.7.11"),sQuery(id+"F0.wireOp",EDGE,"E56.7.12"),sQuery(id+"F0.wireOp",EDGE,"E56.7.13"),sQuery(id+"F0.wireOp",EDGE,"E56.7.14"),sQuery(id+"F0.wireOp",EDGE,"E56.7.15"),sQuery(id+"F0.wireOp",EDGE,"E56.7.16"),sQuery(id+"F0.wireOp",EDGE,"E56.7.17"),sQuery(id+"F0.wireOp",EDGE,"E56.7.18"),sQuery(id+"F0.wireOp",EDGE,"E56.7.19"),sQuery(id+"F0.wireOp",EDGE,"E56.7.20"),sQuery(id+"F0.wireOp",EDGE,"E56.7.21"),sQuery(id+"F0.wireOp",EDGE,"E56.7.22"),sQuery(id+"F0.wireOp",EDGE,"E56.7.23"),sQuery(id+"F0.wireOp",EDGE,"E56.7.24"),sQuery(id+"F0.wireOp",EDGE,"E56.7.25"),sQuery(id+"F0.wireOp",EDGE,"E56.7.26"),sQuery(id+"F0.wireOp",EDGE,"E56.7.27"),sQuery(id+"F0.wireOp",EDGE,"E56.7.28"),sQuery(id+"F0.wireOp",EDGE,"E56.7.29"),sQuery(id+"F0.wireOp",EDGE,"E56.8.0"),sQuery(id+"F0.wireOp",EDGE,"E56.8.1"),sQuery(id+"F0.wireOp",EDGE,"E56.8.2"),sQuery(id+"F0.wireOp",EDGE,"E56.8.3"),sQuery(id+"F0.wireOp",EDGE,"E56.8.4"),sQuery(id+"F0.wireOp",EDGE,"E56.8.5"),sQuery(id+"F0.wireOp",EDGE,"E56.8.6"),sQuery(id+"F0.wireOp",EDGE,"E56.8.7"),sQuery(id+"F0.wireOp",EDGE,"E56.8.8"),sQuery(id+"F0.wireOp",EDGE,"E56.8.9"),sQuery(id+"F0.wireOp",EDGE,"E56.8.10"),sQuery(id+"F0.wireOp",EDGE,"E56.8.11"),sQuery(id+"F0.wireOp",EDGE,"E56.8.12"),sQuery(id+"F0.wireOp",EDGE,"E56.8.13"),sQuery(id+"F0.wireOp",EDGE,"E56.8.14"),sQuery(id+"F0.wireOp",EDGE,"E56.8.15"),sQuery(id+"F0.wireOp",EDGE,"E56.8.16"),sQuery(id+"F0.wireOp",EDGE,"E56.8.17"),sQuery(id+"F0.wireOp",EDGE,"E56.8.18"),sQuery(id+"F0.wireOp",EDGE,"E56.8.19"),sQuery(id+"F0.wireOp",EDGE,"E56.8.20"),sQuery(id+"F0.wireOp",EDGE,"E56.8.21"),sQuery(id+"F0.wireOp",EDGE,"E56.8.22"),sQuery(id+"F0.wireOp",EDGE,"E56.8.23"),sQuery(id+"F0.wireOp",EDGE,"E56.8.24"),sQuery(id+"F0.wireOp",EDGE,"E56.8.25"),sQuery(id+"F0.wireOp",EDGE,"E56.8.26"),sQuery(id+"F0.wireOp",EDGE,"E56.8.27"),sQuery(id+"F0.wireOp",EDGE,"E56.8.28"),sQuery(id+"F0.wireOp",EDGE,"E56.8.29"),sQuery(id+"F0.wireOp",EDGE,"E56.9.0"),sQuery(id+"F0.wireOp",EDGE,"E56.9.1"),sQuery(id+"F0.wireOp",EDGE,"E56.9.2"),sQuery(id+"F0.wireOp",EDGE,"E56.9.3"),sQuery(id+"F0.wireOp",EDGE,"E56.9.4"),sQuery(id+"F0.wireOp",EDGE,"E56.9.5"),sQuery(id+"F0.wireOp",EDGE,"E56.9.6"),sQuery(id+"F0.wireOp",EDGE,"E56.9.7"),sQuery(id+"F0.wireOp",EDGE,"E56.9.8"),sQuery(id+"F0.wireOp",EDGE,"E56.9.9"),sQuery(id+"F0.wireOp",EDGE,"E56.9.10"),sQuery(id+"F0.wireOp",EDGE,"E56.9.11"),sQuery(id+"F0.wireOp",EDGE,"E56.9.12"),sQuery(id+"F0.wireOp",EDGE,"E56.9.13"),sQuery(id+"F0.wireOp",EDGE,"E56.9.14"),sQuery(id+"F0.wireOp",EDGE,"E56.9.15"),sQuery(id+"F0.wireOp",EDGE,"E56.9.16"),sQuery(id+"F0.wireOp",EDGE,"E56.9.17"),sQuery(id+"F0.wireOp",EDGE,"E56.9.18"),sQuery(id+"F0.wireOp",EDGE,"E56.9.19"),sQuery(id+"F0.wireOp",EDGE,"E56.9.20"),sQuery(id+"F0.wireOp",EDGE,"E56.9.21"),sQuery(id+"F0.wireOp",EDGE,"E56.9.22"),sQuery(id+"F0.wireOp",EDGE,"E56.9.23"),sQuery(id+"F0.wireOp",EDGE,"E56.9.24"),sQuery(id+"F0.wireOp",EDGE,"E56.9.25"),sQuery(id+"F0.wireOp",EDGE,"E56.9.26"),sQuery(id+"F0.wireOp",EDGE,"E56.9.27"),sQuery(id+"F0.wireOp",EDGE,"E56.9.28"),sQuery(id+"F0.wireOp",EDGE,"E56.9.29"),sQuery(id+"F0.wireOp",EDGE,"E56.10.0"),sQuery(id+"F0.wireOp",EDGE,"E56.10.1"),sQuery(id+"F0.wireOp",EDGE,"E56.10.2"),sQuery(id+"F0.wireOp",EDGE,"E56.10.3"),sQuery(id+"F0.wireOp",EDGE,"E56.10.4"),sQuery(id+"F0.wireOp",EDGE,"E56.10.5"),sQuery(id+"F0.wireOp",EDGE,"E56.10.6"),sQuery(id+"F0.wireOp",EDGE,"E56.10.7"),sQuery(id+"F0.wireOp",EDGE,"E56.10.8"),sQuery(id+"F0.wireOp",EDGE,"E56.10.9"),sQuery(id+"F0.wireOp",EDGE,"E56.10.10"),sQuery(id+"F0.wireOp",EDGE,"E56.10.11"),sQuery(id+"F0.wireOp",EDGE,"E56.10.12"),sQuery(id+"F0.wireOp",EDGE,"E56.10.13"),sQuery(id+"F0.wireOp",EDGE,"E56.10.14"),sQuery(id+"F0.wireOp",EDGE,"E56.10.15"),sQuery(id+"F0.wireOp",EDGE,"E56.10.16"),sQuery(id+"F0.wireOp",EDGE,"E56.10.17"),sQuery(id+"F0.wireOp",EDGE,"E56.10.18"),sQuery(id+"F0.wireOp",EDGE,"E56.10.19"),sQuery(id+"F0.wireOp",EDGE,"E56.10.20"),sQuery(id+"F0.wireOp",EDGE,"E56.10.21"),sQuery(id+"F0.wireOp",EDGE,"E56.10.22"),sQuery(id+"F0.wireOp",EDGE,"E56.10.23"),sQuery(id+"F0.wireOp",EDGE,"E56.10.24"),sQuery(id+"F0.wireOp",EDGE,"E56.10.25"),sQuery(id+"F0.wireOp",EDGE,"E56.10.26"),sQuery(id+"F0.wireOp",EDGE,"E56.10.27"),sQuery(id+"F0.wireOp",EDGE,"E56.10.28"),sQuery(id+"F0.wireOp",EDGE,"E56.10.29"),sQuery(id+"F0.wireOp",EDGE,"E56.11.0"),sQuery(id+"F0.wireOp",EDGE,"E56.11.1"),sQuery(id+"F0.wireOp",EDGE,"E56.11.2"),sQuery(id+"F0.wireOp",EDGE,"E56.11.3"),sQuery(id+"F0.wireOp",EDGE,"E56.11.4"),sQuery(id+"F0.wireOp",EDGE,"E56.11.5"),sQuery(id+"F0.wireOp",EDGE,"E56.11.6"),sQuery(id+"F0.wireOp",EDGE,"E56.11.7"),sQuery(id+"F0.wireOp",EDGE,"E56.11.8"),sQuery(id+"F0.wireOp",EDGE,"E56.11.9"),sQuery(id+"F0.wireOp",EDGE,"E56.11.10"),sQuery(id+"F0.wireOp",EDGE,"E56.11.11"),sQuery(id+"F0.wireOp",EDGE,"E56.11.12"),sQuery(id+"F0.wireOp",EDGE,"E56.11.13"),sQuery(id+"F0.wireOp",EDGE,"E56.11.14"),sQuery(id+"F0.wireOp",EDGE,"E56.11.15"),sQuery(id+"F0.wireOp",EDGE,"E56.11.16"),sQuery(id+"F0.wireOp",EDGE,"E56.11.17"),sQuery(id+"F0.wireOp",EDGE,"E56.11.18"),sQuery(id+"F0.wireOp",EDGE,"E56.11.19"),sQuery(id+"F0.wireOp",EDGE,"E56.11.20"),sQuery(id+"F0.wireOp",EDGE,"E56.11.21"),sQuery(id+"F0.wireOp",EDGE,"E56.11.22"),sQuery(id+"F0.wireOp",EDGE,"E56.11.23"),sQuery(id+"F0.wireOp",EDGE,"E56.11.24"),sQuery(id+"F0.wireOp",EDGE,"E56.11.25"),sQuery(id+"F0.wireOp",EDGE,"E56.11.26"),sQuery(id+"F0.wireOp",EDGE,"E56.11.27"),sQuery(id+"F0.wireOp",EDGE,"E56.11.28"),sQuery(id+"F0.wireOp",EDGE,"E56.11.29"),sQuery(id+"F0.wireOp",EDGE,"E56.12.0"),sQuery(id+"F0.wireOp",EDGE,"E56.12.1"),sQuery(id+"F0.wireOp",EDGE,"E56.12.2"),sQuery(id+"F0.wireOp",EDGE,"E56.12.3"),sQuery(id+"F0.wireOp",EDGE,"E56.12.4"),sQuery(id+"F0.wireOp",EDGE,"E56.12.5"),sQuery(id+"F0.wireOp",EDGE,"E56.12.6"),sQuery(id+"F0.wireOp",EDGE,"E56.12.7"),sQuery(id+"F0.wireOp",EDGE,"E56.12.8"),sQuery(id+"F0.wireOp",EDGE,"E56.12.9"),sQuery(id+"F0.wireOp",EDGE,"E56.12.10"),sQuery(id+"F0.wireOp",EDGE,"E56.12.11"),sQuery(id+"F0.wireOp",EDGE,"E56.12.12"),sQuery(id+"F0.wireOp",EDGE,"E56.12.13"),sQuery(id+"F0.wireOp",EDGE,"E56.12.14"),sQuery(id+"F0.wireOp",EDGE,"E56.12.15"),sQuery(id+"F0.wireOp",EDGE,"E56.12.16"),sQuery(id+"F0.wireOp",EDGE,"E56.12.17"),sQuery(id+"F0.wireOp",EDGE,"E56.12.18"),sQuery(id+"F0.wireOp",EDGE,"E56.12.19"),sQuery(id+"F0.wireOp",EDGE,"E56.12.20"),sQuery(id+"F0.wireOp",EDGE,"E56.12.21"),sQuery(id+"F0.wireOp",EDGE,"E56.12.22"),sQuery(id+"F0.wireOp",EDGE,"E56.12.23"),sQuery(id+"F0.wireOp",EDGE,"E56.12.24"),sQuery(id+"F0.wireOp",EDGE,"E56.12.25"),sQuery(id+"F0.wireOp",EDGE,"E56.12.26"),sQuery(id+"F0.wireOp",EDGE,"E56.12.27"),sQuery(id+"F0.wireOp",EDGE,"E56.12.28"),sQuery(id+"F0.wireOp",EDGE,"E56.12.29"),sQuery(id+"F0.wireOp",EDGE,"E56.13.0"),sQuery(id+"F0.wireOp",EDGE,"E56.13.1"),sQuery(id+"F0.wireOp",EDGE,"E56.13.2"),sQuery(id+"F0.wireOp",EDGE,"E56.13.3"),sQuery(id+"F0.wireOp",EDGE,"E56.13.4"),sQuery(id+"F0.wireOp",EDGE,"E56.13.5"),sQuery(id+"F0.wireOp",EDGE,"E56.13.6"),sQuery(id+"F0.wireOp",EDGE,"E56.13.7"),sQuery(id+"F0.wireOp",EDGE,"E56.13.8"),sQuery(id+"F0.wireOp",EDGE,"E56.13.9"),sQuery(id+"F0.wireOp",EDGE,"E56.13.10"),sQuery(id+"F0.wireOp",EDGE,"E56.13.11"),sQuery(id+"F0.wireOp",EDGE,"E56.13.12"),sQuery(id+"F0.wireOp",EDGE,"E56.13.13"),sQuery(id+"F0.wireOp",EDGE,"E56.13.14"),sQuery(id+"F0.wireOp",EDGE,"E56.13.15"),sQuery(id+"F0.wireOp",EDGE,"E56.13.16"),sQuery(id+"F0.wireOp",EDGE,"E56.13.17"),sQuery(id+"F0.wireOp",EDGE,"E56.13.18"),sQuery(id+"F0.wireOp",EDGE,"E56.13.19"),sQuery(id+"F0.wireOp",EDGE,"E56.13.20"),sQuery(id+"F0.wireOp",EDGE,"E56.13.21"),sQuery(id+"F0.wireOp",EDGE,"E56.13.22"),sQuery(id+"F0.wireOp",EDGE,"E56.13.23"),sQuery(id+"F0.wireOp",EDGE,"E56.13.24"),sQuery(id+"F0.wireOp",EDGE,"E56.13.25"),sQuery(id+"F0.wireOp",EDGE,"E56.13.26"),sQuery(id+"F0.wireOp",EDGE,"E56.13.27"),sQuery(id+"F0.wireOp",EDGE,"E56.13.28"),sQuery(id+"F0.wireOp",EDGE,"E56.13.29"),sQuery(id+"F0.wireOp",EDGE,"E56.14.0"),sQuery(id+"F0.wireOp",EDGE,"E56.14.1"),sQuery(id+"F0.wireOp",EDGE,"E56.14.2"),sQuery(id+"F0.wireOp",EDGE,"E56.14.3"),sQuery(id+"F0.wireOp",EDGE,"E56.14.4"),sQuery(id+"F0.wireOp",EDGE,"E56.14.5"),sQuery(id+"F0.wireOp",EDGE,"E56.14.6"),sQuery(id+"F0.wireOp",EDGE,"E56.14.7"),sQuery(id+"F0.wireOp",EDGE,"E56.14.8"),sQuery(id+"F0.wireOp",EDGE,"E56.14.9"),sQuery(id+"F0.wireOp",EDGE,"E56.14.10"),sQuery(id+"F0.wireOp",EDGE,"E56.14.11"),sQuery(id+"F0.wireOp",EDGE,"E56.14.12"),sQuery(id+"F0.wireOp",EDGE,"E56.14.13"),sQuery(id+"F0.wireOp",EDGE,"E56.14.14"),sQuery(id+"F0.wireOp",EDGE,"E56.14.15"),sQuery(id+"F0.wireOp",EDGE,"E56.14.16"),sQuery(id+"F0.wireOp",EDGE,"E56.14.17"),sQuery(id+"F0.wireOp",EDGE,"E56.14.18"),sQuery(id+"F0.wireOp",EDGE,"E56.14.19"),sQuery(id+"F0.wireOp",EDGE,"E56.14.20"),sQuery(id+"F0.wireOp",EDGE,"E56.14.21"),sQuery(id+"F0.wireOp",EDGE,"E56.14.22"),sQuery(id+"F0.wireOp",EDGE,"E56.14.23"),sQuery(id+"F0.wireOp",EDGE,"E56.14.24"),sQuery(id+"F0.wireOp",EDGE,"E56.14.25"),sQuery(id+"F0.wireOp",EDGE,"E56.14.26"),sQuery(id+"F0.wireOp",EDGE,"E56.14.27"),sQuery(id+"F0.wireOp",EDGE,"E56.14.28"),sQuery(id+"F0.wireOp",EDGE,"E56.14.29"),sQuery(id+"F0.wireOp",EDGE,"E56.15.0"),sQuery(id+"F0.wireOp",EDGE,"E56.15.1"),sQuery(id+"F0.wireOp",EDGE,"E56.15.2"),sQuery(id+"F0.wireOp",EDGE,"E56.15.3"),sQuery(id+"F0.wireOp",EDGE,"E56.15.4"),sQuery(id+"F0.wireOp",EDGE,"E56.15.5"),sQuery(id+"F0.wireOp",EDGE,"E56.15.6"),sQuery(id+"F0.wireOp",EDGE,"E56.15.7"),sQuery(id+"F0.wireOp",EDGE,"E56.15.8"),sQuery(id+"F0.wireOp",EDGE,"E56.15.9"),sQuery(id+"F0.wireOp",EDGE,"E56.15.10"),sQuery(id+"F0.wireOp",EDGE,"E56.15.11"),sQuery(id+"F0.wireOp",EDGE,"E56.15.12"),sQuery(id+"F0.wireOp",EDGE,"E56.15.13"),sQuery(id+"F0.wireOp",EDGE,"E56.15.14"),sQuery(id+"F0.wireOp",EDGE,"E56.15.15"),sQuery(id+"F0.wireOp",EDGE,"E56.15.16"),sQuery(id+"F0.wireOp",EDGE,"E56.15.17"),sQuery(id+"F0.wireOp",EDGE,"E56.15.18"),sQuery(id+"F0.wireOp",EDGE,"E56.15.19"),sQuery(id+"F0.wireOp",EDGE,"E56.15.20"),sQuery(id+"F0.wireOp",EDGE,"E56.15.21"),sQuery(id+"F0.wireOp",EDGE,"E56.15.22"),sQuery(id+"F0.wireOp",EDGE,"E56.15.23"),sQuery(id+"F0.wireOp",EDGE,"E56.15.24"),sQuery(id+"F0.wireOp",EDGE,"E56.15.25"),sQuery(id+"F0.wireOp",EDGE,"E56.15.26"),sQuery(id+"F0.wireOp",EDGE,"E56.15.27"),sQuery(id+"F0.wireOp",EDGE,"E56.15.28"),sQuery(id+"F0.wireOp",EDGE,"E56.15.29"),sQuery(id+"F0.wireOp",EDGE,"E56.16.0"),sQuery(id+"F0.wireOp",EDGE,"E56.16.1"),sQuery(id+"F0.wireOp",EDGE,"E56.16.2"),sQuery(id+"F0.wireOp",EDGE,"E56.16.3"),sQuery(id+"F0.wireOp",EDGE,"E56.16.4"),sQuery(id+"F0.wireOp",EDGE,"E56.16.5"),sQuery(id+"F0.wireOp",EDGE,"E56.16.6"),sQuery(id+"F0.wireOp",EDGE,"E56.16.7"),sQuery(id+"F0.wireOp",EDGE,"E56.16.8"),sQuery(id+"F0.wireOp",EDGE,"E56.16.9"),sQuery(id+"F0.wireOp",EDGE,"E56.16.10"),sQuery(id+"F0.wireOp",EDGE,"E56.16.11"),sQuery(id+"F0.wireOp",EDGE,"E56.16.12"),sQuery(id+"F0.wireOp",EDGE,"E56.16.13"),sQuery(id+"F0.wireOp",EDGE,"E56.16.14"),sQuery(id+"F0.wireOp",EDGE,"E56.16.15"),sQuery(id+"F0.wireOp",EDGE,"E56.16.16"),sQuery(id+"F0.wireOp",EDGE,"E56.16.17"),sQuery(id+"F0.wireOp",EDGE,"E56.16.18"),sQuery(id+"F0.wireOp",EDGE,"E56.16.19"),sQuery(id+"F0.wireOp",EDGE,"E56.16.20"),sQuery(id+"F0.wireOp",EDGE,"E56.16.21"),sQuery(id+"F0.wireOp",EDGE,"E56.16.22"),sQuery(id+"F0.wireOp",EDGE,"E56.16.23"),sQuery(id+"F0.wireOp",EDGE,"E56.16.24"),sQuery(id+"F0.wireOp",EDGE,"E56.16.25"),sQuery(id+"F0.wireOp",EDGE,"E56.16.26"),sQuery(id+"F0.wireOp",EDGE,"E56.16.27"),sQuery(id+"F0.wireOp",EDGE,"E56.16.28"),sQuery(id+"F0.wireOp",EDGE,"E56.16.29"),sQuery(id+"F0.wireOp",EDGE,"E56.17.0"),sQuery(id+"F0.wireOp",EDGE,"E56.17.1"),sQuery(id+"F0.wireOp",EDGE,"E56.17.2"),sQuery(id+"F0.wireOp",EDGE,"E56.17.3"),sQuery(id+"F0.wireOp",EDGE,"E56.17.4"),sQuery(id+"F0.wireOp",EDGE,"E56.17.5"),sQuery(id+"F0.wireOp",EDGE,"E56.17.6"),sQuery(id+"F0.wireOp",EDGE,"E56.17.7"),sQuery(id+"F0.wireOp",EDGE,"E56.17.8"),sQuery(id+"F0.wireOp",EDGE,"E56.17.9"),sQuery(id+"F0.wireOp",EDGE,"E56.17.10"),sQuery(id+"F0.wireOp",EDGE,"E56.17.11"),sQuery(id+"F0.wireOp",EDGE,"E56.17.12"),sQuery(id+"F0.wireOp",EDGE,"E56.17.13"),sQuery(id+"F0.wireOp",EDGE,"E56.17.14"),sQuery(id+"F0.wireOp",EDGE,"E56.17.15"),sQuery(id+"F0.wireOp",EDGE,"E56.17.16"),sQuery(id+"F0.wireOp",EDGE,"E56.17.17"),sQuery(id+"F0.wireOp",EDGE,"E56.17.18"),sQuery(id+"F0.wireOp",EDGE,"E56.17.19"),sQuery(id+"F0.wireOp",EDGE,"E56.17.20"),sQuery(id+"F0.wireOp",EDGE,"E56.17.21"),sQuery(id+"F0.wireOp",EDGE,"E56.17.22"),sQuery(id+"F0.wireOp",EDGE,"E56.17.23"),sQuery(id+"F0.wireOp",EDGE,"E56.17.24"),sQuery(id+"F0.wireOp",EDGE,"E56.17.25"),sQuery(id+"F0.wireOp",EDGE,"E56.17.26"),sQuery(id+"F0.wireOp",EDGE,"E56.17.27"),sQuery(id+"F0.wireOp",EDGE,"E56.17.28"),sQuery(id+"F0.wireOp",EDGE,"E56.17.29"),sQuery(id+"F0.wireOp",EDGE,"E56.18.0"),sQuery(id+"F0.wireOp",EDGE,"E56.18.1"),sQuery(id+"F0.wireOp",EDGE,"E56.18.2"),sQuery(id+"F0.wireOp",EDGE,"E56.18.3"),sQuery(id+"F0.wireOp",EDGE,"E56.18.4"),sQuery(id+"F0.wireOp",EDGE,"E56.18.5"),sQuery(id+"F0.wireOp",EDGE,"E56.18.6"),sQuery(id+"F0.wireOp",EDGE,"E56.18.7"),sQuery(id+"F0.wireOp",EDGE,"E56.18.8"),sQuery(id+"F0.wireOp",EDGE,"E56.18.9"),sQuery(id+"F0.wireOp",EDGE,"E56.18.10"),sQuery(id+"F0.wireOp",EDGE,"E56.18.11"),sQuery(id+"F0.wireOp",EDGE,"E56.18.12"),sQuery(id+"F0.wireOp",EDGE,"E56.18.13"),sQuery(id+"F0.wireOp",EDGE,"E56.18.14"),sQuery(id+"F0.wireOp",EDGE,"E56.18.15"),sQuery(id+"F0.wireOp",EDGE,"E56.18.16"),sQuery(id+"F0.wireOp",EDGE,"E56.18.17"),sQuery(id+"F0.wireOp",EDGE,"E56.18.18"),sQuery(id+"F0.wireOp",EDGE,"E56.18.19"),sQuery(id+"F0.wireOp",EDGE,"E56.18.20"),sQuery(id+"F0.wireOp",EDGE,"E56.18.21"),sQuery(id+"F0.wireOp",EDGE,"E56.18.22"),sQuery(id+"F0.wireOp",EDGE,"E56.18.23"),sQuery(id+"F0.wireOp",EDGE,"E56.18.24"),sQuery(id+"F0.wireOp",EDGE,"E56.18.25"),sQuery(id+"F0.wireOp",EDGE,"E56.18.26"),sQuery(id+"F0.wireOp",EDGE,"E56.18.27"),sQuery(id+"F0.wireOp",EDGE,"E56.18.28"),sQuery(id+"F0.wireOp",EDGE,"E56.18.29"),sQuery(id+"F0.wireOp",EDGE,"E56.19.0"),sQuery(id+"F0.wireOp",EDGE,"E56.19.1"),sQuery(id+"F0.wireOp",EDGE,"E56.19.2"),sQuery(id+"F0.wireOp",EDGE,"E56.19.3"),sQuery(id+"F0.wireOp",EDGE,"E56.19.4"),sQuery(id+"F0.wireOp",EDGE,"E56.19.5"),sQuery(id+"F0.wireOp",EDGE,"E56.19.6"),sQuery(id+"F0.wireOp",EDGE,"E56.19.7"),sQuery(id+"F0.wireOp",EDGE,"E56.19.8"),sQuery(id+"F0.wireOp",EDGE,"E56.19.9"),sQuery(id+"F0.wireOp",EDGE,"E56.19.10"),sQuery(id+"F0.wireOp",EDGE,"E56.19.11"),sQuery(id+"F0.wireOp",EDGE,"E56.19.12"),sQuery(id+"F0.wireOp",EDGE,"E56.19.13"),sQuery(id+"F0.wireOp",EDGE,"E56.19.14"),sQuery(id+"F0.wireOp",EDGE,"E56.19.15"),sQuery(id+"F0.wireOp",EDGE,"E56.19.16"),sQuery(id+"F0.wireOp",EDGE,"E56.19.17"),sQuery(id+"F0.wireOp",EDGE,"E56.19.18"),sQuery(id+"F0.wireOp",EDGE,"E56.19.19"),sQuery(id+"F0.wireOp",EDGE,"E56.19.20"),sQuery(id+"F0.wireOp",EDGE,"E56.19.21"),sQuery(id+"F0.wireOp",EDGE,"E56.19.22"),sQuery(id+"F0.wireOp",EDGE,"E56.19.23"),sQuery(id+"F0.wireOp",EDGE,"E56.19.24"),sQuery(id+"F0.wireOp",EDGE,"E56.19.25"),sQuery(id+"F0.wireOp",EDGE,"E56.19.26"),sQuery(id+"F0.wireOp",EDGE,"E56.19.27"),sQuery(id+"F0.wireOp",EDGE,"E56.19.28"),sQuery(id+"F0.wireOp",EDGE,"E56.19.29")])]});
            var Q1;
            Q1=sQuery(id+"F0.wireOp",VERTEX,"E1.center");
            transform(context, id + "F4", {"entities" : qUnion([Q0]), "transformType" : TransformType.SCALE_UNIFORMLY, "scale" : 1.35, "scalePoint" : qUnion([Q1]), "makeCopy" : false});
        }
        {
            var Q0;
            Q0=makeQuery(id+"F1.opExtrude","SWEPT_BODY",BODY,{"disambiguationData":[OSD([sQuery(id+"F0.wireOp",EDGE,"E5"),sQuery(id+"F0.wireOp",EDGE,"E26"),sQuery(id+"F0.wireOp",EDGE,"E27.MirrorCS"),sQuery(id+"F0.wireOp",EDGE,"E28"),sQuery(id+"F0.wireOp",EDGE,"E29"),sQuery(id+"F0.wireOp",EDGE,"E30"),sQuery(id+"F0.wireOp",EDGE,"E31"),sQuery(id+"F0.wireOp",EDGE,"E32"),sQuery(id+"F0.wireOp",EDGE,"E33"),sQuery(id+"F0.wireOp",EDGE,"E34"),sQuery(id+"F0.wireOp",EDGE,"E35"),sQuery(id+"F0.wireOp",EDGE,"E36"),sQuery(id+"F0.wireOp",EDGE,"E37"),sQuery(id+"F0.wireOp",EDGE,"E38"),sQuery(id+"F0.wireOp",EDGE,"E39"),sQuery(id+"F0.wireOp",EDGE,"E40"),sQuery(id+"F0.wireOp",EDGE,"E41"),sQuery(id+"F0.wireOp",EDGE,"E42.MirrorCS"),sQuery(id+"F0.wireOp",EDGE,"E43.MirrorCS"),sQuery(id+"F0.wireOp",EDGE,"E44.MirrorCS"),sQuery(id+"F0.wireOp",EDGE,"E45.MirrorCS"),sQuery(id+"F0.wireOp",EDGE,"E46.MirrorCS"),sQuery(id+"F0.wireOp",EDGE,"E47.MirrorCS"),sQuery(id+"F0.wireOp",EDGE,"E48.MirrorCS"),sQuery(id+"F0.wireOp",EDGE,"E49.MirrorCS"),sQuery(id+"F0.wireOp",EDGE,"E50.MirrorCS"),sQuery(id+"F0.wireOp",EDGE,"E51.MirrorCS"),sQuery(id+"F0.wireOp",EDGE,"E52.MirrorCS"),sQuery(id+"F0.wireOp",EDGE,"E53.MirrorCS"),sQuery(id+"F0.wireOp",EDGE,"E54.MirrorCS"),sQuery(id+"F0.wireOp",EDGE,"E55.MirrorCS"),sQuery(id+"F0.wireOp",EDGE,"E56.1.0"),sQuery(id+"F0.wireOp",EDGE,"E56.1.1"),sQuery(id+"F0.wireOp",EDGE,"E56.1.2"),sQuery(id+"F0.wireOp",EDGE,"E56.1.3"),sQuery(id+"F0.wireOp",EDGE,"E56.1.4"),sQuery(id+"F0.wireOp",EDGE,"E56.1.5"),sQuery(id+"F0.wireOp",EDGE,"E56.1.6"),sQuery(id+"F0.wireOp",EDGE,"E56.1.7"),sQuery(id+"F0.wireOp",EDGE,"E56.1.8"),sQuery(id+"F0.wireOp",EDGE,"E56.1.9"),sQuery(id+"F0.wireOp",EDGE,"E56.1.10"),sQuery(id+"F0.wireOp",EDGE,"E56.1.11"),sQuery(id+"F0.wireOp",EDGE,"E56.1.12"),sQuery(id+"F0.wireOp",EDGE,"E56.1.13"),sQuery(id+"F0.wireOp",EDGE,"E56.1.14"),sQuery(id+"F0.wireOp",EDGE,"E56.1.15"),sQuery(id+"F0.wireOp",EDGE,"E56.1.16"),sQuery(id+"F0.wireOp",EDGE,"E56.1.17"),sQuery(id+"F0.wireOp",EDGE,"E56.1.18"),sQuery(id+"F0.wireOp",EDGE,"E56.1.19"),sQuery(id+"F0.wireOp",EDGE,"E56.1.20"),sQuery(id+"F0.wireOp",EDGE,"E56.1.21"),sQuery(id+"F0.wireOp",EDGE,"E56.1.22"),sQuery(id+"F0.wireOp",EDGE,"E56.1.23"),sQuery(id+"F0.wireOp",EDGE,"E56.1.24"),sQuery(id+"F0.wireOp",EDGE,"E56.1.25"),sQuery(id+"F0.wireOp",EDGE,"E56.1.26"),sQuery(id+"F0.wireOp",EDGE,"E56.1.27"),sQuery(id+"F0.wireOp",EDGE,"E56.1.28"),sQuery(id+"F0.wireOp",EDGE,"E56.1.29"),sQuery(id+"F0.wireOp",EDGE,"E56.2.0"),sQuery(id+"F0.wireOp",EDGE,"E56.2.1"),sQuery(id+"F0.wireOp",EDGE,"E56.2.2"),sQuery(id+"F0.wireOp",EDGE,"E56.2.3"),sQuery(id+"F0.wireOp",EDGE,"E56.2.4"),sQuery(id+"F0.wireOp",EDGE,"E56.2.5"),sQuery(id+"F0.wireOp",EDGE,"E56.2.6"),sQuery(id+"F0.wireOp",EDGE,"E56.2.7"),sQuery(id+"F0.wireOp",EDGE,"E56.2.8"),sQuery(id+"F0.wireOp",EDGE,"E56.2.9"),sQuery(id+"F0.wireOp",EDGE,"E56.2.10"),sQuery(id+"F0.wireOp",EDGE,"E56.2.11"),sQuery(id+"F0.wireOp",EDGE,"E56.2.12"),sQuery(id+"F0.wireOp",EDGE,"E56.2.13"),sQuery(id+"F0.wireOp",EDGE,"E56.2.14"),sQuery(id+"F0.wireOp",EDGE,"E56.2.15"),sQuery(id+"F0.wireOp",EDGE,"E56.2.16"),sQuery(id+"F0.wireOp",EDGE,"E56.2.17"),sQuery(id+"F0.wireOp",EDGE,"E56.2.18"),sQuery(id+"F0.wireOp",EDGE,"E56.2.19"),sQuery(id+"F0.wireOp",EDGE,"E56.2.20"),sQuery(id+"F0.wireOp",EDGE,"E56.2.21"),sQuery(id+"F0.wireOp",EDGE,"E56.2.22"),sQuery(id+"F0.wireOp",EDGE,"E56.2.23"),sQuery(id+"F0.wireOp",EDGE,"E56.2.24"),sQuery(id+"F0.wireOp",EDGE,"E56.2.25"),sQuery(id+"F0.wireOp",EDGE,"E56.2.26"),sQuery(id+"F0.wireOp",EDGE,"E56.2.27"),sQuery(id+"F0.wireOp",EDGE,"E56.2.28"),sQuery(id+"F0.wireOp",EDGE,"E56.2.29"),sQuery(id+"F0.wireOp",EDGE,"E56.3.0"),sQuery(id+"F0.wireOp",EDGE,"E56.3.1"),sQuery(id+"F0.wireOp",EDGE,"E56.3.2"),sQuery(id+"F0.wireOp",EDGE,"E56.3.3"),sQuery(id+"F0.wireOp",EDGE,"E56.3.4"),sQuery(id+"F0.wireOp",EDGE,"E56.3.5"),sQuery(id+"F0.wireOp",EDGE,"E56.3.6"),sQuery(id+"F0.wireOp",EDGE,"E56.3.7"),sQuery(id+"F0.wireOp",EDGE,"E56.3.8"),sQuery(id+"F0.wireOp",EDGE,"E56.3.9"),sQuery(id+"F0.wireOp",EDGE,"E56.3.10"),sQuery(id+"F0.wireOp",EDGE,"E56.3.11"),sQuery(id+"F0.wireOp",EDGE,"E56.3.12"),sQuery(id+"F0.wireOp",EDGE,"E56.3.13"),sQuery(id+"F0.wireOp",EDGE,"E56.3.14"),sQuery(id+"F0.wireOp",EDGE,"E56.3.15"),sQuery(id+"F0.wireOp",EDGE,"E56.3.16"),sQuery(id+"F0.wireOp",EDGE,"E56.3.17"),sQuery(id+"F0.wireOp",EDGE,"E56.3.18"),sQuery(id+"F0.wireOp",EDGE,"E56.3.19"),sQuery(id+"F0.wireOp",EDGE,"E56.3.20"),sQuery(id+"F0.wireOp",EDGE,"E56.3.21"),sQuery(id+"F0.wireOp",EDGE,"E56.3.22"),sQuery(id+"F0.wireOp",EDGE,"E56.3.23"),sQuery(id+"F0.wireOp",EDGE,"E56.3.24"),sQuery(id+"F0.wireOp",EDGE,"E56.3.25"),sQuery(id+"F0.wireOp",EDGE,"E56.3.26"),sQuery(id+"F0.wireOp",EDGE,"E56.3.27"),sQuery(id+"F0.wireOp",EDGE,"E56.3.28"),sQuery(id+"F0.wireOp",EDGE,"E56.3.29"),sQuery(id+"F0.wireOp",EDGE,"E56.4.0"),sQuery(id+"F0.wireOp",EDGE,"E56.4.1"),sQuery(id+"F0.wireOp",EDGE,"E56.4.2"),sQuery(id+"F0.wireOp",EDGE,"E56.4.3"),sQuery(id+"F0.wireOp",EDGE,"E56.4.4"),sQuery(id+"F0.wireOp",EDGE,"E56.4.5"),sQuery(id+"F0.wireOp",EDGE,"E56.4.6"),sQuery(id+"F0.wireOp",EDGE,"E56.4.7"),sQuery(id+"F0.wireOp",EDGE,"E56.4.8"),sQuery(id+"F0.wireOp",EDGE,"E56.4.9"),sQuery(id+"F0.wireOp",EDGE,"E56.4.10"),sQuery(id+"F0.wireOp",EDGE,"E56.4.11"),sQuery(id+"F0.wireOp",EDGE,"E56.4.12"),sQuery(id+"F0.wireOp",EDGE,"E56.4.13"),sQuery(id+"F0.wireOp",EDGE,"E56.4.14"),sQuery(id+"F0.wireOp",EDGE,"E56.4.15"),sQuery(id+"F0.wireOp",EDGE,"E56.4.16"),sQuery(id+"F0.wireOp",EDGE,"E56.4.17"),sQuery(id+"F0.wireOp",EDGE,"E56.4.18"),sQuery(id+"F0.wireOp",EDGE,"E56.4.19"),sQuery(id+"F0.wireOp",EDGE,"E56.4.20"),sQuery(id+"F0.wireOp",EDGE,"E56.4.21"),sQuery(id+"F0.wireOp",EDGE,"E56.4.22"),sQuery(id+"F0.wireOp",EDGE,"E56.4.23"),sQuery(id+"F0.wireOp",EDGE,"E56.4.24"),sQuery(id+"F0.wireOp",EDGE,"E56.4.25"),sQuery(id+"F0.wireOp",EDGE,"E56.4.26"),sQuery(id+"F0.wireOp",EDGE,"E56.4.27"),sQuery(id+"F0.wireOp",EDGE,"E56.4.28"),sQuery(id+"F0.wireOp",EDGE,"E56.4.29"),sQuery(id+"F0.wireOp",EDGE,"E56.5.0"),sQuery(id+"F0.wireOp",EDGE,"E56.5.1"),sQuery(id+"F0.wireOp",EDGE,"E56.5.2"),sQuery(id+"F0.wireOp",EDGE,"E56.5.3"),sQuery(id+"F0.wireOp",EDGE,"E56.5.4"),sQuery(id+"F0.wireOp",EDGE,"E56.5.5"),sQuery(id+"F0.wireOp",EDGE,"E56.5.6"),sQuery(id+"F0.wireOp",EDGE,"E56.5.7"),sQuery(id+"F0.wireOp",EDGE,"E56.5.8"),sQuery(id+"F0.wireOp",EDGE,"E56.5.9"),sQuery(id+"F0.wireOp",EDGE,"E56.5.10"),sQuery(id+"F0.wireOp",EDGE,"E56.5.11"),sQuery(id+"F0.wireOp",EDGE,"E56.5.12"),sQuery(id+"F0.wireOp",EDGE,"E56.5.13"),sQuery(id+"F0.wireOp",EDGE,"E56.5.14"),sQuery(id+"F0.wireOp",EDGE,"E56.5.15"),sQuery(id+"F0.wireOp",EDGE,"E56.5.16"),sQuery(id+"F0.wireOp",EDGE,"E56.5.17"),sQuery(id+"F0.wireOp",EDGE,"E56.5.18"),sQuery(id+"F0.wireOp",EDGE,"E56.5.19"),sQuery(id+"F0.wireOp",EDGE,"E56.5.20"),sQuery(id+"F0.wireOp",EDGE,"E56.5.21"),sQuery(id+"F0.wireOp",EDGE,"E56.5.22"),sQuery(id+"F0.wireOp",EDGE,"E56.5.23"),sQuery(id+"F0.wireOp",EDGE,"E56.5.24"),sQuery(id+"F0.wireOp",EDGE,"E56.5.25"),sQuery(id+"F0.wireOp",EDGE,"E56.5.26"),sQuery(id+"F0.wireOp",EDGE,"E56.5.27"),sQuery(id+"F0.wireOp",EDGE,"E56.5.28"),sQuery(id+"F0.wireOp",EDGE,"E56.5.29"),sQuery(id+"F0.wireOp",EDGE,"E56.6.0"),sQuery(id+"F0.wireOp",EDGE,"E56.6.1"),sQuery(id+"F0.wireOp",EDGE,"E56.6.2"),sQuery(id+"F0.wireOp",EDGE,"E56.6.3"),sQuery(id+"F0.wireOp",EDGE,"E56.6.4"),sQuery(id+"F0.wireOp",EDGE,"E56.6.5"),sQuery(id+"F0.wireOp",EDGE,"E56.6.6"),sQuery(id+"F0.wireOp",EDGE,"E56.6.7"),sQuery(id+"F0.wireOp",EDGE,"E56.6.8"),sQuery(id+"F0.wireOp",EDGE,"E56.6.9"),sQuery(id+"F0.wireOp",EDGE,"E56.6.10"),sQuery(id+"F0.wireOp",EDGE,"E56.6.11"),sQuery(id+"F0.wireOp",EDGE,"E56.6.12"),sQuery(id+"F0.wireOp",EDGE,"E56.6.13"),sQuery(id+"F0.wireOp",EDGE,"E56.6.14"),sQuery(id+"F0.wireOp",EDGE,"E56.6.15"),sQuery(id+"F0.wireOp",EDGE,"E56.6.16"),sQuery(id+"F0.wireOp",EDGE,"E56.6.17"),sQuery(id+"F0.wireOp",EDGE,"E56.6.18"),sQuery(id+"F0.wireOp",EDGE,"E56.6.19"),sQuery(id+"F0.wireOp",EDGE,"E56.6.20"),sQuery(id+"F0.wireOp",EDGE,"E56.6.21"),sQuery(id+"F0.wireOp",EDGE,"E56.6.22"),sQuery(id+"F0.wireOp",EDGE,"E56.6.23"),sQuery(id+"F0.wireOp",EDGE,"E56.6.24"),sQuery(id+"F0.wireOp",EDGE,"E56.6.25"),sQuery(id+"F0.wireOp",EDGE,"E56.6.26"),sQuery(id+"F0.wireOp",EDGE,"E56.6.27"),sQuery(id+"F0.wireOp",EDGE,"E56.6.28"),sQuery(id+"F0.wireOp",EDGE,"E56.6.29"),sQuery(id+"F0.wireOp",EDGE,"E56.7.0"),sQuery(id+"F0.wireOp",EDGE,"E56.7.1"),sQuery(id+"F0.wireOp",EDGE,"E56.7.2"),sQuery(id+"F0.wireOp",EDGE,"E56.7.3"),sQuery(id+"F0.wireOp",EDGE,"E56.7.4"),sQuery(id+"F0.wireOp",EDGE,"E56.7.5"),sQuery(id+"F0.wireOp",EDGE,"E56.7.6"),sQuery(id+"F0.wireOp",EDGE,"E56.7.7"),sQuery(id+"F0.wireOp",EDGE,"E56.7.8"),sQuery(id+"F0.wireOp",EDGE,"E56.7.9"),sQuery(id+"F0.wireOp",EDGE,"E56.7.10"),sQuery(id+"F0.wireOp",EDGE,"E56.7.11"),sQuery(id+"F0.wireOp",EDGE,"E56.7.12"),sQuery(id+"F0.wireOp",EDGE,"E56.7.13"),sQuery(id+"F0.wireOp",EDGE,"E56.7.14"),sQuery(id+"F0.wireOp",EDGE,"E56.7.15"),sQuery(id+"F0.wireOp",EDGE,"E56.7.16"),sQuery(id+"F0.wireOp",EDGE,"E56.7.17"),sQuery(id+"F0.wireOp",EDGE,"E56.7.18"),sQuery(id+"F0.wireOp",EDGE,"E56.7.19"),sQuery(id+"F0.wireOp",EDGE,"E56.7.20"),sQuery(id+"F0.wireOp",EDGE,"E56.7.21"),sQuery(id+"F0.wireOp",EDGE,"E56.7.22"),sQuery(id+"F0.wireOp",EDGE,"E56.7.23"),sQuery(id+"F0.wireOp",EDGE,"E56.7.24"),sQuery(id+"F0.wireOp",EDGE,"E56.7.25"),sQuery(id+"F0.wireOp",EDGE,"E56.7.26"),sQuery(id+"F0.wireOp",EDGE,"E56.7.27"),sQuery(id+"F0.wireOp",EDGE,"E56.7.28"),sQuery(id+"F0.wireOp",EDGE,"E56.7.29"),sQuery(id+"F0.wireOp",EDGE,"E56.8.0"),sQuery(id+"F0.wireOp",EDGE,"E56.8.1"),sQuery(id+"F0.wireOp",EDGE,"E56.8.2"),sQuery(id+"F0.wireOp",EDGE,"E56.8.3"),sQuery(id+"F0.wireOp",EDGE,"E56.8.4"),sQuery(id+"F0.wireOp",EDGE,"E56.8.5"),sQuery(id+"F0.wireOp",EDGE,"E56.8.6"),sQuery(id+"F0.wireOp",EDGE,"E56.8.7"),sQuery(id+"F0.wireOp",EDGE,"E56.8.8"),sQuery(id+"F0.wireOp",EDGE,"E56.8.9"),sQuery(id+"F0.wireOp",EDGE,"E56.8.10"),sQuery(id+"F0.wireOp",EDGE,"E56.8.11"),sQuery(id+"F0.wireOp",EDGE,"E56.8.12"),sQuery(id+"F0.wireOp",EDGE,"E56.8.13"),sQuery(id+"F0.wireOp",EDGE,"E56.8.14"),sQuery(id+"F0.wireOp",EDGE,"E56.8.15"),sQuery(id+"F0.wireOp",EDGE,"E56.8.16"),sQuery(id+"F0.wireOp",EDGE,"E56.8.17"),sQuery(id+"F0.wireOp",EDGE,"E56.8.18"),sQuery(id+"F0.wireOp",EDGE,"E56.8.19"),sQuery(id+"F0.wireOp",EDGE,"E56.8.20"),sQuery(id+"F0.wireOp",EDGE,"E56.8.21"),sQuery(id+"F0.wireOp",EDGE,"E56.8.22"),sQuery(id+"F0.wireOp",EDGE,"E56.8.23"),sQuery(id+"F0.wireOp",EDGE,"E56.8.24"),sQuery(id+"F0.wireOp",EDGE,"E56.8.25"),sQuery(id+"F0.wireOp",EDGE,"E56.8.26"),sQuery(id+"F0.wireOp",EDGE,"E56.8.27"),sQuery(id+"F0.wireOp",EDGE,"E56.8.28"),sQuery(id+"F0.wireOp",EDGE,"E56.8.29"),sQuery(id+"F0.wireOp",EDGE,"E56.9.0"),sQuery(id+"F0.wireOp",EDGE,"E56.9.1"),sQuery(id+"F0.wireOp",EDGE,"E56.9.2"),sQuery(id+"F0.wireOp",EDGE,"E56.9.3"),sQuery(id+"F0.wireOp",EDGE,"E56.9.4"),sQuery(id+"F0.wireOp",EDGE,"E56.9.5"),sQuery(id+"F0.wireOp",EDGE,"E56.9.6"),sQuery(id+"F0.wireOp",EDGE,"E56.9.7"),sQuery(id+"F0.wireOp",EDGE,"E56.9.8"),sQuery(id+"F0.wireOp",EDGE,"E56.9.9"),sQuery(id+"F0.wireOp",EDGE,"E56.9.10"),sQuery(id+"F0.wireOp",EDGE,"E56.9.11"),sQuery(id+"F0.wireOp",EDGE,"E56.9.12"),sQuery(id+"F0.wireOp",EDGE,"E56.9.13"),sQuery(id+"F0.wireOp",EDGE,"E56.9.14"),sQuery(id+"F0.wireOp",EDGE,"E56.9.15"),sQuery(id+"F0.wireOp",EDGE,"E56.9.16"),sQuery(id+"F0.wireOp",EDGE,"E56.9.17"),sQuery(id+"F0.wireOp",EDGE,"E56.9.18"),sQuery(id+"F0.wireOp",EDGE,"E56.9.19"),sQuery(id+"F0.wireOp",EDGE,"E56.9.20"),sQuery(id+"F0.wireOp",EDGE,"E56.9.21"),sQuery(id+"F0.wireOp",EDGE,"E56.9.22"),sQuery(id+"F0.wireOp",EDGE,"E56.9.23"),sQuery(id+"F0.wireOp",EDGE,"E56.9.24"),sQuery(id+"F0.wireOp",EDGE,"E56.9.25"),sQuery(id+"F0.wireOp",EDGE,"E56.9.26"),sQuery(id+"F0.wireOp",EDGE,"E56.9.27"),sQuery(id+"F0.wireOp",EDGE,"E56.9.28"),sQuery(id+"F0.wireOp",EDGE,"E56.9.29"),sQuery(id+"F0.wireOp",EDGE,"E56.10.0"),sQuery(id+"F0.wireOp",EDGE,"E56.10.1"),sQuery(id+"F0.wireOp",EDGE,"E56.10.2"),sQuery(id+"F0.wireOp",EDGE,"E56.10.3"),sQuery(id+"F0.wireOp",EDGE,"E56.10.4"),sQuery(id+"F0.wireOp",EDGE,"E56.10.5"),sQuery(id+"F0.wireOp",EDGE,"E56.10.6"),sQuery(id+"F0.wireOp",EDGE,"E56.10.7"),sQuery(id+"F0.wireOp",EDGE,"E56.10.8"),sQuery(id+"F0.wireOp",EDGE,"E56.10.9"),sQuery(id+"F0.wireOp",EDGE,"E56.10.10"),sQuery(id+"F0.wireOp",EDGE,"E56.10.11"),sQuery(id+"F0.wireOp",EDGE,"E56.10.12"),sQuery(id+"F0.wireOp",EDGE,"E56.10.13"),sQuery(id+"F0.wireOp",EDGE,"E56.10.14"),sQuery(id+"F0.wireOp",EDGE,"E56.10.15"),sQuery(id+"F0.wireOp",EDGE,"E56.10.16"),sQuery(id+"F0.wireOp",EDGE,"E56.10.17"),sQuery(id+"F0.wireOp",EDGE,"E56.10.18"),sQuery(id+"F0.wireOp",EDGE,"E56.10.19"),sQuery(id+"F0.wireOp",EDGE,"E56.10.20"),sQuery(id+"F0.wireOp",EDGE,"E56.10.21"),sQuery(id+"F0.wireOp",EDGE,"E56.10.22"),sQuery(id+"F0.wireOp",EDGE,"E56.10.23"),sQuery(id+"F0.wireOp",EDGE,"E56.10.24"),sQuery(id+"F0.wireOp",EDGE,"E56.10.25"),sQuery(id+"F0.wireOp",EDGE,"E56.10.26"),sQuery(id+"F0.wireOp",EDGE,"E56.10.27"),sQuery(id+"F0.wireOp",EDGE,"E56.10.28"),sQuery(id+"F0.wireOp",EDGE,"E56.10.29"),sQuery(id+"F0.wireOp",EDGE,"E56.11.0"),sQuery(id+"F0.wireOp",EDGE,"E56.11.1"),sQuery(id+"F0.wireOp",EDGE,"E56.11.2"),sQuery(id+"F0.wireOp",EDGE,"E56.11.3"),sQuery(id+"F0.wireOp",EDGE,"E56.11.4"),sQuery(id+"F0.wireOp",EDGE,"E56.11.5"),sQuery(id+"F0.wireOp",EDGE,"E56.11.6"),sQuery(id+"F0.wireOp",EDGE,"E56.11.7"),sQuery(id+"F0.wireOp",EDGE,"E56.11.8"),sQuery(id+"F0.wireOp",EDGE,"E56.11.9"),sQuery(id+"F0.wireOp",EDGE,"E56.11.10"),sQuery(id+"F0.wireOp",EDGE,"E56.11.11"),sQuery(id+"F0.wireOp",EDGE,"E56.11.12"),sQuery(id+"F0.wireOp",EDGE,"E56.11.13"),sQuery(id+"F0.wireOp",EDGE,"E56.11.14"),sQuery(id+"F0.wireOp",EDGE,"E56.11.15"),sQuery(id+"F0.wireOp",EDGE,"E56.11.16"),sQuery(id+"F0.wireOp",EDGE,"E56.11.17"),sQuery(id+"F0.wireOp",EDGE,"E56.11.18"),sQuery(id+"F0.wireOp",EDGE,"E56.11.19"),sQuery(id+"F0.wireOp",EDGE,"E56.11.20"),sQuery(id+"F0.wireOp",EDGE,"E56.11.21"),sQuery(id+"F0.wireOp",EDGE,"E56.11.22"),sQuery(id+"F0.wireOp",EDGE,"E56.11.23"),sQuery(id+"F0.wireOp",EDGE,"E56.11.24"),sQuery(id+"F0.wireOp",EDGE,"E56.11.25"),sQuery(id+"F0.wireOp",EDGE,"E56.11.26"),sQuery(id+"F0.wireOp",EDGE,"E56.11.27"),sQuery(id+"F0.wireOp",EDGE,"E56.11.28"),sQuery(id+"F0.wireOp",EDGE,"E56.11.29"),sQuery(id+"F0.wireOp",EDGE,"E56.12.0"),sQuery(id+"F0.wireOp",EDGE,"E56.12.1"),sQuery(id+"F0.wireOp",EDGE,"E56.12.2"),sQuery(id+"F0.wireOp",EDGE,"E56.12.3"),sQuery(id+"F0.wireOp",EDGE,"E56.12.4"),sQuery(id+"F0.wireOp",EDGE,"E56.12.5"),sQuery(id+"F0.wireOp",EDGE,"E56.12.6"),sQuery(id+"F0.wireOp",EDGE,"E56.12.7"),sQuery(id+"F0.wireOp",EDGE,"E56.12.8"),sQuery(id+"F0.wireOp",EDGE,"E56.12.9"),sQuery(id+"F0.wireOp",EDGE,"E56.12.10"),sQuery(id+"F0.wireOp",EDGE,"E56.12.11"),sQuery(id+"F0.wireOp",EDGE,"E56.12.12"),sQuery(id+"F0.wireOp",EDGE,"E56.12.13"),sQuery(id+"F0.wireOp",EDGE,"E56.12.14"),sQuery(id+"F0.wireOp",EDGE,"E56.12.15"),sQuery(id+"F0.wireOp",EDGE,"E56.12.16"),sQuery(id+"F0.wireOp",EDGE,"E56.12.17"),sQuery(id+"F0.wireOp",EDGE,"E56.12.18"),sQuery(id+"F0.wireOp",EDGE,"E56.12.19"),sQuery(id+"F0.wireOp",EDGE,"E56.12.20"),sQuery(id+"F0.wireOp",EDGE,"E56.12.21"),sQuery(id+"F0.wireOp",EDGE,"E56.12.22"),sQuery(id+"F0.wireOp",EDGE,"E56.12.23"),sQuery(id+"F0.wireOp",EDGE,"E56.12.24"),sQuery(id+"F0.wireOp",EDGE,"E56.12.25"),sQuery(id+"F0.wireOp",EDGE,"E56.12.26"),sQuery(id+"F0.wireOp",EDGE,"E56.12.27"),sQuery(id+"F0.wireOp",EDGE,"E56.12.28"),sQuery(id+"F0.wireOp",EDGE,"E56.12.29"),sQuery(id+"F0.wireOp",EDGE,"E56.13.0"),sQuery(id+"F0.wireOp",EDGE,"E56.13.1"),sQuery(id+"F0.wireOp",EDGE,"E56.13.2"),sQuery(id+"F0.wireOp",EDGE,"E56.13.3"),sQuery(id+"F0.wireOp",EDGE,"E56.13.4"),sQuery(id+"F0.wireOp",EDGE,"E56.13.5"),sQuery(id+"F0.wireOp",EDGE,"E56.13.6"),sQuery(id+"F0.wireOp",EDGE,"E56.13.7"),sQuery(id+"F0.wireOp",EDGE,"E56.13.8"),sQuery(id+"F0.wireOp",EDGE,"E56.13.9"),sQuery(id+"F0.wireOp",EDGE,"E56.13.10"),sQuery(id+"F0.wireOp",EDGE,"E56.13.11"),sQuery(id+"F0.wireOp",EDGE,"E56.13.12"),sQuery(id+"F0.wireOp",EDGE,"E56.13.13"),sQuery(id+"F0.wireOp",EDGE,"E56.13.14"),sQuery(id+"F0.wireOp",EDGE,"E56.13.15"),sQuery(id+"F0.wireOp",EDGE,"E56.13.16"),sQuery(id+"F0.wireOp",EDGE,"E56.13.17"),sQuery(id+"F0.wireOp",EDGE,"E56.13.18"),sQuery(id+"F0.wireOp",EDGE,"E56.13.19"),sQuery(id+"F0.wireOp",EDGE,"E56.13.20"),sQuery(id+"F0.wireOp",EDGE,"E56.13.21"),sQuery(id+"F0.wireOp",EDGE,"E56.13.22"),sQuery(id+"F0.wireOp",EDGE,"E56.13.23"),sQuery(id+"F0.wireOp",EDGE,"E56.13.24"),sQuery(id+"F0.wireOp",EDGE,"E56.13.25"),sQuery(id+"F0.wireOp",EDGE,"E56.13.26"),sQuery(id+"F0.wireOp",EDGE,"E56.13.27"),sQuery(id+"F0.wireOp",EDGE,"E56.13.28"),sQuery(id+"F0.wireOp",EDGE,"E56.13.29"),sQuery(id+"F0.wireOp",EDGE,"E56.14.0"),sQuery(id+"F0.wireOp",EDGE,"E56.14.1"),sQuery(id+"F0.wireOp",EDGE,"E56.14.2"),sQuery(id+"F0.wireOp",EDGE,"E56.14.3"),sQuery(id+"F0.wireOp",EDGE,"E56.14.4"),sQuery(id+"F0.wireOp",EDGE,"E56.14.5"),sQuery(id+"F0.wireOp",EDGE,"E56.14.6"),sQuery(id+"F0.wireOp",EDGE,"E56.14.7"),sQuery(id+"F0.wireOp",EDGE,"E56.14.8"),sQuery(id+"F0.wireOp",EDGE,"E56.14.9"),sQuery(id+"F0.wireOp",EDGE,"E56.14.10"),sQuery(id+"F0.wireOp",EDGE,"E56.14.11"),sQuery(id+"F0.wireOp",EDGE,"E56.14.12"),sQuery(id+"F0.wireOp",EDGE,"E56.14.13"),sQuery(id+"F0.wireOp",EDGE,"E56.14.14"),sQuery(id+"F0.wireOp",EDGE,"E56.14.15"),sQuery(id+"F0.wireOp",EDGE,"E56.14.16"),sQuery(id+"F0.wireOp",EDGE,"E56.14.17"),sQuery(id+"F0.wireOp",EDGE,"E56.14.18"),sQuery(id+"F0.wireOp",EDGE,"E56.14.19"),sQuery(id+"F0.wireOp",EDGE,"E56.14.20"),sQuery(id+"F0.wireOp",EDGE,"E56.14.21"),sQuery(id+"F0.wireOp",EDGE,"E56.14.22"),sQuery(id+"F0.wireOp",EDGE,"E56.14.23"),sQuery(id+"F0.wireOp",EDGE,"E56.14.24"),sQuery(id+"F0.wireOp",EDGE,"E56.14.25"),sQuery(id+"F0.wireOp",EDGE,"E56.14.26"),sQuery(id+"F0.wireOp",EDGE,"E56.14.27"),sQuery(id+"F0.wireOp",EDGE,"E56.14.28"),sQuery(id+"F0.wireOp",EDGE,"E56.14.29"),sQuery(id+"F0.wireOp",EDGE,"E56.15.0"),sQuery(id+"F0.wireOp",EDGE,"E56.15.1"),sQuery(id+"F0.wireOp",EDGE,"E56.15.2"),sQuery(id+"F0.wireOp",EDGE,"E56.15.3"),sQuery(id+"F0.wireOp",EDGE,"E56.15.4"),sQuery(id+"F0.wireOp",EDGE,"E56.15.5"),sQuery(id+"F0.wireOp",EDGE,"E56.15.6"),sQuery(id+"F0.wireOp",EDGE,"E56.15.7"),sQuery(id+"F0.wireOp",EDGE,"E56.15.8"),sQuery(id+"F0.wireOp",EDGE,"E56.15.9"),sQuery(id+"F0.wireOp",EDGE,"E56.15.10"),sQuery(id+"F0.wireOp",EDGE,"E56.15.11"),sQuery(id+"F0.wireOp",EDGE,"E56.15.12"),sQuery(id+"F0.wireOp",EDGE,"E56.15.13"),sQuery(id+"F0.wireOp",EDGE,"E56.15.14"),sQuery(id+"F0.wireOp",EDGE,"E56.15.15"),sQuery(id+"F0.wireOp",EDGE,"E56.15.16"),sQuery(id+"F0.wireOp",EDGE,"E56.15.17"),sQuery(id+"F0.wireOp",EDGE,"E56.15.18"),sQuery(id+"F0.wireOp",EDGE,"E56.15.19"),sQuery(id+"F0.wireOp",EDGE,"E56.15.20"),sQuery(id+"F0.wireOp",EDGE,"E56.15.21"),sQuery(id+"F0.wireOp",EDGE,"E56.15.22"),sQuery(id+"F0.wireOp",EDGE,"E56.15.23"),sQuery(id+"F0.wireOp",EDGE,"E56.15.24"),sQuery(id+"F0.wireOp",EDGE,"E56.15.25"),sQuery(id+"F0.wireOp",EDGE,"E56.15.26"),sQuery(id+"F0.wireOp",EDGE,"E56.15.27"),sQuery(id+"F0.wireOp",EDGE,"E56.15.28"),sQuery(id+"F0.wireOp",EDGE,"E56.15.29"),sQuery(id+"F0.wireOp",EDGE,"E56.16.0"),sQuery(id+"F0.wireOp",EDGE,"E56.16.1"),sQuery(id+"F0.wireOp",EDGE,"E56.16.2"),sQuery(id+"F0.wireOp",EDGE,"E56.16.3"),sQuery(id+"F0.wireOp",EDGE,"E56.16.4"),sQuery(id+"F0.wireOp",EDGE,"E56.16.5"),sQuery(id+"F0.wireOp",EDGE,"E56.16.6"),sQuery(id+"F0.wireOp",EDGE,"E56.16.7"),sQuery(id+"F0.wireOp",EDGE,"E56.16.8"),sQuery(id+"F0.wireOp",EDGE,"E56.16.9"),sQuery(id+"F0.wireOp",EDGE,"E56.16.10"),sQuery(id+"F0.wireOp",EDGE,"E56.16.11"),sQuery(id+"F0.wireOp",EDGE,"E56.16.12"),sQuery(id+"F0.wireOp",EDGE,"E56.16.13"),sQuery(id+"F0.wireOp",EDGE,"E56.16.14"),sQuery(id+"F0.wireOp",EDGE,"E56.16.15"),sQuery(id+"F0.wireOp",EDGE,"E56.16.16"),sQuery(id+"F0.wireOp",EDGE,"E56.16.17"),sQuery(id+"F0.wireOp",EDGE,"E56.16.18"),sQuery(id+"F0.wireOp",EDGE,"E56.16.19"),sQuery(id+"F0.wireOp",EDGE,"E56.16.20"),sQuery(id+"F0.wireOp",EDGE,"E56.16.21"),sQuery(id+"F0.wireOp",EDGE,"E56.16.22"),sQuery(id+"F0.wireOp",EDGE,"E56.16.23"),sQuery(id+"F0.wireOp",EDGE,"E56.16.24"),sQuery(id+"F0.wireOp",EDGE,"E56.16.25"),sQuery(id+"F0.wireOp",EDGE,"E56.16.26"),sQuery(id+"F0.wireOp",EDGE,"E56.16.27"),sQuery(id+"F0.wireOp",EDGE,"E56.16.28"),sQuery(id+"F0.wireOp",EDGE,"E56.16.29"),sQuery(id+"F0.wireOp",EDGE,"E56.17.0"),sQuery(id+"F0.wireOp",EDGE,"E56.17.1"),sQuery(id+"F0.wireOp",EDGE,"E56.17.2"),sQuery(id+"F0.wireOp",EDGE,"E56.17.3"),sQuery(id+"F0.wireOp",EDGE,"E56.17.4"),sQuery(id+"F0.wireOp",EDGE,"E56.17.5"),sQuery(id+"F0.wireOp",EDGE,"E56.17.6"),sQuery(id+"F0.wireOp",EDGE,"E56.17.7"),sQuery(id+"F0.wireOp",EDGE,"E56.17.8"),sQuery(id+"F0.wireOp",EDGE,"E56.17.9"),sQuery(id+"F0.wireOp",EDGE,"E56.17.10"),sQuery(id+"F0.wireOp",EDGE,"E56.17.11"),sQuery(id+"F0.wireOp",EDGE,"E56.17.12"),sQuery(id+"F0.wireOp",EDGE,"E56.17.13"),sQuery(id+"F0.wireOp",EDGE,"E56.17.14"),sQuery(id+"F0.wireOp",EDGE,"E56.17.15"),sQuery(id+"F0.wireOp",EDGE,"E56.17.16"),sQuery(id+"F0.wireOp",EDGE,"E56.17.17"),sQuery(id+"F0.wireOp",EDGE,"E56.17.18"),sQuery(id+"F0.wireOp",EDGE,"E56.17.19"),sQuery(id+"F0.wireOp",EDGE,"E56.17.20"),sQuery(id+"F0.wireOp",EDGE,"E56.17.21"),sQuery(id+"F0.wireOp",EDGE,"E56.17.22"),sQuery(id+"F0.wireOp",EDGE,"E56.17.23"),sQuery(id+"F0.wireOp",EDGE,"E56.17.24"),sQuery(id+"F0.wireOp",EDGE,"E56.17.25"),sQuery(id+"F0.wireOp",EDGE,"E56.17.26"),sQuery(id+"F0.wireOp",EDGE,"E56.17.27"),sQuery(id+"F0.wireOp",EDGE,"E56.17.28"),sQuery(id+"F0.wireOp",EDGE,"E56.17.29"),sQuery(id+"F0.wireOp",EDGE,"E56.18.0"),sQuery(id+"F0.wireOp",EDGE,"E56.18.1"),sQuery(id+"F0.wireOp",EDGE,"E56.18.2"),sQuery(id+"F0.wireOp",EDGE,"E56.18.3"),sQuery(id+"F0.wireOp",EDGE,"E56.18.4"),sQuery(id+"F0.wireOp",EDGE,"E56.18.5"),sQuery(id+"F0.wireOp",EDGE,"E56.18.6"),sQuery(id+"F0.wireOp",EDGE,"E56.18.7"),sQuery(id+"F0.wireOp",EDGE,"E56.18.8"),sQuery(id+"F0.wireOp",EDGE,"E56.18.9"),sQuery(id+"F0.wireOp",EDGE,"E56.18.10"),sQuery(id+"F0.wireOp",EDGE,"E56.18.11"),sQuery(id+"F0.wireOp",EDGE,"E56.18.12"),sQuery(id+"F0.wireOp",EDGE,"E56.18.13"),sQuery(id+"F0.wireOp",EDGE,"E56.18.14"),sQuery(id+"F0.wireOp",EDGE,"E56.18.15"),sQuery(id+"F0.wireOp",EDGE,"E56.18.16"),sQuery(id+"F0.wireOp",EDGE,"E56.18.17"),sQuery(id+"F0.wireOp",EDGE,"E56.18.18"),sQuery(id+"F0.wireOp",EDGE,"E56.18.19"),sQuery(id+"F0.wireOp",EDGE,"E56.18.20"),sQuery(id+"F0.wireOp",EDGE,"E56.18.21"),sQuery(id+"F0.wireOp",EDGE,"E56.18.22"),sQuery(id+"F0.wireOp",EDGE,"E56.18.23"),sQuery(id+"F0.wireOp",EDGE,"E56.18.24"),sQuery(id+"F0.wireOp",EDGE,"E56.18.25"),sQuery(id+"F0.wireOp",EDGE,"E56.18.26"),sQuery(id+"F0.wireOp",EDGE,"E56.18.27"),sQuery(id+"F0.wireOp",EDGE,"E56.18.28"),sQuery(id+"F0.wireOp",EDGE,"E56.18.29"),sQuery(id+"F0.wireOp",EDGE,"E56.19.0"),sQuery(id+"F0.wireOp",EDGE,"E56.19.1"),sQuery(id+"F0.wireOp",EDGE,"E56.19.2"),sQuery(id+"F0.wireOp",EDGE,"E56.19.3"),sQuery(id+"F0.wireOp",EDGE,"E56.19.4"),sQuery(id+"F0.wireOp",EDGE,"E56.19.5"),sQuery(id+"F0.wireOp",EDGE,"E56.19.6"),sQuery(id+"F0.wireOp",EDGE,"E56.19.7"),sQuery(id+"F0.wireOp",EDGE,"E56.19.8"),sQuery(id+"F0.wireOp",EDGE,"E56.19.9"),sQuery(id+"F0.wireOp",EDGE,"E56.19.10"),sQuery(id+"F0.wireOp",EDGE,"E56.19.11"),sQuery(id+"F0.wireOp",EDGE,"E56.19.12"),sQuery(id+"F0.wireOp",EDGE,"E56.19.13"),sQuery(id+"F0.wireOp",EDGE,"E56.19.14"),sQuery(id+"F0.wireOp",EDGE,"E56.19.15"),sQuery(id+"F0.wireOp",EDGE,"E56.19.16"),sQuery(id+"F0.wireOp",EDGE,"E56.19.17"),sQuery(id+"F0.wireOp",EDGE,"E56.19.18"),sQuery(id+"F0.wireOp",EDGE,"E56.19.19"),sQuery(id+"F0.wireOp",EDGE,"E56.19.20"),sQuery(id+"F0.wireOp",EDGE,"E56.19.21"),sQuery(id+"F0.wireOp",EDGE,"E56.19.22"),sQuery(id+"F0.wireOp",EDGE,"E56.19.23"),sQuery(id+"F0.wireOp",EDGE,"E56.19.24"),sQuery(id+"F0.wireOp",EDGE,"E56.19.25"),sQuery(id+"F0.wireOp",EDGE,"E56.19.26"),sQuery(id+"F0.wireOp",EDGE,"E56.19.27"),sQuery(id+"F0.wireOp",EDGE,"E56.19.28"),sQuery(id+"F0.wireOp",EDGE,"E56.19.29")])]});
            transform(context, id + "F5", {"entities" : qUnion([Q0]), "transformType" : TransformType.TRANSLATION_3D, "dx" : 45.2 * mm, "dy" : 0 * mm, "dz" : 0 * mm, "makeCopy" : true});
        }
        {
            var Q0;
            Q0=makeQuery(id+"F1.opExtrude","CAP_FACE",FACE,{"disambiguationData":[OSD([sQuery(id+"F0.wireOp",EDGE,"E5"),sQuery(id+"F0.wireOp",EDGE,"E26"),sQuery(id+"F0.wireOp",EDGE,"E27.MirrorCS"),sQuery(id+"F0.wireOp",EDGE,"E28"),sQuery(id+"F0.wireOp",EDGE,"E29"),sQuery(id+"F0.wireOp",EDGE,"E30"),sQuery(id+"F0.wireOp",EDGE,"E31"),sQuery(id+"F0.wireOp",EDGE,"E32"),sQuery(id+"F0.wireOp",EDGE,"E33"),sQuery(id+"F0.wireOp",EDGE,"E34"),sQuery(id+"F0.wireOp",EDGE,"E35"),sQuery(id+"F0.wireOp",EDGE,"E36"),sQuery(id+"F0.wireOp",EDGE,"E37"),sQuery(id+"F0.wireOp",EDGE,"E38"),sQuery(id+"F0.wireOp",EDGE,"E39"),sQuery(id+"F0.wireOp",EDGE,"E40"),sQuery(id+"F0.wireOp",EDGE,"E41"),sQuery(id+"F0.wireOp",EDGE,"E42.MirrorCS"),sQuery(id+"F0.wireOp",EDGE,"E43.MirrorCS"),sQuery(id+"F0.wireOp",EDGE,"E44.MirrorCS"),sQuery(id+"F0.wireOp",EDGE,"E45.MirrorCS"),sQuery(id+"F0.wireOp",EDGE,"E46.MirrorCS"),sQuery(id+"F0.wireOp",EDGE,"E47.MirrorCS"),sQuery(id+"F0.wireOp",EDGE,"E48.MirrorCS"),sQuery(id+"F0.wireOp",EDGE,"E49.MirrorCS"),sQuery(id+"F0.wireOp",EDGE,"E50.MirrorCS"),sQuery(id+"F0.wireOp",EDGE,"E51.MirrorCS"),sQuery(id+"F0.wireOp",EDGE,"E52.MirrorCS"),sQuery(id+"F0.wireOp",EDGE,"E53.MirrorCS"),sQuery(id+"F0.wireOp",EDGE,"E54.MirrorCS"),sQuery(id+"F0.wireOp",EDGE,"E55.MirrorCS"),sQuery(id+"F0.wireOp",EDGE,"E56.1.0"),sQuery(id+"F0.wireOp",EDGE,"E56.1.1"),sQuery(id+"F0.wireOp",EDGE,"E56.1.2"),sQuery(id+"F0.wireOp",EDGE,"E56.1.3"),sQuery(id+"F0.wireOp",EDGE,"E56.1.4"),sQuery(id+"F0.wireOp",EDGE,"E56.1.5"),sQuery(id+"F0.wireOp",EDGE,"E56.1.6"),sQuery(id+"F0.wireOp",EDGE,"E56.1.7"),sQuery(id+"F0.wireOp",EDGE,"E56.1.8"),sQuery(id+"F0.wireOp",EDGE,"E56.1.9"),sQuery(id+"F0.wireOp",EDGE,"E56.1.10"),sQuery(id+"F0.wireOp",EDGE,"E56.1.11"),sQuery(id+"F0.wireOp",EDGE,"E56.1.12"),sQuery(id+"F0.wireOp",EDGE,"E56.1.13"),sQuery(id+"F0.wireOp",EDGE,"E56.1.14"),sQuery(id+"F0.wireOp",EDGE,"E56.1.15"),sQuery(id+"F0.wireOp",EDGE,"E56.1.16"),sQuery(id+"F0.wireOp",EDGE,"E56.1.17"),sQuery(id+"F0.wireOp",EDGE,"E56.1.18"),sQuery(id+"F0.wireOp",EDGE,"E56.1.19"),sQuery(id+"F0.wireOp",EDGE,"E56.1.20"),sQuery(id+"F0.wireOp",EDGE,"E56.1.21"),sQuery(id+"F0.wireOp",EDGE,"E56.1.22"),sQuery(id+"F0.wireOp",EDGE,"E56.1.23"),sQuery(id+"F0.wireOp",EDGE,"E56.1.24"),sQuery(id+"F0.wireOp",EDGE,"E56.1.25"),sQuery(id+"F0.wireOp",EDGE,"E56.1.26"),sQuery(id+"F0.wireOp",EDGE,"E56.1.27"),sQuery(id+"F0.wireOp",EDGE,"E56.1.28"),sQuery(id+"F0.wireOp",EDGE,"E56.1.29"),sQuery(id+"F0.wireOp",EDGE,"E56.2.0"),sQuery(id+"F0.wireOp",EDGE,"E56.2.1"),sQuery(id+"F0.wireOp",EDGE,"E56.2.2"),sQuery(id+"F0.wireOp",EDGE,"E56.2.3"),sQuery(id+"F0.wireOp",EDGE,"E56.2.4"),sQuery(id+"F0.wireOp",EDGE,"E56.2.5"),sQuery(id+"F0.wireOp",EDGE,"E56.2.6"),sQuery(id+"F0.wireOp",EDGE,"E56.2.7"),sQuery(id+"F0.wireOp",EDGE,"E56.2.8"),sQuery(id+"F0.wireOp",EDGE,"E56.2.9"),sQuery(id+"F0.wireOp",EDGE,"E56.2.10"),sQuery(id+"F0.wireOp",EDGE,"E56.2.11"),sQuery(id+"F0.wireOp",EDGE,"E56.2.12"),sQuery(id+"F0.wireOp",EDGE,"E56.2.13"),sQuery(id+"F0.wireOp",EDGE,"E56.2.14"),sQuery(id+"F0.wireOp",EDGE,"E56.2.15"),sQuery(id+"F0.wireOp",EDGE,"E56.2.16"),sQuery(id+"F0.wireOp",EDGE,"E56.2.17"),sQuery(id+"F0.wireOp",EDGE,"E56.2.18"),sQuery(id+"F0.wireOp",EDGE,"E56.2.19"),sQuery(id+"F0.wireOp",EDGE,"E56.2.20"),sQuery(id+"F0.wireOp",EDGE,"E56.2.21"),sQuery(id+"F0.wireOp",EDGE,"E56.2.22"),sQuery(id+"F0.wireOp",EDGE,"E56.2.23"),sQuery(id+"F0.wireOp",EDGE,"E56.2.24"),sQuery(id+"F0.wireOp",EDGE,"E56.2.25"),sQuery(id+"F0.wireOp",EDGE,"E56.2.26"),sQuery(id+"F0.wireOp",EDGE,"E56.2.27"),sQuery(id+"F0.wireOp",EDGE,"E56.2.28"),sQuery(id+"F0.wireOp",EDGE,"E56.2.29"),sQuery(id+"F0.wireOp",EDGE,"E56.3.0"),sQuery(id+"F0.wireOp",EDGE,"E56.3.1"),sQuery(id+"F0.wireOp",EDGE,"E56.3.2"),sQuery(id+"F0.wireOp",EDGE,"E56.3.3"),sQuery(id+"F0.wireOp",EDGE,"E56.3.4"),sQuery(id+"F0.wireOp",EDGE,"E56.3.5"),sQuery(id+"F0.wireOp",EDGE,"E56.3.6"),sQuery(id+"F0.wireOp",EDGE,"E56.3.7"),sQuery(id+"F0.wireOp",EDGE,"E56.3.8"),sQuery(id+"F0.wireOp",EDGE,"E56.3.9"),sQuery(id+"F0.wireOp",EDGE,"E56.3.10"),sQuery(id+"F0.wireOp",EDGE,"E56.3.11"),sQuery(id+"F0.wireOp",EDGE,"E56.3.12"),sQuery(id+"F0.wireOp",EDGE,"E56.3.13"),sQuery(id+"F0.wireOp",EDGE,"E56.3.14"),sQuery(id+"F0.wireOp",EDGE,"E56.3.15"),sQuery(id+"F0.wireOp",EDGE,"E56.3.16"),sQuery(id+"F0.wireOp",EDGE,"E56.3.17"),sQuery(id+"F0.wireOp",EDGE,"E56.3.18"),sQuery(id+"F0.wireOp",EDGE,"E56.3.19"),sQuery(id+"F0.wireOp",EDGE,"E56.3.20"),sQuery(id+"F0.wireOp",EDGE,"E56.3.21"),sQuery(id+"F0.wireOp",EDGE,"E56.3.22"),sQuery(id+"F0.wireOp",EDGE,"E56.3.23"),sQuery(id+"F0.wireOp",EDGE,"E56.3.24"),sQuery(id+"F0.wireOp",EDGE,"E56.3.25"),sQuery(id+"F0.wireOp",EDGE,"E56.3.26"),sQuery(id+"F0.wireOp",EDGE,"E56.3.27"),sQuery(id+"F0.wireOp",EDGE,"E56.3.28"),sQuery(id+"F0.wireOp",EDGE,"E56.3.29"),sQuery(id+"F0.wireOp",EDGE,"E56.4.0"),sQuery(id+"F0.wireOp",EDGE,"E56.4.1"),sQuery(id+"F0.wireOp",EDGE,"E56.4.2"),sQuery(id+"F0.wireOp",EDGE,"E56.4.3"),sQuery(id+"F0.wireOp",EDGE,"E56.4.4"),sQuery(id+"F0.wireOp",EDGE,"E56.4.5"),sQuery(id+"F0.wireOp",EDGE,"E56.4.6"),sQuery(id+"F0.wireOp",EDGE,"E56.4.7"),sQuery(id+"F0.wireOp",EDGE,"E56.4.8"),sQuery(id+"F0.wireOp",EDGE,"E56.4.9"),sQuery(id+"F0.wireOp",EDGE,"E56.4.10"),sQuery(id+"F0.wireOp",EDGE,"E56.4.11"),sQuery(id+"F0.wireOp",EDGE,"E56.4.12"),sQuery(id+"F0.wireOp",EDGE,"E56.4.13"),sQuery(id+"F0.wireOp",EDGE,"E56.4.14"),sQuery(id+"F0.wireOp",EDGE,"E56.4.15"),sQuery(id+"F0.wireOp",EDGE,"E56.4.16"),sQuery(id+"F0.wireOp",EDGE,"E56.4.17"),sQuery(id+"F0.wireOp",EDGE,"E56.4.18"),sQuery(id+"F0.wireOp",EDGE,"E56.4.19"),sQuery(id+"F0.wireOp",EDGE,"E56.4.20"),sQuery(id+"F0.wireOp",EDGE,"E56.4.21"),sQuery(id+"F0.wireOp",EDGE,"E56.4.22"),sQuery(id+"F0.wireOp",EDGE,"E56.4.23"),sQuery(id+"F0.wireOp",EDGE,"E56.4.24"),sQuery(id+"F0.wireOp",EDGE,"E56.4.25"),sQuery(id+"F0.wireOp",EDGE,"E56.4.26"),sQuery(id+"F0.wireOp",EDGE,"E56.4.27"),sQuery(id+"F0.wireOp",EDGE,"E56.4.28"),sQuery(id+"F0.wireOp",EDGE,"E56.4.29"),sQuery(id+"F0.wireOp",EDGE,"E56.5.0"),sQuery(id+"F0.wireOp",EDGE,"E56.5.1"),sQuery(id+"F0.wireOp",EDGE,"E56.5.2"),sQuery(id+"F0.wireOp",EDGE,"E56.5.3"),sQuery(id+"F0.wireOp",EDGE,"E56.5.4"),sQuery(id+"F0.wireOp",EDGE,"E56.5.5"),sQuery(id+"F0.wireOp",EDGE,"E56.5.6"),sQuery(id+"F0.wireOp",EDGE,"E56.5.7"),sQuery(id+"F0.wireOp",EDGE,"E56.5.8"),sQuery(id+"F0.wireOp",EDGE,"E56.5.9"),sQuery(id+"F0.wireOp",EDGE,"E56.5.10"),sQuery(id+"F0.wireOp",EDGE,"E56.5.11"),sQuery(id+"F0.wireOp",EDGE,"E56.5.12"),sQuery(id+"F0.wireOp",EDGE,"E56.5.13"),sQuery(id+"F0.wireOp",EDGE,"E56.5.14"),sQuery(id+"F0.wireOp",EDGE,"E56.5.15"),sQuery(id+"F0.wireOp",EDGE,"E56.5.16"),sQuery(id+"F0.wireOp",EDGE,"E56.5.17"),sQuery(id+"F0.wireOp",EDGE,"E56.5.18"),sQuery(id+"F0.wireOp",EDGE,"E56.5.19"),sQuery(id+"F0.wireOp",EDGE,"E56.5.20"),sQuery(id+"F0.wireOp",EDGE,"E56.5.21"),sQuery(id+"F0.wireOp",EDGE,"E56.5.22"),sQuery(id+"F0.wireOp",EDGE,"E56.5.23"),sQuery(id+"F0.wireOp",EDGE,"E56.5.24"),sQuery(id+"F0.wireOp",EDGE,"E56.5.25"),sQuery(id+"F0.wireOp",EDGE,"E56.5.26"),sQuery(id+"F0.wireOp",EDGE,"E56.5.27"),sQuery(id+"F0.wireOp",EDGE,"E56.5.28"),sQuery(id+"F0.wireOp",EDGE,"E56.5.29"),sQuery(id+"F0.wireOp",EDGE,"E56.6.0"),sQuery(id+"F0.wireOp",EDGE,"E56.6.1"),sQuery(id+"F0.wireOp",EDGE,"E56.6.2"),sQuery(id+"F0.wireOp",EDGE,"E56.6.3"),sQuery(id+"F0.wireOp",EDGE,"E56.6.4"),sQuery(id+"F0.wireOp",EDGE,"E56.6.5"),sQuery(id+"F0.wireOp",EDGE,"E56.6.6"),sQuery(id+"F0.wireOp",EDGE,"E56.6.7"),sQuery(id+"F0.wireOp",EDGE,"E56.6.8"),sQuery(id+"F0.wireOp",EDGE,"E56.6.9"),sQuery(id+"F0.wireOp",EDGE,"E56.6.10"),sQuery(id+"F0.wireOp",EDGE,"E56.6.11"),sQuery(id+"F0.wireOp",EDGE,"E56.6.12"),sQuery(id+"F0.wireOp",EDGE,"E56.6.13"),sQuery(id+"F0.wireOp",EDGE,"E56.6.14"),sQuery(id+"F0.wireOp",EDGE,"E56.6.15"),sQuery(id+"F0.wireOp",EDGE,"E56.6.16"),sQuery(id+"F0.wireOp",EDGE,"E56.6.17"),sQuery(id+"F0.wireOp",EDGE,"E56.6.18"),sQuery(id+"F0.wireOp",EDGE,"E56.6.19"),sQuery(id+"F0.wireOp",EDGE,"E56.6.20"),sQuery(id+"F0.wireOp",EDGE,"E56.6.21"),sQuery(id+"F0.wireOp",EDGE,"E56.6.22"),sQuery(id+"F0.wireOp",EDGE,"E56.6.23"),sQuery(id+"F0.wireOp",EDGE,"E56.6.24"),sQuery(id+"F0.wireOp",EDGE,"E56.6.25"),sQuery(id+"F0.wireOp",EDGE,"E56.6.26"),sQuery(id+"F0.wireOp",EDGE,"E56.6.27"),sQuery(id+"F0.wireOp",EDGE,"E56.6.28"),sQuery(id+"F0.wireOp",EDGE,"E56.6.29"),sQuery(id+"F0.wireOp",EDGE,"E56.7.0"),sQuery(id+"F0.wireOp",EDGE,"E56.7.1"),sQuery(id+"F0.wireOp",EDGE,"E56.7.2"),sQuery(id+"F0.wireOp",EDGE,"E56.7.3"),sQuery(id+"F0.wireOp",EDGE,"E56.7.4"),sQuery(id+"F0.wireOp",EDGE,"E56.7.5"),sQuery(id+"F0.wireOp",EDGE,"E56.7.6"),sQuery(id+"F0.wireOp",EDGE,"E56.7.7"),sQuery(id+"F0.wireOp",EDGE,"E56.7.8"),sQuery(id+"F0.wireOp",EDGE,"E56.7.9"),sQuery(id+"F0.wireOp",EDGE,"E56.7.10"),sQuery(id+"F0.wireOp",EDGE,"E56.7.11"),sQuery(id+"F0.wireOp",EDGE,"E56.7.12"),sQuery(id+"F0.wireOp",EDGE,"E56.7.13"),sQuery(id+"F0.wireOp",EDGE,"E56.7.14"),sQuery(id+"F0.wireOp",EDGE,"E56.7.15"),sQuery(id+"F0.wireOp",EDGE,"E56.7.16"),sQuery(id+"F0.wireOp",EDGE,"E56.7.17"),sQuery(id+"F0.wireOp",EDGE,"E56.7.18"),sQuery(id+"F0.wireOp",EDGE,"E56.7.19"),sQuery(id+"F0.wireOp",EDGE,"E56.7.20"),sQuery(id+"F0.wireOp",EDGE,"E56.7.21"),sQuery(id+"F0.wireOp",EDGE,"E56.7.22"),sQuery(id+"F0.wireOp",EDGE,"E56.7.23"),sQuery(id+"F0.wireOp",EDGE,"E56.7.24"),sQuery(id+"F0.wireOp",EDGE,"E56.7.25"),sQuery(id+"F0.wireOp",EDGE,"E56.7.26"),sQuery(id+"F0.wireOp",EDGE,"E56.7.27"),sQuery(id+"F0.wireOp",EDGE,"E56.7.28"),sQuery(id+"F0.wireOp",EDGE,"E56.7.29"),sQuery(id+"F0.wireOp",EDGE,"E56.8.0"),sQuery(id+"F0.wireOp",EDGE,"E56.8.1"),sQuery(id+"F0.wireOp",EDGE,"E56.8.2"),sQuery(id+"F0.wireOp",EDGE,"E56.8.3"),sQuery(id+"F0.wireOp",EDGE,"E56.8.4"),sQuery(id+"F0.wireOp",EDGE,"E56.8.5"),sQuery(id+"F0.wireOp",EDGE,"E56.8.6"),sQuery(id+"F0.wireOp",EDGE,"E56.8.7"),sQuery(id+"F0.wireOp",EDGE,"E56.8.8"),sQuery(id+"F0.wireOp",EDGE,"E56.8.9"),sQuery(id+"F0.wireOp",EDGE,"E56.8.10"),sQuery(id+"F0.wireOp",EDGE,"E56.8.11"),sQuery(id+"F0.wireOp",EDGE,"E56.8.12"),sQuery(id+"F0.wireOp",EDGE,"E56.8.13"),sQuery(id+"F0.wireOp",EDGE,"E56.8.14"),sQuery(id+"F0.wireOp",EDGE,"E56.8.15"),sQuery(id+"F0.wireOp",EDGE,"E56.8.16"),sQuery(id+"F0.wireOp",EDGE,"E56.8.17"),sQuery(id+"F0.wireOp",EDGE,"E56.8.18"),sQuery(id+"F0.wireOp",EDGE,"E56.8.19"),sQuery(id+"F0.wireOp",EDGE,"E56.8.20"),sQuery(id+"F0.wireOp",EDGE,"E56.8.21"),sQuery(id+"F0.wireOp",EDGE,"E56.8.22"),sQuery(id+"F0.wireOp",EDGE,"E56.8.23"),sQuery(id+"F0.wireOp",EDGE,"E56.8.24"),sQuery(id+"F0.wireOp",EDGE,"E56.8.25"),sQuery(id+"F0.wireOp",EDGE,"E56.8.26"),sQuery(id+"F0.wireOp",EDGE,"E56.8.27"),sQuery(id+"F0.wireOp",EDGE,"E56.8.28"),sQuery(id+"F0.wireOp",EDGE,"E56.8.29"),sQuery(id+"F0.wireOp",EDGE,"E56.9.0"),sQuery(id+"F0.wireOp",EDGE,"E56.9.1"),sQuery(id+"F0.wireOp",EDGE,"E56.9.2"),sQuery(id+"F0.wireOp",EDGE,"E56.9.3"),sQuery(id+"F0.wireOp",EDGE,"E56.9.4"),sQuery(id+"F0.wireOp",EDGE,"E56.9.5"),sQuery(id+"F0.wireOp",EDGE,"E56.9.6"),sQuery(id+"F0.wireOp",EDGE,"E56.9.7"),sQuery(id+"F0.wireOp",EDGE,"E56.9.8"),sQuery(id+"F0.wireOp",EDGE,"E56.9.9"),sQuery(id+"F0.wireOp",EDGE,"E56.9.10"),sQuery(id+"F0.wireOp",EDGE,"E56.9.11"),sQuery(id+"F0.wireOp",EDGE,"E56.9.12"),sQuery(id+"F0.wireOp",EDGE,"E56.9.13"),sQuery(id+"F0.wireOp",EDGE,"E56.9.14"),sQuery(id+"F0.wireOp",EDGE,"E56.9.15"),sQuery(id+"F0.wireOp",EDGE,"E56.9.16"),sQuery(id+"F0.wireOp",EDGE,"E56.9.17"),sQuery(id+"F0.wireOp",EDGE,"E56.9.18"),sQuery(id+"F0.wireOp",EDGE,"E56.9.19"),sQuery(id+"F0.wireOp",EDGE,"E56.9.20"),sQuery(id+"F0.wireOp",EDGE,"E56.9.21"),sQuery(id+"F0.wireOp",EDGE,"E56.9.22"),sQuery(id+"F0.wireOp",EDGE,"E56.9.23"),sQuery(id+"F0.wireOp",EDGE,"E56.9.24"),sQuery(id+"F0.wireOp",EDGE,"E56.9.25"),sQuery(id+"F0.wireOp",EDGE,"E56.9.26"),sQuery(id+"F0.wireOp",EDGE,"E56.9.27"),sQuery(id+"F0.wireOp",EDGE,"E56.9.28"),sQuery(id+"F0.wireOp",EDGE,"E56.9.29"),sQuery(id+"F0.wireOp",EDGE,"E56.10.0"),sQuery(id+"F0.wireOp",EDGE,"E56.10.1"),sQuery(id+"F0.wireOp",EDGE,"E56.10.2"),sQuery(id+"F0.wireOp",EDGE,"E56.10.3"),sQuery(id+"F0.wireOp",EDGE,"E56.10.4"),sQuery(id+"F0.wireOp",EDGE,"E56.10.5"),sQuery(id+"F0.wireOp",EDGE,"E56.10.6"),sQuery(id+"F0.wireOp",EDGE,"E56.10.7"),sQuery(id+"F0.wireOp",EDGE,"E56.10.8"),sQuery(id+"F0.wireOp",EDGE,"E56.10.9"),sQuery(id+"F0.wireOp",EDGE,"E56.10.10"),sQuery(id+"F0.wireOp",EDGE,"E56.10.11"),sQuery(id+"F0.wireOp",EDGE,"E56.10.12"),sQuery(id+"F0.wireOp",EDGE,"E56.10.13"),sQuery(id+"F0.wireOp",EDGE,"E56.10.14"),sQuery(id+"F0.wireOp",EDGE,"E56.10.15"),sQuery(id+"F0.wireOp",EDGE,"E56.10.16"),sQuery(id+"F0.wireOp",EDGE,"E56.10.17"),sQuery(id+"F0.wireOp",EDGE,"E56.10.18"),sQuery(id+"F0.wireOp",EDGE,"E56.10.19"),sQuery(id+"F0.wireOp",EDGE,"E56.10.20"),sQuery(id+"F0.wireOp",EDGE,"E56.10.21"),sQuery(id+"F0.wireOp",EDGE,"E56.10.22"),sQuery(id+"F0.wireOp",EDGE,"E56.10.23"),sQuery(id+"F0.wireOp",EDGE,"E56.10.24"),sQuery(id+"F0.wireOp",EDGE,"E56.10.25"),sQuery(id+"F0.wireOp",EDGE,"E56.10.26"),sQuery(id+"F0.wireOp",EDGE,"E56.10.27"),sQuery(id+"F0.wireOp",EDGE,"E56.10.28"),sQuery(id+"F0.wireOp",EDGE,"E56.10.29"),sQuery(id+"F0.wireOp",EDGE,"E56.11.0"),sQuery(id+"F0.wireOp",EDGE,"E56.11.1"),sQuery(id+"F0.wireOp",EDGE,"E56.11.2"),sQuery(id+"F0.wireOp",EDGE,"E56.11.3"),sQuery(id+"F0.wireOp",EDGE,"E56.11.4"),sQuery(id+"F0.wireOp",EDGE,"E56.11.5"),sQuery(id+"F0.wireOp",EDGE,"E56.11.6"),sQuery(id+"F0.wireOp",EDGE,"E56.11.7"),sQuery(id+"F0.wireOp",EDGE,"E56.11.8"),sQuery(id+"F0.wireOp",EDGE,"E56.11.9"),sQuery(id+"F0.wireOp",EDGE,"E56.11.10"),sQuery(id+"F0.wireOp",EDGE,"E56.11.11"),sQuery(id+"F0.wireOp",EDGE,"E56.11.12"),sQuery(id+"F0.wireOp",EDGE,"E56.11.13"),sQuery(id+"F0.wireOp",EDGE,"E56.11.14"),sQuery(id+"F0.wireOp",EDGE,"E56.11.15"),sQuery(id+"F0.wireOp",EDGE,"E56.11.16"),sQuery(id+"F0.wireOp",EDGE,"E56.11.17"),sQuery(id+"F0.wireOp",EDGE,"E56.11.18"),sQuery(id+"F0.wireOp",EDGE,"E56.11.19"),sQuery(id+"F0.wireOp",EDGE,"E56.11.20"),sQuery(id+"F0.wireOp",EDGE,"E56.11.21"),sQuery(id+"F0.wireOp",EDGE,"E56.11.22"),sQuery(id+"F0.wireOp",EDGE,"E56.11.23"),sQuery(id+"F0.wireOp",EDGE,"E56.11.24"),sQuery(id+"F0.wireOp",EDGE,"E56.11.25"),sQuery(id+"F0.wireOp",EDGE,"E56.11.26"),sQuery(id+"F0.wireOp",EDGE,"E56.11.27"),sQuery(id+"F0.wireOp",EDGE,"E56.11.28"),sQuery(id+"F0.wireOp",EDGE,"E56.11.29"),sQuery(id+"F0.wireOp",EDGE,"E56.12.0"),sQuery(id+"F0.wireOp",EDGE,"E56.12.1"),sQuery(id+"F0.wireOp",EDGE,"E56.12.2"),sQuery(id+"F0.wireOp",EDGE,"E56.12.3"),sQuery(id+"F0.wireOp",EDGE,"E56.12.4"),sQuery(id+"F0.wireOp",EDGE,"E56.12.5"),sQuery(id+"F0.wireOp",EDGE,"E56.12.6"),sQuery(id+"F0.wireOp",EDGE,"E56.12.7"),sQuery(id+"F0.wireOp",EDGE,"E56.12.8"),sQuery(id+"F0.wireOp",EDGE,"E56.12.9"),sQuery(id+"F0.wireOp",EDGE,"E56.12.10"),sQuery(id+"F0.wireOp",EDGE,"E56.12.11"),sQuery(id+"F0.wireOp",EDGE,"E56.12.12"),sQuery(id+"F0.wireOp",EDGE,"E56.12.13"),sQuery(id+"F0.wireOp",EDGE,"E56.12.14"),sQuery(id+"F0.wireOp",EDGE,"E56.12.15"),sQuery(id+"F0.wireOp",EDGE,"E56.12.16"),sQuery(id+"F0.wireOp",EDGE,"E56.12.17"),sQuery(id+"F0.wireOp",EDGE,"E56.12.18"),sQuery(id+"F0.wireOp",EDGE,"E56.12.19"),sQuery(id+"F0.wireOp",EDGE,"E56.12.20"),sQuery(id+"F0.wireOp",EDGE,"E56.12.21"),sQuery(id+"F0.wireOp",EDGE,"E56.12.22"),sQuery(id+"F0.wireOp",EDGE,"E56.12.23"),sQuery(id+"F0.wireOp",EDGE,"E56.12.24"),sQuery(id+"F0.wireOp",EDGE,"E56.12.25"),sQuery(id+"F0.wireOp",EDGE,"E56.12.26"),sQuery(id+"F0.wireOp",EDGE,"E56.12.27"),sQuery(id+"F0.wireOp",EDGE,"E56.12.28"),sQuery(id+"F0.wireOp",EDGE,"E56.12.29"),sQuery(id+"F0.wireOp",EDGE,"E56.13.0"),sQuery(id+"F0.wireOp",EDGE,"E56.13.1"),sQuery(id+"F0.wireOp",EDGE,"E56.13.2"),sQuery(id+"F0.wireOp",EDGE,"E56.13.3"),sQuery(id+"F0.wireOp",EDGE,"E56.13.4"),sQuery(id+"F0.wireOp",EDGE,"E56.13.5"),sQuery(id+"F0.wireOp",EDGE,"E56.13.6"),sQuery(id+"F0.wireOp",EDGE,"E56.13.7"),sQuery(id+"F0.wireOp",EDGE,"E56.13.8"),sQuery(id+"F0.wireOp",EDGE,"E56.13.9"),sQuery(id+"F0.wireOp",EDGE,"E56.13.10"),sQuery(id+"F0.wireOp",EDGE,"E56.13.11"),sQuery(id+"F0.wireOp",EDGE,"E56.13.12"),sQuery(id+"F0.wireOp",EDGE,"E56.13.13"),sQuery(id+"F0.wireOp",EDGE,"E56.13.14"),sQuery(id+"F0.wireOp",EDGE,"E56.13.15"),sQuery(id+"F0.wireOp",EDGE,"E56.13.16"),sQuery(id+"F0.wireOp",EDGE,"E56.13.17"),sQuery(id+"F0.wireOp",EDGE,"E56.13.18"),sQuery(id+"F0.wireOp",EDGE,"E56.13.19"),sQuery(id+"F0.wireOp",EDGE,"E56.13.20"),sQuery(id+"F0.wireOp",EDGE,"E56.13.21"),sQuery(id+"F0.wireOp",EDGE,"E56.13.22"),sQuery(id+"F0.wireOp",EDGE,"E56.13.23"),sQuery(id+"F0.wireOp",EDGE,"E56.13.24"),sQuery(id+"F0.wireOp",EDGE,"E56.13.25"),sQuery(id+"F0.wireOp",EDGE,"E56.13.26"),sQuery(id+"F0.wireOp",EDGE,"E56.13.27"),sQuery(id+"F0.wireOp",EDGE,"E56.13.28"),sQuery(id+"F0.wireOp",EDGE,"E56.13.29"),sQuery(id+"F0.wireOp",EDGE,"E56.14.0"),sQuery(id+"F0.wireOp",EDGE,"E56.14.1"),sQuery(id+"F0.wireOp",EDGE,"E56.14.2"),sQuery(id+"F0.wireOp",EDGE,"E56.14.3"),sQuery(id+"F0.wireOp",EDGE,"E56.14.4"),sQuery(id+"F0.wireOp",EDGE,"E56.14.5"),sQuery(id+"F0.wireOp",EDGE,"E56.14.6"),sQuery(id+"F0.wireOp",EDGE,"E56.14.7"),sQuery(id+"F0.wireOp",EDGE,"E56.14.8"),sQuery(id+"F0.wireOp",EDGE,"E56.14.9"),sQuery(id+"F0.wireOp",EDGE,"E56.14.10"),sQuery(id+"F0.wireOp",EDGE,"E56.14.11"),sQuery(id+"F0.wireOp",EDGE,"E56.14.12"),sQuery(id+"F0.wireOp",EDGE,"E56.14.13"),sQuery(id+"F0.wireOp",EDGE,"E56.14.14"),sQuery(id+"F0.wireOp",EDGE,"E56.14.15"),sQuery(id+"F0.wireOp",EDGE,"E56.14.16"),sQuery(id+"F0.wireOp",EDGE,"E56.14.17"),sQuery(id+"F0.wireOp",EDGE,"E56.14.18"),sQuery(id+"F0.wireOp",EDGE,"E56.14.19"),sQuery(id+"F0.wireOp",EDGE,"E56.14.20"),sQuery(id+"F0.wireOp",EDGE,"E56.14.21"),sQuery(id+"F0.wireOp",EDGE,"E56.14.22"),sQuery(id+"F0.wireOp",EDGE,"E56.14.23"),sQuery(id+"F0.wireOp",EDGE,"E56.14.24"),sQuery(id+"F0.wireOp",EDGE,"E56.14.25"),sQuery(id+"F0.wireOp",EDGE,"E56.14.26"),sQuery(id+"F0.wireOp",EDGE,"E56.14.27"),sQuery(id+"F0.wireOp",EDGE,"E56.14.28"),sQuery(id+"F0.wireOp",EDGE,"E56.14.29"),sQuery(id+"F0.wireOp",EDGE,"E56.15.0"),sQuery(id+"F0.wireOp",EDGE,"E56.15.1"),sQuery(id+"F0.wireOp",EDGE,"E56.15.2"),sQuery(id+"F0.wireOp",EDGE,"E56.15.3"),sQuery(id+"F0.wireOp",EDGE,"E56.15.4"),sQuery(id+"F0.wireOp",EDGE,"E56.15.5"),sQuery(id+"F0.wireOp",EDGE,"E56.15.6"),sQuery(id+"F0.wireOp",EDGE,"E56.15.7"),sQuery(id+"F0.wireOp",EDGE,"E56.15.8"),sQuery(id+"F0.wireOp",EDGE,"E56.15.9"),sQuery(id+"F0.wireOp",EDGE,"E56.15.10"),sQuery(id+"F0.wireOp",EDGE,"E56.15.11"),sQuery(id+"F0.wireOp",EDGE,"E56.15.12"),sQuery(id+"F0.wireOp",EDGE,"E56.15.13"),sQuery(id+"F0.wireOp",EDGE,"E56.15.14"),sQuery(id+"F0.wireOp",EDGE,"E56.15.15"),sQuery(id+"F0.wireOp",EDGE,"E56.15.16"),sQuery(id+"F0.wireOp",EDGE,"E56.15.17"),sQuery(id+"F0.wireOp",EDGE,"E56.15.18"),sQuery(id+"F0.wireOp",EDGE,"E56.15.19"),sQuery(id+"F0.wireOp",EDGE,"E56.15.20"),sQuery(id+"F0.wireOp",EDGE,"E56.15.21"),sQuery(id+"F0.wireOp",EDGE,"E56.15.22"),sQuery(id+"F0.wireOp",EDGE,"E56.15.23"),sQuery(id+"F0.wireOp",EDGE,"E56.15.24"),sQuery(id+"F0.wireOp",EDGE,"E56.15.25"),sQuery(id+"F0.wireOp",EDGE,"E56.15.26"),sQuery(id+"F0.wireOp",EDGE,"E56.15.27"),sQuery(id+"F0.wireOp",EDGE,"E56.15.28"),sQuery(id+"F0.wireOp",EDGE,"E56.15.29"),sQuery(id+"F0.wireOp",EDGE,"E56.16.0"),sQuery(id+"F0.wireOp",EDGE,"E56.16.1"),sQuery(id+"F0.wireOp",EDGE,"E56.16.2"),sQuery(id+"F0.wireOp",EDGE,"E56.16.3"),sQuery(id+"F0.wireOp",EDGE,"E56.16.4"),sQuery(id+"F0.wireOp",EDGE,"E56.16.5"),sQuery(id+"F0.wireOp",EDGE,"E56.16.6"),sQuery(id+"F0.wireOp",EDGE,"E56.16.7"),sQuery(id+"F0.wireOp",EDGE,"E56.16.8"),sQuery(id+"F0.wireOp",EDGE,"E56.16.9"),sQuery(id+"F0.wireOp",EDGE,"E56.16.10"),sQuery(id+"F0.wireOp",EDGE,"E56.16.11"),sQuery(id+"F0.wireOp",EDGE,"E56.16.12"),sQuery(id+"F0.wireOp",EDGE,"E56.16.13"),sQuery(id+"F0.wireOp",EDGE,"E56.16.14"),sQuery(id+"F0.wireOp",EDGE,"E56.16.15"),sQuery(id+"F0.wireOp",EDGE,"E56.16.16"),sQuery(id+"F0.wireOp",EDGE,"E56.16.17"),sQuery(id+"F0.wireOp",EDGE,"E56.16.18"),sQuery(id+"F0.wireOp",EDGE,"E56.16.19"),sQuery(id+"F0.wireOp",EDGE,"E56.16.20"),sQuery(id+"F0.wireOp",EDGE,"E56.16.21"),sQuery(id+"F0.wireOp",EDGE,"E56.16.22"),sQuery(id+"F0.wireOp",EDGE,"E56.16.23"),sQuery(id+"F0.wireOp",EDGE,"E56.16.24"),sQuery(id+"F0.wireOp",EDGE,"E56.16.25"),sQuery(id+"F0.wireOp",EDGE,"E56.16.26"),sQuery(id+"F0.wireOp",EDGE,"E56.16.27"),sQuery(id+"F0.wireOp",EDGE,"E56.16.28"),sQuery(id+"F0.wireOp",EDGE,"E56.16.29"),sQuery(id+"F0.wireOp",EDGE,"E56.17.0"),sQuery(id+"F0.wireOp",EDGE,"E56.17.1"),sQuery(id+"F0.wireOp",EDGE,"E56.17.2"),sQuery(id+"F0.wireOp",EDGE,"E56.17.3"),sQuery(id+"F0.wireOp",EDGE,"E56.17.4"),sQuery(id+"F0.wireOp",EDGE,"E56.17.5"),sQuery(id+"F0.wireOp",EDGE,"E56.17.6"),sQuery(id+"F0.wireOp",EDGE,"E56.17.7"),sQuery(id+"F0.wireOp",EDGE,"E56.17.8"),sQuery(id+"F0.wireOp",EDGE,"E56.17.9"),sQuery(id+"F0.wireOp",EDGE,"E56.17.10"),sQuery(id+"F0.wireOp",EDGE,"E56.17.11"),sQuery(id+"F0.wireOp",EDGE,"E56.17.12"),sQuery(id+"F0.wireOp",EDGE,"E56.17.13"),sQuery(id+"F0.wireOp",EDGE,"E56.17.14"),sQuery(id+"F0.wireOp",EDGE,"E56.17.15"),sQuery(id+"F0.wireOp",EDGE,"E56.17.16"),sQuery(id+"F0.wireOp",EDGE,"E56.17.17"),sQuery(id+"F0.wireOp",EDGE,"E56.17.18"),sQuery(id+"F0.wireOp",EDGE,"E56.17.19"),sQuery(id+"F0.wireOp",EDGE,"E56.17.20"),sQuery(id+"F0.wireOp",EDGE,"E56.17.21"),sQuery(id+"F0.wireOp",EDGE,"E56.17.22"),sQuery(id+"F0.wireOp",EDGE,"E56.17.23"),sQuery(id+"F0.wireOp",EDGE,"E56.17.24"),sQuery(id+"F0.wireOp",EDGE,"E56.17.25"),sQuery(id+"F0.wireOp",EDGE,"E56.17.26"),sQuery(id+"F0.wireOp",EDGE,"E56.17.27"),sQuery(id+"F0.wireOp",EDGE,"E56.17.28"),sQuery(id+"F0.wireOp",EDGE,"E56.17.29"),sQuery(id+"F0.wireOp",EDGE,"E56.18.0"),sQuery(id+"F0.wireOp",EDGE,"E56.18.1"),sQuery(id+"F0.wireOp",EDGE,"E56.18.2"),sQuery(id+"F0.wireOp",EDGE,"E56.18.3"),sQuery(id+"F0.wireOp",EDGE,"E56.18.4"),sQuery(id+"F0.wireOp",EDGE,"E56.18.5"),sQuery(id+"F0.wireOp",EDGE,"E56.18.6"),sQuery(id+"F0.wireOp",EDGE,"E56.18.7"),sQuery(id+"F0.wireOp",EDGE,"E56.18.8"),sQuery(id+"F0.wireOp",EDGE,"E56.18.9"),sQuery(id+"F0.wireOp",EDGE,"E56.18.10"),sQuery(id+"F0.wireOp",EDGE,"E56.18.11"),sQuery(id+"F0.wireOp",EDGE,"E56.18.12"),sQuery(id+"F0.wireOp",EDGE,"E56.18.13"),sQuery(id+"F0.wireOp",EDGE,"E56.18.14"),sQuery(id+"F0.wireOp",EDGE,"E56.18.15"),sQuery(id+"F0.wireOp",EDGE,"E56.18.16"),sQuery(id+"F0.wireOp",EDGE,"E56.18.17"),sQuery(id+"F0.wireOp",EDGE,"E56.18.18"),sQuery(id+"F0.wireOp",EDGE,"E56.18.19"),sQuery(id+"F0.wireOp",EDGE,"E56.18.20"),sQuery(id+"F0.wireOp",EDGE,"E56.18.21"),sQuery(id+"F0.wireOp",EDGE,"E56.18.22"),sQuery(id+"F0.wireOp",EDGE,"E56.18.23"),sQuery(id+"F0.wireOp",EDGE,"E56.18.24"),sQuery(id+"F0.wireOp",EDGE,"E56.18.25"),sQuery(id+"F0.wireOp",EDGE,"E56.18.26"),sQuery(id+"F0.wireOp",EDGE,"E56.18.27"),sQuery(id+"F0.wireOp",EDGE,"E56.18.28"),sQuery(id+"F0.wireOp",EDGE,"E56.18.29"),sQuery(id+"F0.wireOp",EDGE,"E56.19.0"),sQuery(id+"F0.wireOp",EDGE,"E56.19.1"),sQuery(id+"F0.wireOp",EDGE,"E56.19.2"),sQuery(id+"F0.wireOp",EDGE,"E56.19.3"),sQuery(id+"F0.wireOp",EDGE,"E56.19.4"),sQuery(id+"F0.wireOp",EDGE,"E56.19.5"),sQuery(id+"F0.wireOp",EDGE,"E56.19.6"),sQuery(id+"F0.wireOp",EDGE,"E56.19.7"),sQuery(id+"F0.wireOp",EDGE,"E56.19.8"),sQuery(id+"F0.wireOp",EDGE,"E56.19.9"),sQuery(id+"F0.wireOp",EDGE,"E56.19.10"),sQuery(id+"F0.wireOp",EDGE,"E56.19.11"),sQuery(id+"F0.wireOp",EDGE,"E56.19.12"),sQuery(id+"F0.wireOp",EDGE,"E56.19.13"),sQuery(id+"F0.wireOp",EDGE,"E56.19.14"),sQuery(id+"F0.wireOp",EDGE,"E56.19.15"),sQuery(id+"F0.wireOp",EDGE,"E56.19.16"),sQuery(id+"F0.wireOp",EDGE,"E56.19.17"),sQuery(id+"F0.wireOp",EDGE,"E56.19.18"),sQuery(id+"F0.wireOp",EDGE,"E56.19.19"),sQuery(id+"F0.wireOp",EDGE,"E56.19.20"),sQuery(id+"F0.wireOp",EDGE,"E56.19.21"),sQuery(id+"F0.wireOp",EDGE,"E56.19.22"),sQuery(id+"F0.wireOp",EDGE,"E56.19.23"),sQuery(id+"F0.wireOp",EDGE,"E56.19.24"),sQuery(id+"F0.wireOp",EDGE,"E56.19.25"),sQuery(id+"F0.wireOp",EDGE,"E56.19.26"),sQuery(id+"F0.wireOp",EDGE,"E56.19.27"),sQuery(id+"F0.wireOp",EDGE,"E56.19.28"),sQuery(id+"F0.wireOp",EDGE,"E56.19.29")])],"isStart":true});
            var sketch = newSketch(context, id + "F6", { "sketchPlane" : qUnion([Q0])});
            skLineSegment(sketch, "E57.bottom", {"start": v(50.72, -32.43) * mm, "end": v(-50.72, -32.43) * mm});
            skLineSegment(sketch, "E57.top", {"start": v(50.72, 32.43) * mm, "end": v(-50.72, 32.43) * mm});
            skLineSegment(sketch, "E57.left", {"start": v(50.72, -32.43) * mm, "end": v(50.72, 32.43) * mm});
            skLineSegment(sketch, "E57.right", {"start": v(-50.72, -32.43) * mm, "end": v(-50.72, 32.43) * mm});
            skPoint(sketch, "E57.middle", {"position": v(0, 0) * mm});
            skSolve(sketch);
        }
        {
            var Q0;
            Q0 = qSketchRegion(id + "F6", true);
            extrude(context, id + "F7", {"entities" : qUnion([Q0]), "depth" : 2.54 * mm, "offsetDistance" : 25.4 * mm});
        }
        {
            var Q0;
            Q0=makeQuery(id+"F2.opExtrude","CAP_FACE",FACE,{"disambiguationData":[OSD([sQuery(id+"F0.wireOp",EDGE,"E1")])],"isStart":false});
            var sketch = newSketch(context, id + "F8", { "sketchPlane" : qUnion([Q0])});
            skPoint(sketch, "E58.0", {"position": v(-22.54, 0) * mm});
            skCircle(sketch, "E59", {"center": v(-22.54, 0) * mm, "radius": 3.32 * mm});
            skSolve(sketch);
        }
        {
            var Q0;
            Q0=makeQuery(id+"F8.imprint","IMPRINT",FACE,{"disambiguationData":[TD([[makeQuery(id+"F8.imprint","IMPRINT",EDGE,{"derivedFrom":sQuery(id+"F8.wireOp",EDGE,"E59")}),1.0]])]});
            extrude(context, id + "F9", {"entities" : qUnion([Q0]), "operationType" : NewBodyOperationType.REMOVE, "oppositeDirection" : true, "depth" : 25.4 * mm, "offsetDistance" : 25.4 * mm});
        }
        {
            var Q0;
            Q0=makeQuery(id+"F7.opExtrude","CAP_FACE",FACE,{"disambiguationData":[OSD([sQuery(id+"F6.wireOp",EDGE,"E57.bottom"),sQuery(id+"F6.wireOp",EDGE,"E57.top"),sQuery(id+"F6.wireOp",EDGE,"E57.left"),sQuery(id+"F6.wireOp",EDGE,"E57.right")])],"isStart":true});
            var sketch = newSketch(context, id + "F10", { "sketchPlane" : qUnion([Q0])});
            skPoint(sketch, "E60.0", {"position": v(-22.54, 0) * mm});
            skCircle(sketch, "E61", {"center": v(-22.54, 0) * mm, "radius": 2.87 * mm});
            skSolve(sketch);
        }
        {
            var Q0;
            Q0=makeQuery(id+"F10.imprint","IMPRINT",FACE,{"disambiguationData":[TD([[makeQuery(id+"F10.imprint","IMPRINT",EDGE,{"derivedFrom":sQuery(id+"F10.wireOp",EDGE,"E61")}),1.0]])]});
            var Q1;
            Q1=sQuery(id+"F10.wireOp",EDGE,"E61");
            extrude(context, id + "F11", {"entities" : qUnion([Q0]), "operationType" : NewBodyOperationType.ADD, "surfaceEntities" : qUnion([Q1]), "depth" : 20.32 * mm, "offsetDistance" : 25.4 * mm});
        }
        {
            var Q0;
            Q0=makeQuery(id+"F11.opExtrude","CAP_FACE",FACE,{"disambiguationData":[OSD([sQuery(id+"F10.wireOp",EDGE,"E61")])],"isStart":false});
            var sketch = newSketch(context, id + "F12", { "sketchPlane" : qUnion([Q0])});
            skCircle(sketch, "E62.0", {"center": v(-22.54, 0) * mm, "radius": 2.87 * mm});
            skCircle(sketch, "E63.0", {"center": v(-22.54, 0) * mm, "radius": 4.4 * mm});
            skSolve(sketch);
        }
        {
            var Q0;
            Q0=makeQuery(id+"F12.imprint","IMPRINT",FACE,{"disambiguationData":[TD([[makeQuery(id+"F12.imprint","IMPRINT",EDGE,{"derivedFrom":sQuery(id+"F12.wireOp",EDGE,"E62.0")}),-1.0]])]});
            var Q1;
            Q1=sQuery(id+"F12.wireOp",EDGE,"E63.0");
            var Q2;
            Q2=sQuery(id+"F12.wireOp",EDGE,"E62.0");
            extrude(context, id + "F13", {"entities" : qUnion([Q0]), "surfaceEntities" : qUnion([Q1, Q2]), "oppositeDirection" : true, "depth" : 2.3 * mm, "offsetDistance" : 25.4 * mm});
        }
        {
            var Q0;
            Q0=makeQuery(id+"F1.opExtrude","SWEPT_BODY",BODY,{"disambiguationData":[OSD([sQuery(id+"F0.wireOp",EDGE,"E5"),sQuery(id+"F0.wireOp",EDGE,"E26"),sQuery(id+"F0.wireOp",EDGE,"E27.MirrorCS"),sQuery(id+"F0.wireOp",EDGE,"E28"),sQuery(id+"F0.wireOp",EDGE,"E29"),sQuery(id+"F0.wireOp",EDGE,"E30"),sQuery(id+"F0.wireOp",EDGE,"E31"),sQuery(id+"F0.wireOp",EDGE,"E32"),sQuery(id+"F0.wireOp",EDGE,"E33"),sQuery(id+"F0.wireOp",EDGE,"E34"),sQuery(id+"F0.wireOp",EDGE,"E35"),sQuery(id+"F0.wireOp",EDGE,"E36"),sQuery(id+"F0.wireOp",EDGE,"E37"),sQuery(id+"F0.wireOp",EDGE,"E38"),sQuery(id+"F0.wireOp",EDGE,"E39"),sQuery(id+"F0.wireOp",EDGE,"E40"),sQuery(id+"F0.wireOp",EDGE,"E41"),sQuery(id+"F0.wireOp",EDGE,"E42.MirrorCS"),sQuery(id+"F0.wireOp",EDGE,"E43.MirrorCS"),sQuery(id+"F0.wireOp",EDGE,"E44.MirrorCS"),sQuery(id+"F0.wireOp",EDGE,"E45.MirrorCS"),sQuery(id+"F0.wireOp",EDGE,"E46.MirrorCS"),sQuery(id+"F0.wireOp",EDGE,"E47.MirrorCS"),sQuery(id+"F0.wireOp",EDGE,"E48.MirrorCS"),sQuery(id+"F0.wireOp",EDGE,"E49.MirrorCS"),sQuery(id+"F0.wireOp",EDGE,"E50.MirrorCS"),sQuery(id+"F0.wireOp",EDGE,"E51.MirrorCS"),sQuery(id+"F0.wireOp",EDGE,"E52.MirrorCS"),sQuery(id+"F0.wireOp",EDGE,"E53.MirrorCS"),sQuery(id+"F0.wireOp",EDGE,"E54.MirrorCS"),sQuery(id+"F0.wireOp",EDGE,"E55.MirrorCS"),sQuery(id+"F0.wireOp",EDGE,"E56.1.0"),sQuery(id+"F0.wireOp",EDGE,"E56.1.1"),sQuery(id+"F0.wireOp",EDGE,"E56.1.2"),sQuery(id+"F0.wireOp",EDGE,"E56.1.3"),sQuery(id+"F0.wireOp",EDGE,"E56.1.4"),sQuery(id+"F0.wireOp",EDGE,"E56.1.5"),sQuery(id+"F0.wireOp",EDGE,"E56.1.6"),sQuery(id+"F0.wireOp",EDGE,"E56.1.7"),sQuery(id+"F0.wireOp",EDGE,"E56.1.8"),sQuery(id+"F0.wireOp",EDGE,"E56.1.9"),sQuery(id+"F0.wireOp",EDGE,"E56.1.10"),sQuery(id+"F0.wireOp",EDGE,"E56.1.11"),sQuery(id+"F0.wireOp",EDGE,"E56.1.12"),sQuery(id+"F0.wireOp",EDGE,"E56.1.13"),sQuery(id+"F0.wireOp",EDGE,"E56.1.14"),sQuery(id+"F0.wireOp",EDGE,"E56.1.15"),sQuery(id+"F0.wireOp",EDGE,"E56.1.16"),sQuery(id+"F0.wireOp",EDGE,"E56.1.17"),sQuery(id+"F0.wireOp",EDGE,"E56.1.18"),sQuery(id+"F0.wireOp",EDGE,"E56.1.19"),sQuery(id+"F0.wireOp",EDGE,"E56.1.20"),sQuery(id+"F0.wireOp",EDGE,"E56.1.21"),sQuery(id+"F0.wireOp",EDGE,"E56.1.22"),sQuery(id+"F0.wireOp",EDGE,"E56.1.23"),sQuery(id+"F0.wireOp",EDGE,"E56.1.24"),sQuery(id+"F0.wireOp",EDGE,"E56.1.25"),sQuery(id+"F0.wireOp",EDGE,"E56.1.26"),sQuery(id+"F0.wireOp",EDGE,"E56.1.27"),sQuery(id+"F0.wireOp",EDGE,"E56.1.28"),sQuery(id+"F0.wireOp",EDGE,"E56.1.29"),sQuery(id+"F0.wireOp",EDGE,"E56.2.0"),sQuery(id+"F0.wireOp",EDGE,"E56.2.1"),sQuery(id+"F0.wireOp",EDGE,"E56.2.2"),sQuery(id+"F0.wireOp",EDGE,"E56.2.3"),sQuery(id+"F0.wireOp",EDGE,"E56.2.4"),sQuery(id+"F0.wireOp",EDGE,"E56.2.5"),sQuery(id+"F0.wireOp",EDGE,"E56.2.6"),sQuery(id+"F0.wireOp",EDGE,"E56.2.7"),sQuery(id+"F0.wireOp",EDGE,"E56.2.8"),sQuery(id+"F0.wireOp",EDGE,"E56.2.9"),sQuery(id+"F0.wireOp",EDGE,"E56.2.10"),sQuery(id+"F0.wireOp",EDGE,"E56.2.11"),sQuery(id+"F0.wireOp",EDGE,"E56.2.12"),sQuery(id+"F0.wireOp",EDGE,"E56.2.13"),sQuery(id+"F0.wireOp",EDGE,"E56.2.14"),sQuery(id+"F0.wireOp",EDGE,"E56.2.15"),sQuery(id+"F0.wireOp",EDGE,"E56.2.16"),sQuery(id+"F0.wireOp",EDGE,"E56.2.17"),sQuery(id+"F0.wireOp",EDGE,"E56.2.18"),sQuery(id+"F0.wireOp",EDGE,"E56.2.19"),sQuery(id+"F0.wireOp",EDGE,"E56.2.20"),sQuery(id+"F0.wireOp",EDGE,"E56.2.21"),sQuery(id+"F0.wireOp",EDGE,"E56.2.22"),sQuery(id+"F0.wireOp",EDGE,"E56.2.23"),sQuery(id+"F0.wireOp",EDGE,"E56.2.24"),sQuery(id+"F0.wireOp",EDGE,"E56.2.25"),sQuery(id+"F0.wireOp",EDGE,"E56.2.26"),sQuery(id+"F0.wireOp",EDGE,"E56.2.27"),sQuery(id+"F0.wireOp",EDGE,"E56.2.28"),sQuery(id+"F0.wireOp",EDGE,"E56.2.29"),sQuery(id+"F0.wireOp",EDGE,"E56.3.0"),sQuery(id+"F0.wireOp",EDGE,"E56.3.1"),sQuery(id+"F0.wireOp",EDGE,"E56.3.2"),sQuery(id+"F0.wireOp",EDGE,"E56.3.3"),sQuery(id+"F0.wireOp",EDGE,"E56.3.4"),sQuery(id+"F0.wireOp",EDGE,"E56.3.5"),sQuery(id+"F0.wireOp",EDGE,"E56.3.6"),sQuery(id+"F0.wireOp",EDGE,"E56.3.7"),sQuery(id+"F0.wireOp",EDGE,"E56.3.8"),sQuery(id+"F0.wireOp",EDGE,"E56.3.9"),sQuery(id+"F0.wireOp",EDGE,"E56.3.10"),sQuery(id+"F0.wireOp",EDGE,"E56.3.11"),sQuery(id+"F0.wireOp",EDGE,"E56.3.12"),sQuery(id+"F0.wireOp",EDGE,"E56.3.13"),sQuery(id+"F0.wireOp",EDGE,"E56.3.14"),sQuery(id+"F0.wireOp",EDGE,"E56.3.15"),sQuery(id+"F0.wireOp",EDGE,"E56.3.16"),sQuery(id+"F0.wireOp",EDGE,"E56.3.17"),sQuery(id+"F0.wireOp",EDGE,"E56.3.18"),sQuery(id+"F0.wireOp",EDGE,"E56.3.19"),sQuery(id+"F0.wireOp",EDGE,"E56.3.20"),sQuery(id+"F0.wireOp",EDGE,"E56.3.21"),sQuery(id+"F0.wireOp",EDGE,"E56.3.22"),sQuery(id+"F0.wireOp",EDGE,"E56.3.23"),sQuery(id+"F0.wireOp",EDGE,"E56.3.24"),sQuery(id+"F0.wireOp",EDGE,"E56.3.25"),sQuery(id+"F0.wireOp",EDGE,"E56.3.26"),sQuery(id+"F0.wireOp",EDGE,"E56.3.27"),sQuery(id+"F0.wireOp",EDGE,"E56.3.28"),sQuery(id+"F0.wireOp",EDGE,"E56.3.29"),sQuery(id+"F0.wireOp",EDGE,"E56.4.0"),sQuery(id+"F0.wireOp",EDGE,"E56.4.1"),sQuery(id+"F0.wireOp",EDGE,"E56.4.2"),sQuery(id+"F0.wireOp",EDGE,"E56.4.3"),sQuery(id+"F0.wireOp",EDGE,"E56.4.4"),sQuery(id+"F0.wireOp",EDGE,"E56.4.5"),sQuery(id+"F0.wireOp",EDGE,"E56.4.6"),sQuery(id+"F0.wireOp",EDGE,"E56.4.7"),sQuery(id+"F0.wireOp",EDGE,"E56.4.8"),sQuery(id+"F0.wireOp",EDGE,"E56.4.9"),sQuery(id+"F0.wireOp",EDGE,"E56.4.10"),sQuery(id+"F0.wireOp",EDGE,"E56.4.11"),sQuery(id+"F0.wireOp",EDGE,"E56.4.12"),sQuery(id+"F0.wireOp",EDGE,"E56.4.13"),sQuery(id+"F0.wireOp",EDGE,"E56.4.14"),sQuery(id+"F0.wireOp",EDGE,"E56.4.15"),sQuery(id+"F0.wireOp",EDGE,"E56.4.16"),sQuery(id+"F0.wireOp",EDGE,"E56.4.17"),sQuery(id+"F0.wireOp",EDGE,"E56.4.18"),sQuery(id+"F0.wireOp",EDGE,"E56.4.19"),sQuery(id+"F0.wireOp",EDGE,"E56.4.20"),sQuery(id+"F0.wireOp",EDGE,"E56.4.21"),sQuery(id+"F0.wireOp",EDGE,"E56.4.22"),sQuery(id+"F0.wireOp",EDGE,"E56.4.23"),sQuery(id+"F0.wireOp",EDGE,"E56.4.24"),sQuery(id+"F0.wireOp",EDGE,"E56.4.25"),sQuery(id+"F0.wireOp",EDGE,"E56.4.26"),sQuery(id+"F0.wireOp",EDGE,"E56.4.27"),sQuery(id+"F0.wireOp",EDGE,"E56.4.28"),sQuery(id+"F0.wireOp",EDGE,"E56.4.29"),sQuery(id+"F0.wireOp",EDGE,"E56.5.0"),sQuery(id+"F0.wireOp",EDGE,"E56.5.1"),sQuery(id+"F0.wireOp",EDGE,"E56.5.2"),sQuery(id+"F0.wireOp",EDGE,"E56.5.3"),sQuery(id+"F0.wireOp",EDGE,"E56.5.4"),sQuery(id+"F0.wireOp",EDGE,"E56.5.5"),sQuery(id+"F0.wireOp",EDGE,"E56.5.6"),sQuery(id+"F0.wireOp",EDGE,"E56.5.7"),sQuery(id+"F0.wireOp",EDGE,"E56.5.8"),sQuery(id+"F0.wireOp",EDGE,"E56.5.9"),sQuery(id+"F0.wireOp",EDGE,"E56.5.10"),sQuery(id+"F0.wireOp",EDGE,"E56.5.11"),sQuery(id+"F0.wireOp",EDGE,"E56.5.12"),sQuery(id+"F0.wireOp",EDGE,"E56.5.13"),sQuery(id+"F0.wireOp",EDGE,"E56.5.14"),sQuery(id+"F0.wireOp",EDGE,"E56.5.15"),sQuery(id+"F0.wireOp",EDGE,"E56.5.16"),sQuery(id+"F0.wireOp",EDGE,"E56.5.17"),sQuery(id+"F0.wireOp",EDGE,"E56.5.18"),sQuery(id+"F0.wireOp",EDGE,"E56.5.19"),sQuery(id+"F0.wireOp",EDGE,"E56.5.20"),sQuery(id+"F0.wireOp",EDGE,"E56.5.21"),sQuery(id+"F0.wireOp",EDGE,"E56.5.22"),sQuery(id+"F0.wireOp",EDGE,"E56.5.23"),sQuery(id+"F0.wireOp",EDGE,"E56.5.24"),sQuery(id+"F0.wireOp",EDGE,"E56.5.25"),sQuery(id+"F0.wireOp",EDGE,"E56.5.26"),sQuery(id+"F0.wireOp",EDGE,"E56.5.27"),sQuery(id+"F0.wireOp",EDGE,"E56.5.28"),sQuery(id+"F0.wireOp",EDGE,"E56.5.29"),sQuery(id+"F0.wireOp",EDGE,"E56.6.0"),sQuery(id+"F0.wireOp",EDGE,"E56.6.1"),sQuery(id+"F0.wireOp",EDGE,"E56.6.2"),sQuery(id+"F0.wireOp",EDGE,"E56.6.3"),sQuery(id+"F0.wireOp",EDGE,"E56.6.4"),sQuery(id+"F0.wireOp",EDGE,"E56.6.5"),sQuery(id+"F0.wireOp",EDGE,"E56.6.6"),sQuery(id+"F0.wireOp",EDGE,"E56.6.7"),sQuery(id+"F0.wireOp",EDGE,"E56.6.8"),sQuery(id+"F0.wireOp",EDGE,"E56.6.9"),sQuery(id+"F0.wireOp",EDGE,"E56.6.10"),sQuery(id+"F0.wireOp",EDGE,"E56.6.11"),sQuery(id+"F0.wireOp",EDGE,"E56.6.12"),sQuery(id+"F0.wireOp",EDGE,"E56.6.13"),sQuery(id+"F0.wireOp",EDGE,"E56.6.14"),sQuery(id+"F0.wireOp",EDGE,"E56.6.15"),sQuery(id+"F0.wireOp",EDGE,"E56.6.16"),sQuery(id+"F0.wireOp",EDGE,"E56.6.17"),sQuery(id+"F0.wireOp",EDGE,"E56.6.18"),sQuery(id+"F0.wireOp",EDGE,"E56.6.19"),sQuery(id+"F0.wireOp",EDGE,"E56.6.20"),sQuery(id+"F0.wireOp",EDGE,"E56.6.21"),sQuery(id+"F0.wireOp",EDGE,"E56.6.22"),sQuery(id+"F0.wireOp",EDGE,"E56.6.23"),sQuery(id+"F0.wireOp",EDGE,"E56.6.24"),sQuery(id+"F0.wireOp",EDGE,"E56.6.25"),sQuery(id+"F0.wireOp",EDGE,"E56.6.26"),sQuery(id+"F0.wireOp",EDGE,"E56.6.27"),sQuery(id+"F0.wireOp",EDGE,"E56.6.28"),sQuery(id+"F0.wireOp",EDGE,"E56.6.29"),sQuery(id+"F0.wireOp",EDGE,"E56.7.0"),sQuery(id+"F0.wireOp",EDGE,"E56.7.1"),sQuery(id+"F0.wireOp",EDGE,"E56.7.2"),sQuery(id+"F0.wireOp",EDGE,"E56.7.3"),sQuery(id+"F0.wireOp",EDGE,"E56.7.4"),sQuery(id+"F0.wireOp",EDGE,"E56.7.5"),sQuery(id+"F0.wireOp",EDGE,"E56.7.6"),sQuery(id+"F0.wireOp",EDGE,"E56.7.7"),sQuery(id+"F0.wireOp",EDGE,"E56.7.8"),sQuery(id+"F0.wireOp",EDGE,"E56.7.9"),sQuery(id+"F0.wireOp",EDGE,"E56.7.10"),sQuery(id+"F0.wireOp",EDGE,"E56.7.11"),sQuery(id+"F0.wireOp",EDGE,"E56.7.12"),sQuery(id+"F0.wireOp",EDGE,"E56.7.13"),sQuery(id+"F0.wireOp",EDGE,"E56.7.14"),sQuery(id+"F0.wireOp",EDGE,"E56.7.15"),sQuery(id+"F0.wireOp",EDGE,"E56.7.16"),sQuery(id+"F0.wireOp",EDGE,"E56.7.17"),sQuery(id+"F0.wireOp",EDGE,"E56.7.18"),sQuery(id+"F0.wireOp",EDGE,"E56.7.19"),sQuery(id+"F0.wireOp",EDGE,"E56.7.20"),sQuery(id+"F0.wireOp",EDGE,"E56.7.21"),sQuery(id+"F0.wireOp",EDGE,"E56.7.22"),sQuery(id+"F0.wireOp",EDGE,"E56.7.23"),sQuery(id+"F0.wireOp",EDGE,"E56.7.24"),sQuery(id+"F0.wireOp",EDGE,"E56.7.25"),sQuery(id+"F0.wireOp",EDGE,"E56.7.26"),sQuery(id+"F0.wireOp",EDGE,"E56.7.27"),sQuery(id+"F0.wireOp",EDGE,"E56.7.28"),sQuery(id+"F0.wireOp",EDGE,"E56.7.29"),sQuery(id+"F0.wireOp",EDGE,"E56.8.0"),sQuery(id+"F0.wireOp",EDGE,"E56.8.1"),sQuery(id+"F0.wireOp",EDGE,"E56.8.2"),sQuery(id+"F0.wireOp",EDGE,"E56.8.3"),sQuery(id+"F0.wireOp",EDGE,"E56.8.4"),sQuery(id+"F0.wireOp",EDGE,"E56.8.5"),sQuery(id+"F0.wireOp",EDGE,"E56.8.6"),sQuery(id+"F0.wireOp",EDGE,"E56.8.7"),sQuery(id+"F0.wireOp",EDGE,"E56.8.8"),sQuery(id+"F0.wireOp",EDGE,"E56.8.9"),sQuery(id+"F0.wireOp",EDGE,"E56.8.10"),sQuery(id+"F0.wireOp",EDGE,"E56.8.11"),sQuery(id+"F0.wireOp",EDGE,"E56.8.12"),sQuery(id+"F0.wireOp",EDGE,"E56.8.13"),sQuery(id+"F0.wireOp",EDGE,"E56.8.14"),sQuery(id+"F0.wireOp",EDGE,"E56.8.15"),sQuery(id+"F0.wireOp",EDGE,"E56.8.16"),sQuery(id+"F0.wireOp",EDGE,"E56.8.17"),sQuery(id+"F0.wireOp",EDGE,"E56.8.18"),sQuery(id+"F0.wireOp",EDGE,"E56.8.19"),sQuery(id+"F0.wireOp",EDGE,"E56.8.20"),sQuery(id+"F0.wireOp",EDGE,"E56.8.21"),sQuery(id+"F0.wireOp",EDGE,"E56.8.22"),sQuery(id+"F0.wireOp",EDGE,"E56.8.23"),sQuery(id+"F0.wireOp",EDGE,"E56.8.24"),sQuery(id+"F0.wireOp",EDGE,"E56.8.25"),sQuery(id+"F0.wireOp",EDGE,"E56.8.26"),sQuery(id+"F0.wireOp",EDGE,"E56.8.27"),sQuery(id+"F0.wireOp",EDGE,"E56.8.28"),sQuery(id+"F0.wireOp",EDGE,"E56.8.29"),sQuery(id+"F0.wireOp",EDGE,"E56.9.0"),sQuery(id+"F0.wireOp",EDGE,"E56.9.1"),sQuery(id+"F0.wireOp",EDGE,"E56.9.2"),sQuery(id+"F0.wireOp",EDGE,"E56.9.3"),sQuery(id+"F0.wireOp",EDGE,"E56.9.4"),sQuery(id+"F0.wireOp",EDGE,"E56.9.5"),sQuery(id+"F0.wireOp",EDGE,"E56.9.6"),sQuery(id+"F0.wireOp",EDGE,"E56.9.7"),sQuery(id+"F0.wireOp",EDGE,"E56.9.8"),sQuery(id+"F0.wireOp",EDGE,"E56.9.9"),sQuery(id+"F0.wireOp",EDGE,"E56.9.10"),sQuery(id+"F0.wireOp",EDGE,"E56.9.11"),sQuery(id+"F0.wireOp",EDGE,"E56.9.12"),sQuery(id+"F0.wireOp",EDGE,"E56.9.13"),sQuery(id+"F0.wireOp",EDGE,"E56.9.14"),sQuery(id+"F0.wireOp",EDGE,"E56.9.15"),sQuery(id+"F0.wireOp",EDGE,"E56.9.16"),sQuery(id+"F0.wireOp",EDGE,"E56.9.17"),sQuery(id+"F0.wireOp",EDGE,"E56.9.18"),sQuery(id+"F0.wireOp",EDGE,"E56.9.19"),sQuery(id+"F0.wireOp",EDGE,"E56.9.20"),sQuery(id+"F0.wireOp",EDGE,"E56.9.21"),sQuery(id+"F0.wireOp",EDGE,"E56.9.22"),sQuery(id+"F0.wireOp",EDGE,"E56.9.23"),sQuery(id+"F0.wireOp",EDGE,"E56.9.24"),sQuery(id+"F0.wireOp",EDGE,"E56.9.25"),sQuery(id+"F0.wireOp",EDGE,"E56.9.26"),sQuery(id+"F0.wireOp",EDGE,"E56.9.27"),sQuery(id+"F0.wireOp",EDGE,"E56.9.28"),sQuery(id+"F0.wireOp",EDGE,"E56.9.29"),sQuery(id+"F0.wireOp",EDGE,"E56.10.0"),sQuery(id+"F0.wireOp",EDGE,"E56.10.1"),sQuery(id+"F0.wireOp",EDGE,"E56.10.2"),sQuery(id+"F0.wireOp",EDGE,"E56.10.3"),sQuery(id+"F0.wireOp",EDGE,"E56.10.4"),sQuery(id+"F0.wireOp",EDGE,"E56.10.5"),sQuery(id+"F0.wireOp",EDGE,"E56.10.6"),sQuery(id+"F0.wireOp",EDGE,"E56.10.7"),sQuery(id+"F0.wireOp",EDGE,"E56.10.8"),sQuery(id+"F0.wireOp",EDGE,"E56.10.9"),sQuery(id+"F0.wireOp",EDGE,"E56.10.10"),sQuery(id+"F0.wireOp",EDGE,"E56.10.11"),sQuery(id+"F0.wireOp",EDGE,"E56.10.12"),sQuery(id+"F0.wireOp",EDGE,"E56.10.13"),sQuery(id+"F0.wireOp",EDGE,"E56.10.14"),sQuery(id+"F0.wireOp",EDGE,"E56.10.15"),sQuery(id+"F0.wireOp",EDGE,"E56.10.16"),sQuery(id+"F0.wireOp",EDGE,"E56.10.17"),sQuery(id+"F0.wireOp",EDGE,"E56.10.18"),sQuery(id+"F0.wireOp",EDGE,"E56.10.19"),sQuery(id+"F0.wireOp",EDGE,"E56.10.20"),sQuery(id+"F0.wireOp",EDGE,"E56.10.21"),sQuery(id+"F0.wireOp",EDGE,"E56.10.22"),sQuery(id+"F0.wireOp",EDGE,"E56.10.23"),sQuery(id+"F0.wireOp",EDGE,"E56.10.24"),sQuery(id+"F0.wireOp",EDGE,"E56.10.25"),sQuery(id+"F0.wireOp",EDGE,"E56.10.26"),sQuery(id+"F0.wireOp",EDGE,"E56.10.27"),sQuery(id+"F0.wireOp",EDGE,"E56.10.28"),sQuery(id+"F0.wireOp",EDGE,"E56.10.29"),sQuery(id+"F0.wireOp",EDGE,"E56.11.0"),sQuery(id+"F0.wireOp",EDGE,"E56.11.1"),sQuery(id+"F0.wireOp",EDGE,"E56.11.2"),sQuery(id+"F0.wireOp",EDGE,"E56.11.3"),sQuery(id+"F0.wireOp",EDGE,"E56.11.4"),sQuery(id+"F0.wireOp",EDGE,"E56.11.5"),sQuery(id+"F0.wireOp",EDGE,"E56.11.6"),sQuery(id+"F0.wireOp",EDGE,"E56.11.7"),sQuery(id+"F0.wireOp",EDGE,"E56.11.8"),sQuery(id+"F0.wireOp",EDGE,"E56.11.9"),sQuery(id+"F0.wireOp",EDGE,"E56.11.10"),sQuery(id+"F0.wireOp",EDGE,"E56.11.11"),sQuery(id+"F0.wireOp",EDGE,"E56.11.12"),sQuery(id+"F0.wireOp",EDGE,"E56.11.13"),sQuery(id+"F0.wireOp",EDGE,"E56.11.14"),sQuery(id+"F0.wireOp",EDGE,"E56.11.15"),sQuery(id+"F0.wireOp",EDGE,"E56.11.16"),sQuery(id+"F0.wireOp",EDGE,"E56.11.17"),sQuery(id+"F0.wireOp",EDGE,"E56.11.18"),sQuery(id+"F0.wireOp",EDGE,"E56.11.19"),sQuery(id+"F0.wireOp",EDGE,"E56.11.20"),sQuery(id+"F0.wireOp",EDGE,"E56.11.21"),sQuery(id+"F0.wireOp",EDGE,"E56.11.22"),sQuery(id+"F0.wireOp",EDGE,"E56.11.23"),sQuery(id+"F0.wireOp",EDGE,"E56.11.24"),sQuery(id+"F0.wireOp",EDGE,"E56.11.25"),sQuery(id+"F0.wireOp",EDGE,"E56.11.26"),sQuery(id+"F0.wireOp",EDGE,"E56.11.27"),sQuery(id+"F0.wireOp",EDGE,"E56.11.28"),sQuery(id+"F0.wireOp",EDGE,"E56.11.29"),sQuery(id+"F0.wireOp",EDGE,"E56.12.0"),sQuery(id+"F0.wireOp",EDGE,"E56.12.1"),sQuery(id+"F0.wireOp",EDGE,"E56.12.2"),sQuery(id+"F0.wireOp",EDGE,"E56.12.3"),sQuery(id+"F0.wireOp",EDGE,"E56.12.4"),sQuery(id+"F0.wireOp",EDGE,"E56.12.5"),sQuery(id+"F0.wireOp",EDGE,"E56.12.6"),sQuery(id+"F0.wireOp",EDGE,"E56.12.7"),sQuery(id+"F0.wireOp",EDGE,"E56.12.8"),sQuery(id+"F0.wireOp",EDGE,"E56.12.9"),sQuery(id+"F0.wireOp",EDGE,"E56.12.10"),sQuery(id+"F0.wireOp",EDGE,"E56.12.11"),sQuery(id+"F0.wireOp",EDGE,"E56.12.12"),sQuery(id+"F0.wireOp",EDGE,"E56.12.13"),sQuery(id+"F0.wireOp",EDGE,"E56.12.14"),sQuery(id+"F0.wireOp",EDGE,"E56.12.15"),sQuery(id+"F0.wireOp",EDGE,"E56.12.16"),sQuery(id+"F0.wireOp",EDGE,"E56.12.17"),sQuery(id+"F0.wireOp",EDGE,"E56.12.18"),sQuery(id+"F0.wireOp",EDGE,"E56.12.19"),sQuery(id+"F0.wireOp",EDGE,"E56.12.20"),sQuery(id+"F0.wireOp",EDGE,"E56.12.21"),sQuery(id+"F0.wireOp",EDGE,"E56.12.22"),sQuery(id+"F0.wireOp",EDGE,"E56.12.23"),sQuery(id+"F0.wireOp",EDGE,"E56.12.24"),sQuery(id+"F0.wireOp",EDGE,"E56.12.25"),sQuery(id+"F0.wireOp",EDGE,"E56.12.26"),sQuery(id+"F0.wireOp",EDGE,"E56.12.27"),sQuery(id+"F0.wireOp",EDGE,"E56.12.28"),sQuery(id+"F0.wireOp",EDGE,"E56.12.29"),sQuery(id+"F0.wireOp",EDGE,"E56.13.0"),sQuery(id+"F0.wireOp",EDGE,"E56.13.1"),sQuery(id+"F0.wireOp",EDGE,"E56.13.2"),sQuery(id+"F0.wireOp",EDGE,"E56.13.3"),sQuery(id+"F0.wireOp",EDGE,"E56.13.4"),sQuery(id+"F0.wireOp",EDGE,"E56.13.5"),sQuery(id+"F0.wireOp",EDGE,"E56.13.6"),sQuery(id+"F0.wireOp",EDGE,"E56.13.7"),sQuery(id+"F0.wireOp",EDGE,"E56.13.8"),sQuery(id+"F0.wireOp",EDGE,"E56.13.9"),sQuery(id+"F0.wireOp",EDGE,"E56.13.10"),sQuery(id+"F0.wireOp",EDGE,"E56.13.11"),sQuery(id+"F0.wireOp",EDGE,"E56.13.12"),sQuery(id+"F0.wireOp",EDGE,"E56.13.13"),sQuery(id+"F0.wireOp",EDGE,"E56.13.14"),sQuery(id+"F0.wireOp",EDGE,"E56.13.15"),sQuery(id+"F0.wireOp",EDGE,"E56.13.16"),sQuery(id+"F0.wireOp",EDGE,"E56.13.17"),sQuery(id+"F0.wireOp",EDGE,"E56.13.18"),sQuery(id+"F0.wireOp",EDGE,"E56.13.19"),sQuery(id+"F0.wireOp",EDGE,"E56.13.20"),sQuery(id+"F0.wireOp",EDGE,"E56.13.21"),sQuery(id+"F0.wireOp",EDGE,"E56.13.22"),sQuery(id+"F0.wireOp",EDGE,"E56.13.23"),sQuery(id+"F0.wireOp",EDGE,"E56.13.24"),sQuery(id+"F0.wireOp",EDGE,"E56.13.25"),sQuery(id+"F0.wireOp",EDGE,"E56.13.26"),sQuery(id+"F0.wireOp",EDGE,"E56.13.27"),sQuery(id+"F0.wireOp",EDGE,"E56.13.28"),sQuery(id+"F0.wireOp",EDGE,"E56.13.29"),sQuery(id+"F0.wireOp",EDGE,"E56.14.0"),sQuery(id+"F0.wireOp",EDGE,"E56.14.1"),sQuery(id+"F0.wireOp",EDGE,"E56.14.2"),sQuery(id+"F0.wireOp",EDGE,"E56.14.3"),sQuery(id+"F0.wireOp",EDGE,"E56.14.4"),sQuery(id+"F0.wireOp",EDGE,"E56.14.5"),sQuery(id+"F0.wireOp",EDGE,"E56.14.6"),sQuery(id+"F0.wireOp",EDGE,"E56.14.7"),sQuery(id+"F0.wireOp",EDGE,"E56.14.8"),sQuery(id+"F0.wireOp",EDGE,"E56.14.9"),sQuery(id+"F0.wireOp",EDGE,"E56.14.10"),sQuery(id+"F0.wireOp",EDGE,"E56.14.11"),sQuery(id+"F0.wireOp",EDGE,"E56.14.12"),sQuery(id+"F0.wireOp",EDGE,"E56.14.13"),sQuery(id+"F0.wireOp",EDGE,"E56.14.14"),sQuery(id+"F0.wireOp",EDGE,"E56.14.15"),sQuery(id+"F0.wireOp",EDGE,"E56.14.16"),sQuery(id+"F0.wireOp",EDGE,"E56.14.17"),sQuery(id+"F0.wireOp",EDGE,"E56.14.18"),sQuery(id+"F0.wireOp",EDGE,"E56.14.19"),sQuery(id+"F0.wireOp",EDGE,"E56.14.20"),sQuery(id+"F0.wireOp",EDGE,"E56.14.21"),sQuery(id+"F0.wireOp",EDGE,"E56.14.22"),sQuery(id+"F0.wireOp",EDGE,"E56.14.23"),sQuery(id+"F0.wireOp",EDGE,"E56.14.24"),sQuery(id+"F0.wireOp",EDGE,"E56.14.25"),sQuery(id+"F0.wireOp",EDGE,"E56.14.26"),sQuery(id+"F0.wireOp",EDGE,"E56.14.27"),sQuery(id+"F0.wireOp",EDGE,"E56.14.28"),sQuery(id+"F0.wireOp",EDGE,"E56.14.29"),sQuery(id+"F0.wireOp",EDGE,"E56.15.0"),sQuery(id+"F0.wireOp",EDGE,"E56.15.1"),sQuery(id+"F0.wireOp",EDGE,"E56.15.2"),sQuery(id+"F0.wireOp",EDGE,"E56.15.3"),sQuery(id+"F0.wireOp",EDGE,"E56.15.4"),sQuery(id+"F0.wireOp",EDGE,"E56.15.5"),sQuery(id+"F0.wireOp",EDGE,"E56.15.6"),sQuery(id+"F0.wireOp",EDGE,"E56.15.7"),sQuery(id+"F0.wireOp",EDGE,"E56.15.8"),sQuery(id+"F0.wireOp",EDGE,"E56.15.9"),sQuery(id+"F0.wireOp",EDGE,"E56.15.10"),sQuery(id+"F0.wireOp",EDGE,"E56.15.11"),sQuery(id+"F0.wireOp",EDGE,"E56.15.12"),sQuery(id+"F0.wireOp",EDGE,"E56.15.13"),sQuery(id+"F0.wireOp",EDGE,"E56.15.14"),sQuery(id+"F0.wireOp",EDGE,"E56.15.15"),sQuery(id+"F0.wireOp",EDGE,"E56.15.16"),sQuery(id+"F0.wireOp",EDGE,"E56.15.17"),sQuery(id+"F0.wireOp",EDGE,"E56.15.18"),sQuery(id+"F0.wireOp",EDGE,"E56.15.19"),sQuery(id+"F0.wireOp",EDGE,"E56.15.20"),sQuery(id+"F0.wireOp",EDGE,"E56.15.21"),sQuery(id+"F0.wireOp",EDGE,"E56.15.22"),sQuery(id+"F0.wireOp",EDGE,"E56.15.23"),sQuery(id+"F0.wireOp",EDGE,"E56.15.24"),sQuery(id+"F0.wireOp",EDGE,"E56.15.25"),sQuery(id+"F0.wireOp",EDGE,"E56.15.26"),sQuery(id+"F0.wireOp",EDGE,"E56.15.27"),sQuery(id+"F0.wireOp",EDGE,"E56.15.28"),sQuery(id+"F0.wireOp",EDGE,"E56.15.29"),sQuery(id+"F0.wireOp",EDGE,"E56.16.0"),sQuery(id+"F0.wireOp",EDGE,"E56.16.1"),sQuery(id+"F0.wireOp",EDGE,"E56.16.2"),sQuery(id+"F0.wireOp",EDGE,"E56.16.3"),sQuery(id+"F0.wireOp",EDGE,"E56.16.4"),sQuery(id+"F0.wireOp",EDGE,"E56.16.5"),sQuery(id+"F0.wireOp",EDGE,"E56.16.6"),sQuery(id+"F0.wireOp",EDGE,"E56.16.7"),sQuery(id+"F0.wireOp",EDGE,"E56.16.8"),sQuery(id+"F0.wireOp",EDGE,"E56.16.9"),sQuery(id+"F0.wireOp",EDGE,"E56.16.10"),sQuery(id+"F0.wireOp",EDGE,"E56.16.11"),sQuery(id+"F0.wireOp",EDGE,"E56.16.12"),sQuery(id+"F0.wireOp",EDGE,"E56.16.13"),sQuery(id+"F0.wireOp",EDGE,"E56.16.14"),sQuery(id+"F0.wireOp",EDGE,"E56.16.15"),sQuery(id+"F0.wireOp",EDGE,"E56.16.16"),sQuery(id+"F0.wireOp",EDGE,"E56.16.17"),sQuery(id+"F0.wireOp",EDGE,"E56.16.18"),sQuery(id+"F0.wireOp",EDGE,"E56.16.19"),sQuery(id+"F0.wireOp",EDGE,"E56.16.20"),sQuery(id+"F0.wireOp",EDGE,"E56.16.21"),sQuery(id+"F0.wireOp",EDGE,"E56.16.22"),sQuery(id+"F0.wireOp",EDGE,"E56.16.23"),sQuery(id+"F0.wireOp",EDGE,"E56.16.24"),sQuery(id+"F0.wireOp",EDGE,"E56.16.25"),sQuery(id+"F0.wireOp",EDGE,"E56.16.26"),sQuery(id+"F0.wireOp",EDGE,"E56.16.27"),sQuery(id+"F0.wireOp",EDGE,"E56.16.28"),sQuery(id+"F0.wireOp",EDGE,"E56.16.29"),sQuery(id+"F0.wireOp",EDGE,"E56.17.0"),sQuery(id+"F0.wireOp",EDGE,"E56.17.1"),sQuery(id+"F0.wireOp",EDGE,"E56.17.2"),sQuery(id+"F0.wireOp",EDGE,"E56.17.3"),sQuery(id+"F0.wireOp",EDGE,"E56.17.4"),sQuery(id+"F0.wireOp",EDGE,"E56.17.5"),sQuery(id+"F0.wireOp",EDGE,"E56.17.6"),sQuery(id+"F0.wireOp",EDGE,"E56.17.7"),sQuery(id+"F0.wireOp",EDGE,"E56.17.8"),sQuery(id+"F0.wireOp",EDGE,"E56.17.9"),sQuery(id+"F0.wireOp",EDGE,"E56.17.10"),sQuery(id+"F0.wireOp",EDGE,"E56.17.11"),sQuery(id+"F0.wireOp",EDGE,"E56.17.12"),sQuery(id+"F0.wireOp",EDGE,"E56.17.13"),sQuery(id+"F0.wireOp",EDGE,"E56.17.14"),sQuery(id+"F0.wireOp",EDGE,"E56.17.15"),sQuery(id+"F0.wireOp",EDGE,"E56.17.16"),sQuery(id+"F0.wireOp",EDGE,"E56.17.17"),sQuery(id+"F0.wireOp",EDGE,"E56.17.18"),sQuery(id+"F0.wireOp",EDGE,"E56.17.19"),sQuery(id+"F0.wireOp",EDGE,"E56.17.20"),sQuery(id+"F0.wireOp",EDGE,"E56.17.21"),sQuery(id+"F0.wireOp",EDGE,"E56.17.22"),sQuery(id+"F0.wireOp",EDGE,"E56.17.23"),sQuery(id+"F0.wireOp",EDGE,"E56.17.24"),sQuery(id+"F0.wireOp",EDGE,"E56.17.25"),sQuery(id+"F0.wireOp",EDGE,"E56.17.26"),sQuery(id+"F0.wireOp",EDGE,"E56.17.27"),sQuery(id+"F0.wireOp",EDGE,"E56.17.28"),sQuery(id+"F0.wireOp",EDGE,"E56.17.29"),sQuery(id+"F0.wireOp",EDGE,"E56.18.0"),sQuery(id+"F0.wireOp",EDGE,"E56.18.1"),sQuery(id+"F0.wireOp",EDGE,"E56.18.2"),sQuery(id+"F0.wireOp",EDGE,"E56.18.3"),sQuery(id+"F0.wireOp",EDGE,"E56.18.4"),sQuery(id+"F0.wireOp",EDGE,"E56.18.5"),sQuery(id+"F0.wireOp",EDGE,"E56.18.6"),sQuery(id+"F0.wireOp",EDGE,"E56.18.7"),sQuery(id+"F0.wireOp",EDGE,"E56.18.8"),sQuery(id+"F0.wireOp",EDGE,"E56.18.9"),sQuery(id+"F0.wireOp",EDGE,"E56.18.10"),sQuery(id+"F0.wireOp",EDGE,"E56.18.11"),sQuery(id+"F0.wireOp",EDGE,"E56.18.12"),sQuery(id+"F0.wireOp",EDGE,"E56.18.13"),sQuery(id+"F0.wireOp",EDGE,"E56.18.14"),sQuery(id+"F0.wireOp",EDGE,"E56.18.15"),sQuery(id+"F0.wireOp",EDGE,"E56.18.16"),sQuery(id+"F0.wireOp",EDGE,"E56.18.17"),sQuery(id+"F0.wireOp",EDGE,"E56.18.18"),sQuery(id+"F0.wireOp",EDGE,"E56.18.19"),sQuery(id+"F0.wireOp",EDGE,"E56.18.20"),sQuery(id+"F0.wireOp",EDGE,"E56.18.21"),sQuery(id+"F0.wireOp",EDGE,"E56.18.22"),sQuery(id+"F0.wireOp",EDGE,"E56.18.23"),sQuery(id+"F0.wireOp",EDGE,"E56.18.24"),sQuery(id+"F0.wireOp",EDGE,"E56.18.25"),sQuery(id+"F0.wireOp",EDGE,"E56.18.26"),sQuery(id+"F0.wireOp",EDGE,"E56.18.27"),sQuery(id+"F0.wireOp",EDGE,"E56.18.28"),sQuery(id+"F0.wireOp",EDGE,"E56.18.29"),sQuery(id+"F0.wireOp",EDGE,"E56.19.0"),sQuery(id+"F0.wireOp",EDGE,"E56.19.1"),sQuery(id+"F0.wireOp",EDGE,"E56.19.2"),sQuery(id+"F0.wireOp",EDGE,"E56.19.3"),sQuery(id+"F0.wireOp",EDGE,"E56.19.4"),sQuery(id+"F0.wireOp",EDGE,"E56.19.5"),sQuery(id+"F0.wireOp",EDGE,"E56.19.6"),sQuery(id+"F0.wireOp",EDGE,"E56.19.7"),sQuery(id+"F0.wireOp",EDGE,"E56.19.8"),sQuery(id+"F0.wireOp",EDGE,"E56.19.9"),sQuery(id+"F0.wireOp",EDGE,"E56.19.10"),sQuery(id+"F0.wireOp",EDGE,"E56.19.11"),sQuery(id+"F0.wireOp",EDGE,"E56.19.12"),sQuery(id+"F0.wireOp",EDGE,"E56.19.13"),sQuery(id+"F0.wireOp",EDGE,"E56.19.14"),sQuery(id+"F0.wireOp",EDGE,"E56.19.15"),sQuery(id+"F0.wireOp",EDGE,"E56.19.16"),sQuery(id+"F0.wireOp",EDGE,"E56.19.17"),sQuery(id+"F0.wireOp",EDGE,"E56.19.18"),sQuery(id+"F0.wireOp",EDGE,"E56.19.19"),sQuery(id+"F0.wireOp",EDGE,"E56.19.20"),sQuery(id+"F0.wireOp",EDGE,"E56.19.21"),sQuery(id+"F0.wireOp",EDGE,"E56.19.22"),sQuery(id+"F0.wireOp",EDGE,"E56.19.23"),sQuery(id+"F0.wireOp",EDGE,"E56.19.24"),sQuery(id+"F0.wireOp",EDGE,"E56.19.25"),sQuery(id+"F0.wireOp",EDGE,"E56.19.26"),sQuery(id+"F0.wireOp",EDGE,"E56.19.27"),sQuery(id+"F0.wireOp",EDGE,"E56.19.28"),sQuery(id+"F0.wireOp",EDGE,"E56.19.29")])]});
            var Q1;
            Q1=makeQuery(id+"F2.opExtrude","SWEPT_BODY",BODY,{"disambiguationData":[OSD([sQuery(id+"F0.wireOp",EDGE,"E4")])]});
            transform(context, id + "F14", {"entities" : qUnion([Q0, Q1]), "transformType" : TransformType.TRANSLATION_3D, "dx" : 0 * mm, "dy" : 0 * mm, "dz" : 2.62 * mm, "makeCopy" : false});
        }
        {
            var Q0;
            Q0=makeQuery(id+"F7.opExtrude","CAP_FACE",FACE,{"disambiguationData":[OSD([sQuery(id+"F6.wireOp",EDGE,"E57.bottom"),sQuery(id+"F6.wireOp",EDGE,"E57.top"),sQuery(id+"F6.wireOp",EDGE,"E57.left"),sQuery(id+"F6.wireOp",EDGE,"E57.right")])],"isStart":true});
            var sketch = newSketch(context, id + "F15", { "sketchPlane" : qUnion([Q0])});
            skCircle(sketch, "E64.0", {"center": v(-22.54, 0) * mm, "radius": 2.87 * mm});
            skCircle(sketch, "E65.0", {"center": v(-22.54, 0) * mm, "radius": 6.07 * mm});
            skPoint(sketch, "E66.0", {"position": v(22.54, 0) * mm});
            skCircle(sketch, "E67", {"center": v(22.54, 0) * mm, "radius": 2.71 * mm});
            skSolve(sketch);
        }
        {
            var Q0;
            Q0=makeQuery(id+"F15.imprint","IMPRINT",FACE,{"disambiguationData":[TD([[makeQuery(id+"F15.imprint","IMPRINT",EDGE,{"derivedFrom":sQuery(id+"F15.wireOp",EDGE,"E67")}),1.0]])]});
            var Q1;
            Q1=sQuery(id+"F15.wireOp",EDGE,"E67");
            extrude(context, id + "F16", {"entities" : qUnion([Q0]), "surfaceEntities" : qUnion([Q1]), "depth" : 3.73 * mm, "offsetDistance" : 25.4 * mm});
        }
        {
            var Q0;
            Q0=makeQuery(id+"F15.imprint","IMPRINT",FACE,{"disambiguationData":[TD([[makeQuery(id+"F15.imprint","IMPRINT",EDGE,{"derivedFrom":sQuery(id+"F15.wireOp",EDGE,"E64.0")}),-1.0]])]});
            var Q1;
            Q1=sQuery(id+"F15.wireOp",EDGE,"E65.0");
            extrude(context, id + "F17", {"entities" : qUnion([Q0]), "surfaceEntities" : qUnion([Q1]), "depth" : 2.92 * mm, "offsetDistance" : 25.4 * mm});
        }
        {
            var Q0;
            Q0=makeQuery(id+"F15.imprint","IMPRINT",FACE,{"disambiguationData":[TD([[makeQuery(id+"F15.imprint","IMPRINT",EDGE,{"derivedFrom":sQuery(id+"F15.wireOp",EDGE,"E65.0")}),-1.0]])]});
            var sketch = newSketch(context, id + "F18", { "sketchPlane" : qUnion([Q0])});
            skPoint(sketch, "E68.0", {"position": v(22.54, 0) * mm});
            skCircle(sketch, "E69", {"center": v(22.54, 0) * mm, "radius": 0.67 * mm});
            skSolve(sketch);
        }
        {
            var Q0;
            Q0 = qSketchRegion(id + "F18", true);
            extrude(context, id + "F19", {"entities" : qUnion([Q0]), "operationType" : NewBodyOperationType.REMOVE, "oppositeDirection" : true, "depth" : 25.4 * mm, "offsetDistance" : 25.4 * mm});
        }
        {
            var Q0;
            Q0=makeQuery(id+"F15.imprint","IMPRINT",FACE,{"disambiguationData":[TD([[makeQuery(id+"F15.imprint","IMPRINT",EDGE,{"derivedFrom":sQuery(id+"F15.wireOp",EDGE,"E67")}),1.0]])]});
            var sketch = newSketch(context, id + "F20", { "sketchPlane" : qUnion([Q0])});
            skPoint(sketch, "E70.0", {"position": v(22.54, 0) * mm});
            skCircle(sketch, "E71", {"center": v(22.54, 0) * mm, "radius": 0.23 * mm});
            skSolve(sketch);
        }
        {
            var Q0;
            Q0 = qSketchRegion(id + "F20", true);
            var Q1;
            Q1=sQuery(id+"F20.wireOp",EDGE,"E71");
            extrude(context, id + "F21", {"entities" : qUnion([Q0]), "operationType" : NewBodyOperationType.REMOVE, "surfaceEntities" : qUnion([Q1]), "depth" : 2.3 * mm, "offsetDistance" : 25.4 * mm});
        }
    });
